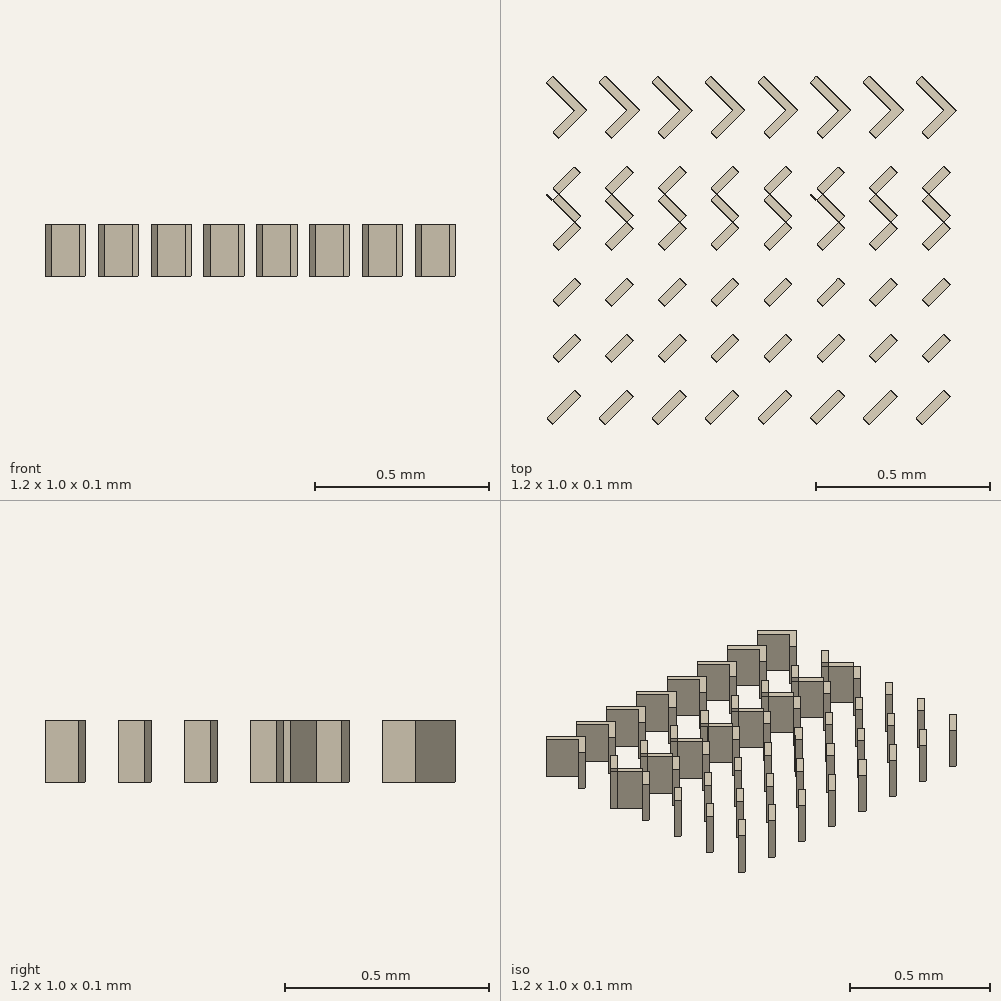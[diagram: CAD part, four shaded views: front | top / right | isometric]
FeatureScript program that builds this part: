
annotation { "Feature Type Name" : "Feature", "Feature Type Description" : "" }
export const myFeature = defineFeature(function(context is Context, id is Id, definition is map)
    precondition{}
    {
        {
            var Q0;
            Q0=qCreatedBy(makeId("Top.planeOp"),FACE);
            var sketch = newSketch(context, id + "F0", { "sketchPlane" : qUnion([Q0])});
            skLineSegment(sketch, "E0.bottom", {"start": v(-3.83, 2.01) * mm, "end": v(-3.93, 2.1) * mm});
            skLineSegment(sketch, "E0.top", {"start": v(-3.81, 2.03) * mm, "end": v(-3.91, 2.13) * mm});
            skLineSegment(sketch, "E0.left", {"start": v(-3.9, 1.93) * mm, "end": v(-3.9, 1.95) * mm});
            skLineSegment(sketch, "E0.right", {"start": v(-3.93, 2.1) * mm, "end": v(-3.91, 2.13) * mm});
            skPoint(sketch, "E0.middle", {"position": v(-3.95, 1.99) * mm});
            skLineSegment(sketch, "E1.bottom", {"start": v(-3.93, 1.95) * mm, "end": v(-3.83, 2.05) * mm});
            skLineSegment(sketch, "E1.top", {"start": v(-3.91, 1.93) * mm, "end": v(-3.81, 2.03) * mm});
            skLineSegment(sketch, "E1.left", {"start": v(-3.93, 1.95) * mm, "end": v(-3.91, 1.93) * mm});
            skLineSegment(sketch, "E1.right", {"start": v(-3.83, 2.05) * mm, "end": v(-3.81, 2.03) * mm});
            skPoint(sketch, "E1.middle", {"position": v(-3.87, 1.99) * mm});
            skLineSegment(sketch, "E2.bottom", {"start": v(-3.83, 1.85) * mm, "end": v(-3.93, 1.95) * mm});
            skLineSegment(sketch, "E2.top", {"start": v(-3.81, 1.87) * mm, "end": v(-3.91, 1.97) * mm});
            skLineSegment(sketch, "E2.left", {"start": v(-3.9, 1.77) * mm, "end": v(-3.9, 1.79) * mm});
            skLineSegment(sketch, "E2.right", {"start": v(-3.93, 1.95) * mm, "end": v(-3.91, 1.97) * mm});
            skPoint(sketch, "E2.middle", {"position": v(-3.95, 1.83) * mm});
            skLineSegment(sketch, "E3.bottom", {"start": v(-3.93, 1.79) * mm, "end": v(-3.83, 1.89) * mm});
            skLineSegment(sketch, "E3.top", {"start": v(-3.91, 1.77) * mm, "end": v(-3.81, 1.87) * mm});
            skLineSegment(sketch, "E3.left", {"start": v(-3.93, 1.79) * mm, "end": v(-3.91, 1.77) * mm});
            skLineSegment(sketch, "E3.right", {"start": v(-3.83, 1.89) * mm, "end": v(-3.81, 1.87) * mm});
            skPoint(sketch, "E3.middle", {"position": v(-3.87, 1.83) * mm});
            skLineSegment(sketch, "E4.bottom", {"start": v(-3.83, 1.69) * mm, "end": v(-3.93, 1.79) * mm});
            skLineSegment(sketch, "E4.top", {"start": v(-3.81, 1.7) * mm, "end": v(-3.9, 1.8) * mm});
            skLineSegment(sketch, "E4.left", {"start": v(-3.9, 1.6) * mm, "end": v(-3.9, 1.62) * mm});
            skLineSegment(sketch, "E4.right", {"start": v(-3.93, 1.79) * mm, "end": v(-3.9, 1.8) * mm});
            skPoint(sketch, "E4.middle", {"position": v(-3.95, 1.67) * mm});
            skLineSegment(sketch, "E5.bottom", {"start": v(-3.93, 1.63) * mm, "end": v(-3.83, 1.72) * mm});
            skLineSegment(sketch, "E5.top", {"start": v(-3.9, 1.6) * mm, "end": v(-3.81, 1.7) * mm});
            skLineSegment(sketch, "E5.left", {"start": v(-3.93, 1.63) * mm, "end": v(-3.9, 1.6) * mm});
            skLineSegment(sketch, "E5.right", {"start": v(-3.83, 1.72) * mm, "end": v(-3.81, 1.7) * mm});
            skPoint(sketch, "E5.middle", {"position": v(-3.87, 1.67) * mm});
            skLineSegment(sketch, "E6.bottom", {"start": v(-3.83, 1.53) * mm, "end": v(-3.93, 1.63) * mm});
            skLineSegment(sketch, "E6.top", {"start": v(-3.81, 1.54) * mm, "end": v(-3.9, 1.64) * mm});
            skLineSegment(sketch, "E6.left", {"start": v(-3.9, 1.45) * mm, "end": v(-3.9, 1.46) * mm});
            skLineSegment(sketch, "E6.right", {"start": v(-3.93, 1.63) * mm, "end": v(-3.9, 1.64) * mm});
            skPoint(sketch, "E6.middle", {"position": v(-3.95, 1.5) * mm});
            skLineSegment(sketch, "E7.bottom", {"start": v(-3.93, 1.46) * mm, "end": v(-3.83, 1.56) * mm});
            skLineSegment(sketch, "E7.top", {"start": v(-3.9, 1.45) * mm, "end": v(-3.81, 1.54) * mm});
            skLineSegment(sketch, "E7.left", {"start": v(-3.93, 1.46) * mm, "end": v(-3.9, 1.45) * mm});
            skLineSegment(sketch, "E7.right", {"start": v(-3.83, 1.56) * mm, "end": v(-3.81, 1.54) * mm});
            skPoint(sketch, "E7.middle", {"position": v(-3.87, 1.5) * mm});
            skLineSegment(sketch, "E8.bottom", {"start": v(-3.83, 1.36) * mm, "end": v(-3.93, 1.46) * mm});
            skLineSegment(sketch, "E8.top", {"start": v(-3.81, 1.38) * mm, "end": v(-3.9, 1.48) * mm});
            skLineSegment(sketch, "E8.left", {"start": v(-3.9, 1.28) * mm, "end": v(-3.9, 1.3) * mm});
            skLineSegment(sketch, "E8.right", {"start": v(-3.93, 1.46) * mm, "end": v(-3.9, 1.48) * mm});
            skPoint(sketch, "E8.middle", {"position": v(-3.95, 1.34) * mm});
            skLineSegment(sketch, "E9.bottom", {"start": v(-3.93, 1.3) * mm, "end": v(-3.83, 1.4) * mm});
            skLineSegment(sketch, "E9.top", {"start": v(-3.9, 1.28) * mm, "end": v(-3.81, 1.38) * mm});
            skLineSegment(sketch, "E9.left", {"start": v(-3.93, 1.3) * mm, "end": v(-3.9, 1.28) * mm});
            skLineSegment(sketch, "E9.right", {"start": v(-3.83, 1.4) * mm, "end": v(-3.81, 1.38) * mm});
            skPoint(sketch, "E9.middle", {"position": v(-3.87, 1.34) * mm});
            skLineSegment(sketch, "E10.bottom", {"start": v(-3.83, 1.2) * mm, "end": v(-3.93, 1.3) * mm});
            skLineSegment(sketch, "E10.top", {"start": v(-3.81, 1.22) * mm, "end": v(-3.9, 1.32) * mm});
            skLineSegment(sketch, "E10.left", {"start": v(-3.9, 1.12) * mm, "end": v(-3.9, 1.14) * mm});
            skLineSegment(sketch, "E10.right", {"start": v(-3.93, 1.3) * mm, "end": v(-3.9, 1.32) * mm});
            skPoint(sketch, "E10.middle", {"position": v(-3.95, 1.18) * mm});
            skLineSegment(sketch, "E11.bottom", {"start": v(-3.93, 1.14) * mm, "end": v(-3.83, 1.24) * mm});
            skLineSegment(sketch, "E11.top", {"start": v(-3.9, 1.12) * mm, "end": v(-3.81, 1.22) * mm});
            skLineSegment(sketch, "E11.left", {"start": v(-3.93, 1.14) * mm, "end": v(-3.9, 1.12) * mm});
            skLineSegment(sketch, "E11.right", {"start": v(-3.83, 1.24) * mm, "end": v(-3.81, 1.22) * mm});
            skPoint(sketch, "E11.middle", {"position": v(-3.87, 1.18) * mm});
            skLineSegment(sketch, "E12.0.1.0", {"start": v(-3.83, 3.56) * mm, "end": v(-3.93, 3.66) * mm});
            skLineSegment(sketch, "E12.0.1.1", {"start": v(-3.83, 3.24) * mm, "end": v(-3.93, 3.33) * mm});
            skPoint(sketch, "E12.0.1.2", {"position": v(-3.87, 4.02) * mm});
            skLineSegment(sketch, "E12.0.1.3", {"start": v(-3.81, 4.06) * mm, "end": v(-3.91, 4.16) * mm});
            skPoint(sketch, "E12.0.1.4", {"position": v(-3.95, 3.37) * mm});
            skLineSegment(sketch, "E12.0.1.5", {"start": v(-3.83, 4.04) * mm, "end": v(-3.93, 4.14) * mm});
            skPoint(sketch, "E12.0.1.6", {"position": v(-3.95, 3.54) * mm});
            skPoint(sketch, "E12.0.1.7", {"position": v(-3.95, 3.86) * mm});
            skPoint(sketch, "E12.0.1.8", {"position": v(-3.87, 3.37) * mm});
            skPoint(sketch, "E12.0.1.9", {"position": v(-3.87, 3.7) * mm});
            skLineSegment(sketch, "E12.0.1.10", {"start": v(-3.83, 3.4) * mm, "end": v(-3.93, 3.5) * mm});
            skPoint(sketch, "E12.0.1.11", {"position": v(-3.87, 3.54) * mm});
            skPoint(sketch, "E12.0.1.12", {"position": v(-3.87, 3.21) * mm});
            skLineSegment(sketch, "E12.0.1.13", {"start": v(-3.83, 3.72) * mm, "end": v(-3.93, 3.82) * mm});
            skPoint(sketch, "E12.0.1.14", {"position": v(-3.95, 4.02) * mm});
            skPoint(sketch, "E12.0.1.15", {"position": v(-3.95, 3.7) * mm});
            skLineSegment(sketch, "E12.0.1.16", {"start": v(-3.83, 3.88) * mm, "end": v(-3.93, 3.98) * mm});
            skPoint(sketch, "E12.0.1.17", {"position": v(-3.95, 3.21) * mm});
            skPoint(sketch, "E12.0.1.18", {"position": v(-3.87, 3.86) * mm});
            skLineSegment(sketch, "E12.0.1.19", {"start": v(-3.81, 3.41) * mm, "end": v(-3.9, 3.51) * mm});
            skLineSegment(sketch, "E12.0.1.20", {"start": v(-3.93, 3.98) * mm, "end": v(-3.83, 4.08) * mm});
            skLineSegment(sketch, "E12.0.1.21", {"start": v(-3.91, 3.8) * mm, "end": v(-3.81, 3.9) * mm});
            skLineSegment(sketch, "E12.0.1.22", {"start": v(-3.81, 3.58) * mm, "end": v(-3.9, 3.68) * mm});
            skLineSegment(sketch, "E12.0.1.23", {"start": v(-3.9, 3.32) * mm, "end": v(-3.81, 3.41) * mm});
            skLineSegment(sketch, "E12.0.1.24", {"start": v(-3.9, 3.64) * mm, "end": v(-3.81, 3.74) * mm});
            skLineSegment(sketch, "E12.0.1.25", {"start": v(-3.93, 3.5) * mm, "end": v(-3.83, 3.6) * mm});
            skLineSegment(sketch, "E12.0.1.26", {"start": v(-3.93, 3.17) * mm, "end": v(-3.83, 3.27) * mm});
            skLineSegment(sketch, "E12.0.1.27", {"start": v(-3.9, 3.48) * mm, "end": v(-3.81, 3.58) * mm});
            skLineSegment(sketch, "E12.0.1.28", {"start": v(-3.93, 3.33) * mm, "end": v(-3.83, 3.43) * mm});
            skLineSegment(sketch, "E12.0.1.29", {"start": v(-3.9, 3.15) * mm, "end": v(-3.81, 3.25) * mm});
            skLineSegment(sketch, "E12.0.1.30", {"start": v(-3.93, 3.66) * mm, "end": v(-3.83, 3.76) * mm});
            skLineSegment(sketch, "E12.0.1.31", {"start": v(-3.93, 3.82) * mm, "end": v(-3.83, 3.92) * mm});
            skLineSegment(sketch, "E12.0.1.32", {"start": v(-3.91, 3.96) * mm, "end": v(-3.81, 4.06) * mm});
            skLineSegment(sketch, "E12.0.1.33", {"start": v(-3.93, 4.14) * mm, "end": v(-3.91, 4.16) * mm});
            skLineSegment(sketch, "E12.0.1.34", {"start": v(-3.81, 3.74) * mm, "end": v(-3.9, 3.84) * mm});
            skLineSegment(sketch, "E12.0.1.35", {"start": v(-3.81, 3.25) * mm, "end": v(-3.9, 3.35) * mm});
            skLineSegment(sketch, "E12.0.1.36", {"start": v(-3.81, 3.9) * mm, "end": v(-3.91, 4) * mm});
            skLineSegment(sketch, "E12.0.1.37", {"start": v(-3.83, 3.92) * mm, "end": v(-3.81, 3.9) * mm});
            skLineSegment(sketch, "E12.0.1.38", {"start": v(-3.83, 3.6) * mm, "end": v(-3.81, 3.58) * mm});
            skLineSegment(sketch, "E12.0.1.39", {"start": v(-3.83, 3.27) * mm, "end": v(-3.81, 3.25) * mm});
            skLineSegment(sketch, "E12.0.1.40", {"start": v(-3.83, 3.76) * mm, "end": v(-3.81, 3.74) * mm});
            skLineSegment(sketch, "E12.0.1.41", {"start": v(-3.83, 3.43) * mm, "end": v(-3.81, 3.41) * mm});
            skLineSegment(sketch, "E12.0.1.42", {"start": v(-3.83, 4.08) * mm, "end": v(-3.81, 4.06) * mm});
            skLineSegment(sketch, "E12.0.1.43", {"start": v(-3.93, 3.82) * mm, "end": v(-3.9, 3.84) * mm});
            skLineSegment(sketch, "E12.0.1.44", {"start": v(-3.93, 3.82) * mm, "end": v(-3.91, 3.8) * mm});
            skLineSegment(sketch, "E12.0.1.45", {"start": v(-3.93, 3.17) * mm, "end": v(-3.9, 3.15) * mm});
            skLineSegment(sketch, "E12.0.1.46", {"start": v(-3.9, 3.8) * mm, "end": v(-3.9, 3.82) * mm});
            skLineSegment(sketch, "E12.0.1.47", {"start": v(-3.9, 3.15) * mm, "end": v(-3.9, 3.17) * mm});
            skLineSegment(sketch, "E12.0.1.48", {"start": v(-3.9, 3.96) * mm, "end": v(-3.9, 3.98) * mm});
            skLineSegment(sketch, "E12.0.1.49", {"start": v(-3.93, 3.33) * mm, "end": v(-3.9, 3.32) * mm});
            skLineSegment(sketch, "E12.0.1.50", {"start": v(-3.93, 3.66) * mm, "end": v(-3.9, 3.64) * mm});
            skLineSegment(sketch, "E12.0.1.51", {"start": v(-3.9, 3.64) * mm, "end": v(-3.9, 3.66) * mm});
            skLineSegment(sketch, "E12.0.1.52", {"start": v(-3.93, 3.5) * mm, "end": v(-3.9, 3.48) * mm});
            skLineSegment(sketch, "E12.0.1.53", {"start": v(-3.93, 3.66) * mm, "end": v(-3.9, 3.68) * mm});
            skLineSegment(sketch, "E12.0.1.54", {"start": v(-3.93, 3.33) * mm, "end": v(-3.9, 3.35) * mm});
            skLineSegment(sketch, "E12.0.1.55", {"start": v(-3.93, 3.98) * mm, "end": v(-3.91, 4) * mm});
            skLineSegment(sketch, "E12.0.1.56", {"start": v(-3.93, 3.98) * mm, "end": v(-3.91, 3.96) * mm});
            skLineSegment(sketch, "E12.0.1.57", {"start": v(-3.93, 3.5) * mm, "end": v(-3.9, 3.51) * mm});
            skLineSegment(sketch, "E12.0.1.58", {"start": v(-3.9, 3.48) * mm, "end": v(-3.9, 3.5) * mm});
            skLineSegment(sketch, "E12.0.1.59", {"start": v(-3.9, 3.32) * mm, "end": v(-3.9, 3.33) * mm});
            skLineSegment(sketch, "E12.1.0.0", {"start": v(-3.68, 1.53) * mm, "end": v(-3.78, 1.63) * mm});
            skLineSegment(sketch, "E12.1.0.1", {"start": v(-3.68, 1.2) * mm, "end": v(-3.78, 1.3) * mm});
            skPoint(sketch, "E12.1.0.2", {"position": v(-3.72, 1.99) * mm});
            skLineSegment(sketch, "E12.1.0.3", {"start": v(-3.66, 2.03) * mm, "end": v(-3.76, 2.13) * mm});
            skPoint(sketch, "E12.1.0.4", {"position": v(-3.8, 1.34) * mm});
            skLineSegment(sketch, "E12.1.0.5", {"start": v(-3.68, 2.01) * mm, "end": v(-3.78, 2.1) * mm});
            skPoint(sketch, "E12.1.0.6", {"position": v(-3.8, 1.5) * mm});
            skPoint(sketch, "E12.1.0.7", {"position": v(-3.8, 1.83) * mm});
            skPoint(sketch, "E12.1.0.8", {"position": v(-3.72, 1.34) * mm});
            skPoint(sketch, "E12.1.0.9", {"position": v(-3.72, 1.67) * mm});
            skLineSegment(sketch, "E12.1.0.10", {"start": v(-3.68, 1.36) * mm, "end": v(-3.78, 1.46) * mm});
            skPoint(sketch, "E12.1.0.11", {"position": v(-3.72, 1.5) * mm});
            skPoint(sketch, "E12.1.0.12", {"position": v(-3.72, 1.18) * mm});
            skLineSegment(sketch, "E12.1.0.13", {"start": v(-3.68, 1.69) * mm, "end": v(-3.78, 1.79) * mm});
            skPoint(sketch, "E12.1.0.14", {"position": v(-3.8, 1.99) * mm});
            skPoint(sketch, "E12.1.0.15", {"position": v(-3.8, 1.67) * mm});
            skLineSegment(sketch, "E12.1.0.16", {"start": v(-3.68, 1.85) * mm, "end": v(-3.78, 1.95) * mm});
            skPoint(sketch, "E12.1.0.17", {"position": v(-3.8, 1.18) * mm});
            skPoint(sketch, "E12.1.0.18", {"position": v(-3.72, 1.83) * mm});
            skLineSegment(sketch, "E12.1.0.19", {"start": v(-3.66, 1.38) * mm, "end": v(-3.76, 1.48) * mm});
            skLineSegment(sketch, "E12.1.0.20", {"start": v(-3.78, 1.95) * mm, "end": v(-3.68, 2.05) * mm});
            skLineSegment(sketch, "E12.1.0.21", {"start": v(-3.76, 1.77) * mm, "end": v(-3.66, 1.87) * mm});
            skLineSegment(sketch, "E12.1.0.22", {"start": v(-3.66, 1.54) * mm, "end": v(-3.76, 1.64) * mm});
            skLineSegment(sketch, "E12.1.0.23", {"start": v(-3.76, 1.28) * mm, "end": v(-3.66, 1.38) * mm});
            skLineSegment(sketch, "E12.1.0.24", {"start": v(-3.76, 1.6) * mm, "end": v(-3.66, 1.7) * mm});
            skLineSegment(sketch, "E12.1.0.25", {"start": v(-3.78, 1.46) * mm, "end": v(-3.68, 1.56) * mm});
            skLineSegment(sketch, "E12.1.0.26", {"start": v(-3.78, 1.14) * mm, "end": v(-3.68, 1.24) * mm});
            skLineSegment(sketch, "E12.1.0.27", {"start": v(-3.76, 1.45) * mm, "end": v(-3.66, 1.54) * mm});
            skLineSegment(sketch, "E12.1.0.28", {"start": v(-3.78, 1.3) * mm, "end": v(-3.68, 1.4) * mm});
            skLineSegment(sketch, "E12.1.0.29", {"start": v(-3.76, 1.12) * mm, "end": v(-3.66, 1.22) * mm});
            skLineSegment(sketch, "E12.1.0.30", {"start": v(-3.78, 1.63) * mm, "end": v(-3.68, 1.72) * mm});
            skLineSegment(sketch, "E12.1.0.31", {"start": v(-3.78, 1.79) * mm, "end": v(-3.68, 1.89) * mm});
            skLineSegment(sketch, "E12.1.0.32", {"start": v(-3.76, 1.93) * mm, "end": v(-3.66, 2.03) * mm});
            skLineSegment(sketch, "E12.1.0.33", {"start": v(-3.78, 2.1) * mm, "end": v(-3.76, 2.13) * mm});
            skLineSegment(sketch, "E12.1.0.34", {"start": v(-3.66, 1.7) * mm, "end": v(-3.76, 1.8) * mm});
            skLineSegment(sketch, "E12.1.0.35", {"start": v(-3.66, 1.22) * mm, "end": v(-3.76, 1.32) * mm});
            skLineSegment(sketch, "E12.1.0.36", {"start": v(-3.66, 1.87) * mm, "end": v(-3.76, 1.97) * mm});
            skLineSegment(sketch, "E12.1.0.37", {"start": v(-3.68, 1.89) * mm, "end": v(-3.66, 1.87) * mm});
            skLineSegment(sketch, "E12.1.0.38", {"start": v(-3.68, 1.56) * mm, "end": v(-3.66, 1.54) * mm});
            skLineSegment(sketch, "E12.1.0.39", {"start": v(-3.68, 1.24) * mm, "end": v(-3.66, 1.22) * mm});
            skLineSegment(sketch, "E12.1.0.40", {"start": v(-3.68, 1.72) * mm, "end": v(-3.66, 1.7) * mm});
            skLineSegment(sketch, "E12.1.0.41", {"start": v(-3.68, 1.4) * mm, "end": v(-3.66, 1.38) * mm});
            skLineSegment(sketch, "E12.1.0.42", {"start": v(-3.68, 2.05) * mm, "end": v(-3.66, 2.03) * mm});
            skLineSegment(sketch, "E12.1.0.43", {"start": v(-3.78, 1.79) * mm, "end": v(-3.76, 1.8) * mm});
            skLineSegment(sketch, "E12.1.0.44", {"start": v(-3.78, 1.79) * mm, "end": v(-3.76, 1.77) * mm});
            skLineSegment(sketch, "E12.1.0.45", {"start": v(-3.78, 1.14) * mm, "end": v(-3.76, 1.12) * mm});
            skLineSegment(sketch, "E12.1.0.46", {"start": v(-3.76, 1.77) * mm, "end": v(-3.74, 1.79) * mm});
            skLineSegment(sketch, "E12.1.0.47", {"start": v(-3.76, 1.12) * mm, "end": v(-3.74, 1.14) * mm});
            skLineSegment(sketch, "E12.1.0.48", {"start": v(-3.76, 1.93) * mm, "end": v(-3.74, 1.95) * mm});
            skLineSegment(sketch, "E12.1.0.49", {"start": v(-3.78, 1.3) * mm, "end": v(-3.76, 1.28) * mm});
            skLineSegment(sketch, "E12.1.0.50", {"start": v(-3.78, 1.63) * mm, "end": v(-3.76, 1.6) * mm});
            skLineSegment(sketch, "E12.1.0.51", {"start": v(-3.76, 1.6) * mm, "end": v(-3.74, 1.62) * mm});
            skLineSegment(sketch, "E12.1.0.52", {"start": v(-3.78, 1.46) * mm, "end": v(-3.76, 1.45) * mm});
            skLineSegment(sketch, "E12.1.0.53", {"start": v(-3.78, 1.63) * mm, "end": v(-3.76, 1.64) * mm});
            skLineSegment(sketch, "E12.1.0.54", {"start": v(-3.78, 1.3) * mm, "end": v(-3.76, 1.32) * mm});
            skLineSegment(sketch, "E12.1.0.55", {"start": v(-3.78, 1.95) * mm, "end": v(-3.76, 1.97) * mm});
            skLineSegment(sketch, "E12.1.0.56", {"start": v(-3.78, 1.95) * mm, "end": v(-3.76, 1.93) * mm});
            skLineSegment(sketch, "E12.1.0.57", {"start": v(-3.78, 1.46) * mm, "end": v(-3.76, 1.48) * mm});
            skLineSegment(sketch, "E12.1.0.58", {"start": v(-3.76, 1.45) * mm, "end": v(-3.74, 1.46) * mm});
            skLineSegment(sketch, "E12.1.0.59", {"start": v(-3.76, 1.28) * mm, "end": v(-3.74, 1.3) * mm});
            skLineSegment(sketch, "E12.1.1.0", {"start": v(-3.68, 3.56) * mm, "end": v(-3.78, 3.66) * mm});
            skLineSegment(sketch, "E12.1.1.1", {"start": v(-3.68, 3.24) * mm, "end": v(-3.78, 3.33) * mm});
            skPoint(sketch, "E12.1.1.2", {"position": v(-3.72, 4.02) * mm});
            skLineSegment(sketch, "E12.1.1.3", {"start": v(-3.66, 4.06) * mm, "end": v(-3.76, 4.16) * mm});
            skPoint(sketch, "E12.1.1.4", {"position": v(-3.8, 3.37) * mm});
            skLineSegment(sketch, "E12.1.1.5", {"start": v(-3.68, 4.04) * mm, "end": v(-3.78, 4.14) * mm});
            skPoint(sketch, "E12.1.1.6", {"position": v(-3.8, 3.54) * mm});
            skPoint(sketch, "E12.1.1.7", {"position": v(-3.8, 3.86) * mm});
            skPoint(sketch, "E12.1.1.8", {"position": v(-3.72, 3.37) * mm});
            skPoint(sketch, "E12.1.1.9", {"position": v(-3.72, 3.7) * mm});
            skLineSegment(sketch, "E12.1.1.10", {"start": v(-3.68, 3.4) * mm, "end": v(-3.78, 3.5) * mm});
            skPoint(sketch, "E12.1.1.11", {"position": v(-3.72, 3.54) * mm});
            skPoint(sketch, "E12.1.1.12", {"position": v(-3.72, 3.21) * mm});
            skLineSegment(sketch, "E12.1.1.13", {"start": v(-3.68, 3.72) * mm, "end": v(-3.78, 3.82) * mm});
            skPoint(sketch, "E12.1.1.14", {"position": v(-3.8, 4.02) * mm});
            skPoint(sketch, "E12.1.1.15", {"position": v(-3.8, 3.7) * mm});
            skLineSegment(sketch, "E12.1.1.16", {"start": v(-3.68, 3.88) * mm, "end": v(-3.78, 3.98) * mm});
            skPoint(sketch, "E12.1.1.17", {"position": v(-3.8, 3.21) * mm});
            skPoint(sketch, "E12.1.1.18", {"position": v(-3.72, 3.86) * mm});
            skLineSegment(sketch, "E12.1.1.19", {"start": v(-3.66, 3.41) * mm, "end": v(-3.76, 3.51) * mm});
            skLineSegment(sketch, "E12.1.1.20", {"start": v(-3.78, 3.98) * mm, "end": v(-3.68, 4.08) * mm});
            skLineSegment(sketch, "E12.1.1.21", {"start": v(-3.76, 3.8) * mm, "end": v(-3.66, 3.9) * mm});
            skLineSegment(sketch, "E12.1.1.22", {"start": v(-3.66, 3.58) * mm, "end": v(-3.76, 3.68) * mm});
            skLineSegment(sketch, "E12.1.1.23", {"start": v(-3.76, 3.32) * mm, "end": v(-3.66, 3.41) * mm});
            skLineSegment(sketch, "E12.1.1.24", {"start": v(-3.76, 3.64) * mm, "end": v(-3.66, 3.74) * mm});
            skLineSegment(sketch, "E12.1.1.25", {"start": v(-3.78, 3.5) * mm, "end": v(-3.68, 3.6) * mm});
            skLineSegment(sketch, "E12.1.1.26", {"start": v(-3.78, 3.17) * mm, "end": v(-3.68, 3.27) * mm});
            skLineSegment(sketch, "E12.1.1.27", {"start": v(-3.76, 3.48) * mm, "end": v(-3.66, 3.58) * mm});
            skLineSegment(sketch, "E12.1.1.28", {"start": v(-3.78, 3.33) * mm, "end": v(-3.68, 3.43) * mm});
            skLineSegment(sketch, "E12.1.1.29", {"start": v(-3.76, 3.15) * mm, "end": v(-3.66, 3.25) * mm});
            skLineSegment(sketch, "E12.1.1.30", {"start": v(-3.78, 3.66) * mm, "end": v(-3.68, 3.76) * mm});
            skLineSegment(sketch, "E12.1.1.31", {"start": v(-3.78, 3.82) * mm, "end": v(-3.68, 3.92) * mm});
            skLineSegment(sketch, "E12.1.1.32", {"start": v(-3.76, 3.96) * mm, "end": v(-3.66, 4.06) * mm});
            skLineSegment(sketch, "E12.1.1.33", {"start": v(-3.78, 4.14) * mm, "end": v(-3.76, 4.16) * mm});
            skLineSegment(sketch, "E12.1.1.34", {"start": v(-3.66, 3.74) * mm, "end": v(-3.76, 3.84) * mm});
            skLineSegment(sketch, "E12.1.1.35", {"start": v(-3.66, 3.25) * mm, "end": v(-3.76, 3.35) * mm});
            skLineSegment(sketch, "E12.1.1.36", {"start": v(-3.66, 3.9) * mm, "end": v(-3.76, 4) * mm});
            skLineSegment(sketch, "E12.1.1.37", {"start": v(-3.68, 3.92) * mm, "end": v(-3.66, 3.9) * mm});
            skLineSegment(sketch, "E12.1.1.38", {"start": v(-3.68, 3.6) * mm, "end": v(-3.66, 3.58) * mm});
            skLineSegment(sketch, "E12.1.1.39", {"start": v(-3.68, 3.27) * mm, "end": v(-3.66, 3.25) * mm});
            skLineSegment(sketch, "E12.1.1.40", {"start": v(-3.68, 3.76) * mm, "end": v(-3.66, 3.74) * mm});
            skLineSegment(sketch, "E12.1.1.41", {"start": v(-3.68, 3.43) * mm, "end": v(-3.66, 3.41) * mm});
            skLineSegment(sketch, "E12.1.1.42", {"start": v(-3.68, 4.08) * mm, "end": v(-3.66, 4.06) * mm});
            skLineSegment(sketch, "E12.1.1.43", {"start": v(-3.78, 3.82) * mm, "end": v(-3.76, 3.84) * mm});
            skLineSegment(sketch, "E12.1.1.44", {"start": v(-3.78, 3.82) * mm, "end": v(-3.76, 3.8) * mm});
            skLineSegment(sketch, "E12.1.1.45", {"start": v(-3.78, 3.17) * mm, "end": v(-3.76, 3.15) * mm});
            skLineSegment(sketch, "E12.1.1.46", {"start": v(-3.76, 3.8) * mm, "end": v(-3.74, 3.82) * mm});
            skLineSegment(sketch, "E12.1.1.47", {"start": v(-3.76, 3.15) * mm, "end": v(-3.74, 3.17) * mm});
            skLineSegment(sketch, "E12.1.1.48", {"start": v(-3.76, 3.96) * mm, "end": v(-3.74, 3.98) * mm});
            skLineSegment(sketch, "E12.1.1.49", {"start": v(-3.78, 3.33) * mm, "end": v(-3.76, 3.32) * mm});
            skLineSegment(sketch, "E12.1.1.50", {"start": v(-3.78, 3.66) * mm, "end": v(-3.76, 3.64) * mm});
            skLineSegment(sketch, "E12.1.1.51", {"start": v(-3.76, 3.64) * mm, "end": v(-3.74, 3.66) * mm});
            skLineSegment(sketch, "E12.1.1.52", {"start": v(-3.78, 3.5) * mm, "end": v(-3.76, 3.48) * mm});
            skLineSegment(sketch, "E12.1.1.53", {"start": v(-3.78, 3.66) * mm, "end": v(-3.76, 3.68) * mm});
            skLineSegment(sketch, "E12.1.1.54", {"start": v(-3.78, 3.33) * mm, "end": v(-3.76, 3.35) * mm});
            skLineSegment(sketch, "E12.1.1.55", {"start": v(-3.78, 3.98) * mm, "end": v(-3.76, 4) * mm});
            skLineSegment(sketch, "E12.1.1.56", {"start": v(-3.78, 3.98) * mm, "end": v(-3.76, 3.96) * mm});
            skLineSegment(sketch, "E12.1.1.57", {"start": v(-3.78, 3.5) * mm, "end": v(-3.76, 3.51) * mm});
            skLineSegment(sketch, "E12.1.1.58", {"start": v(-3.76, 3.48) * mm, "end": v(-3.74, 3.5) * mm});
            skLineSegment(sketch, "E12.1.1.59", {"start": v(-3.76, 3.32) * mm, "end": v(-3.74, 3.33) * mm});
            skLineSegment(sketch, "E12.2.0.0", {"start": v(-3.52, 1.53) * mm, "end": v(-3.62, 1.63) * mm});
            skLineSegment(sketch, "E12.2.0.1", {"start": v(-3.52, 1.2) * mm, "end": v(-3.62, 1.3) * mm});
            skPoint(sketch, "E12.2.0.2", {"position": v(-3.56, 1.99) * mm});
            skLineSegment(sketch, "E12.2.0.3", {"start": v(-3.5, 2.03) * mm, "end": v(-3.6, 2.13) * mm});
            skPoint(sketch, "E12.2.0.4", {"position": v(-3.65, 1.34) * mm});
            skLineSegment(sketch, "E12.2.0.5", {"start": v(-3.52, 2.01) * mm, "end": v(-3.62, 2.1) * mm});
            skPoint(sketch, "E12.2.0.6", {"position": v(-3.65, 1.5) * mm});
            skPoint(sketch, "E12.2.0.7", {"position": v(-3.65, 1.83) * mm});
            skPoint(sketch, "E12.2.0.8", {"position": v(-3.56, 1.34) * mm});
            skPoint(sketch, "E12.2.0.9", {"position": v(-3.56, 1.67) * mm});
            skLineSegment(sketch, "E12.2.0.10", {"start": v(-3.52, 1.36) * mm, "end": v(-3.62, 1.46) * mm});
            skPoint(sketch, "E12.2.0.11", {"position": v(-3.56, 1.5) * mm});
            skPoint(sketch, "E12.2.0.12", {"position": v(-3.56, 1.18) * mm});
            skLineSegment(sketch, "E12.2.0.13", {"start": v(-3.52, 1.69) * mm, "end": v(-3.62, 1.79) * mm});
            skPoint(sketch, "E12.2.0.14", {"position": v(-3.65, 1.99) * mm});
            skPoint(sketch, "E12.2.0.15", {"position": v(-3.65, 1.67) * mm});
            skLineSegment(sketch, "E12.2.0.16", {"start": v(-3.52, 1.85) * mm, "end": v(-3.62, 1.95) * mm});
            skPoint(sketch, "E12.2.0.17", {"position": v(-3.65, 1.18) * mm});
            skPoint(sketch, "E12.2.0.18", {"position": v(-3.56, 1.83) * mm});
            skLineSegment(sketch, "E12.2.0.19", {"start": v(-3.5, 1.38) * mm, "end": v(-3.6, 1.48) * mm});
            skLineSegment(sketch, "E12.2.0.20", {"start": v(-3.62, 1.95) * mm, "end": v(-3.52, 2.05) * mm});
            skLineSegment(sketch, "E12.2.0.21", {"start": v(-3.6, 1.77) * mm, "end": v(-3.5, 1.87) * mm});
            skLineSegment(sketch, "E12.2.0.22", {"start": v(-3.5, 1.54) * mm, "end": v(-3.6, 1.64) * mm});
            skLineSegment(sketch, "E12.2.0.23", {"start": v(-3.6, 1.28) * mm, "end": v(-3.5, 1.38) * mm});
            skLineSegment(sketch, "E12.2.0.24", {"start": v(-3.6, 1.6) * mm, "end": v(-3.5, 1.7) * mm});
            skLineSegment(sketch, "E12.2.0.25", {"start": v(-3.62, 1.46) * mm, "end": v(-3.52, 1.56) * mm});
            skLineSegment(sketch, "E12.2.0.26", {"start": v(-3.62, 1.14) * mm, "end": v(-3.52, 1.24) * mm});
            skLineSegment(sketch, "E12.2.0.27", {"start": v(-3.6, 1.45) * mm, "end": v(-3.5, 1.54) * mm});
            skLineSegment(sketch, "E12.2.0.28", {"start": v(-3.62, 1.3) * mm, "end": v(-3.52, 1.4) * mm});
            skLineSegment(sketch, "E12.2.0.29", {"start": v(-3.6, 1.12) * mm, "end": v(-3.5, 1.22) * mm});
            skLineSegment(sketch, "E12.2.0.30", {"start": v(-3.62, 1.63) * mm, "end": v(-3.52, 1.72) * mm});
            skLineSegment(sketch, "E12.2.0.31", {"start": v(-3.62, 1.79) * mm, "end": v(-3.52, 1.89) * mm});
            skLineSegment(sketch, "E12.2.0.32", {"start": v(-3.6, 1.93) * mm, "end": v(-3.5, 2.03) * mm});
            skLineSegment(sketch, "E12.2.0.33", {"start": v(-3.62, 2.1) * mm, "end": v(-3.6, 2.13) * mm});
            skLineSegment(sketch, "E12.2.0.34", {"start": v(-3.5, 1.7) * mm, "end": v(-3.6, 1.8) * mm});
            skLineSegment(sketch, "E12.2.0.35", {"start": v(-3.5, 1.22) * mm, "end": v(-3.6, 1.32) * mm});
            skLineSegment(sketch, "E12.2.0.36", {"start": v(-3.5, 1.87) * mm, "end": v(-3.6, 1.97) * mm});
            skLineSegment(sketch, "E12.2.0.37", {"start": v(-3.52, 1.89) * mm, "end": v(-3.5, 1.87) * mm});
            skLineSegment(sketch, "E12.2.0.38", {"start": v(-3.52, 1.56) * mm, "end": v(-3.5, 1.54) * mm});
            skLineSegment(sketch, "E12.2.0.39", {"start": v(-3.52, 1.24) * mm, "end": v(-3.5, 1.22) * mm});
            skLineSegment(sketch, "E12.2.0.40", {"start": v(-3.52, 1.72) * mm, "end": v(-3.5, 1.7) * mm});
            skLineSegment(sketch, "E12.2.0.41", {"start": v(-3.52, 1.4) * mm, "end": v(-3.5, 1.38) * mm});
            skLineSegment(sketch, "E12.2.0.42", {"start": v(-3.52, 2.05) * mm, "end": v(-3.5, 2.03) * mm});
            skLineSegment(sketch, "E12.2.0.43", {"start": v(-3.62, 1.79) * mm, "end": v(-3.6, 1.8) * mm});
            skLineSegment(sketch, "E12.2.0.44", {"start": v(-3.62, 1.79) * mm, "end": v(-3.6, 1.77) * mm});
            skLineSegment(sketch, "E12.2.0.45", {"start": v(-3.62, 1.14) * mm, "end": v(-3.6, 1.12) * mm});
            skLineSegment(sketch, "E12.2.0.46", {"start": v(-3.6, 1.77) * mm, "end": v(-3.59, 1.79) * mm});
            skLineSegment(sketch, "E12.2.0.47", {"start": v(-3.6, 1.12) * mm, "end": v(-3.59, 1.14) * mm});
            skLineSegment(sketch, "E12.2.0.48", {"start": v(-3.6, 1.93) * mm, "end": v(-3.59, 1.95) * mm});
            skLineSegment(sketch, "E12.2.0.49", {"start": v(-3.62, 1.3) * mm, "end": v(-3.6, 1.28) * mm});
            skLineSegment(sketch, "E12.2.0.50", {"start": v(-3.62, 1.63) * mm, "end": v(-3.6, 1.6) * mm});
            skLineSegment(sketch, "E12.2.0.51", {"start": v(-3.6, 1.6) * mm, "end": v(-3.59, 1.62) * mm});
            skLineSegment(sketch, "E12.2.0.52", {"start": v(-3.62, 1.46) * mm, "end": v(-3.6, 1.45) * mm});
            skLineSegment(sketch, "E12.2.0.53", {"start": v(-3.62, 1.63) * mm, "end": v(-3.6, 1.64) * mm});
            skLineSegment(sketch, "E12.2.0.54", {"start": v(-3.62, 1.3) * mm, "end": v(-3.6, 1.32) * mm});
            skLineSegment(sketch, "E12.2.0.55", {"start": v(-3.62, 1.95) * mm, "end": v(-3.6, 1.97) * mm});
            skLineSegment(sketch, "E12.2.0.56", {"start": v(-3.62, 1.95) * mm, "end": v(-3.6, 1.93) * mm});
            skLineSegment(sketch, "E12.2.0.57", {"start": v(-3.62, 1.46) * mm, "end": v(-3.6, 1.48) * mm});
            skLineSegment(sketch, "E12.2.0.58", {"start": v(-3.6, 1.45) * mm, "end": v(-3.59, 1.46) * mm});
            skLineSegment(sketch, "E12.2.0.59", {"start": v(-3.6, 1.28) * mm, "end": v(-3.59, 1.3) * mm});
            skLineSegment(sketch, "E12.2.1.0", {"start": v(-3.52, 3.56) * mm, "end": v(-3.62, 3.66) * mm});
            skLineSegment(sketch, "E12.2.1.1", {"start": v(-3.52, 3.24) * mm, "end": v(-3.62, 3.33) * mm});
            skPoint(sketch, "E12.2.1.2", {"position": v(-3.56, 4.02) * mm});
            skLineSegment(sketch, "E12.2.1.3", {"start": v(-3.5, 4.06) * mm, "end": v(-3.6, 4.16) * mm});
            skPoint(sketch, "E12.2.1.4", {"position": v(-3.65, 3.37) * mm});
            skLineSegment(sketch, "E12.2.1.5", {"start": v(-3.52, 4.04) * mm, "end": v(-3.62, 4.14) * mm});
            skPoint(sketch, "E12.2.1.6", {"position": v(-3.65, 3.54) * mm});
            skPoint(sketch, "E12.2.1.7", {"position": v(-3.65, 3.86) * mm});
            skPoint(sketch, "E12.2.1.8", {"position": v(-3.56, 3.37) * mm});
            skPoint(sketch, "E12.2.1.9", {"position": v(-3.56, 3.7) * mm});
            skLineSegment(sketch, "E12.2.1.10", {"start": v(-3.52, 3.4) * mm, "end": v(-3.62, 3.5) * mm});
            skPoint(sketch, "E12.2.1.11", {"position": v(-3.56, 3.54) * mm});
            skPoint(sketch, "E12.2.1.12", {"position": v(-3.56, 3.21) * mm});
            skLineSegment(sketch, "E12.2.1.13", {"start": v(-3.52, 3.72) * mm, "end": v(-3.62, 3.82) * mm});
            skPoint(sketch, "E12.2.1.14", {"position": v(-3.65, 4.02) * mm});
            skPoint(sketch, "E12.2.1.15", {"position": v(-3.65, 3.7) * mm});
            skLineSegment(sketch, "E12.2.1.16", {"start": v(-3.52, 3.88) * mm, "end": v(-3.62, 3.98) * mm});
            skPoint(sketch, "E12.2.1.17", {"position": v(-3.65, 3.21) * mm});
            skPoint(sketch, "E12.2.1.18", {"position": v(-3.56, 3.86) * mm});
            skLineSegment(sketch, "E12.2.1.19", {"start": v(-3.5, 3.41) * mm, "end": v(-3.6, 3.51) * mm});
            skLineSegment(sketch, "E12.2.1.20", {"start": v(-3.62, 3.98) * mm, "end": v(-3.52, 4.08) * mm});
            skLineSegment(sketch, "E12.2.1.21", {"start": v(-3.6, 3.8) * mm, "end": v(-3.5, 3.9) * mm});
            skLineSegment(sketch, "E12.2.1.22", {"start": v(-3.5, 3.58) * mm, "end": v(-3.6, 3.68) * mm});
            skLineSegment(sketch, "E12.2.1.23", {"start": v(-3.6, 3.32) * mm, "end": v(-3.5, 3.41) * mm});
            skLineSegment(sketch, "E12.2.1.24", {"start": v(-3.6, 3.64) * mm, "end": v(-3.5, 3.74) * mm});
            skLineSegment(sketch, "E12.2.1.25", {"start": v(-3.62, 3.5) * mm, "end": v(-3.52, 3.6) * mm});
            skLineSegment(sketch, "E12.2.1.26", {"start": v(-3.62, 3.17) * mm, "end": v(-3.52, 3.27) * mm});
            skLineSegment(sketch, "E12.2.1.27", {"start": v(-3.6, 3.48) * mm, "end": v(-3.5, 3.58) * mm});
            skLineSegment(sketch, "E12.2.1.28", {"start": v(-3.62, 3.33) * mm, "end": v(-3.52, 3.43) * mm});
            skLineSegment(sketch, "E12.2.1.29", {"start": v(-3.6, 3.15) * mm, "end": v(-3.5, 3.25) * mm});
            skLineSegment(sketch, "E12.2.1.30", {"start": v(-3.62, 3.66) * mm, "end": v(-3.52, 3.76) * mm});
            skLineSegment(sketch, "E12.2.1.31", {"start": v(-3.62, 3.82) * mm, "end": v(-3.52, 3.92) * mm});
            skLineSegment(sketch, "E12.2.1.32", {"start": v(-3.6, 3.96) * mm, "end": v(-3.5, 4.06) * mm});
            skLineSegment(sketch, "E12.2.1.33", {"start": v(-3.62, 4.14) * mm, "end": v(-3.6, 4.16) * mm});
            skLineSegment(sketch, "E12.2.1.34", {"start": v(-3.5, 3.74) * mm, "end": v(-3.6, 3.84) * mm});
            skLineSegment(sketch, "E12.2.1.35", {"start": v(-3.5, 3.25) * mm, "end": v(-3.6, 3.35) * mm});
            skLineSegment(sketch, "E12.2.1.36", {"start": v(-3.5, 3.9) * mm, "end": v(-3.6, 4) * mm});
            skLineSegment(sketch, "E12.2.1.37", {"start": v(-3.52, 3.92) * mm, "end": v(-3.5, 3.9) * mm});
            skLineSegment(sketch, "E12.2.1.38", {"start": v(-3.52, 3.6) * mm, "end": v(-3.5, 3.58) * mm});
            skLineSegment(sketch, "E12.2.1.39", {"start": v(-3.52, 3.27) * mm, "end": v(-3.5, 3.25) * mm});
            skLineSegment(sketch, "E12.2.1.40", {"start": v(-3.52, 3.76) * mm, "end": v(-3.5, 3.74) * mm});
            skLineSegment(sketch, "E12.2.1.41", {"start": v(-3.52, 3.43) * mm, "end": v(-3.5, 3.41) * mm});
            skLineSegment(sketch, "E12.2.1.42", {"start": v(-3.52, 4.08) * mm, "end": v(-3.5, 4.06) * mm});
            skLineSegment(sketch, "E12.2.1.43", {"start": v(-3.62, 3.82) * mm, "end": v(-3.6, 3.84) * mm});
            skLineSegment(sketch, "E12.2.1.44", {"start": v(-3.62, 3.82) * mm, "end": v(-3.6, 3.8) * mm});
            skLineSegment(sketch, "E12.2.1.45", {"start": v(-3.62, 3.17) * mm, "end": v(-3.6, 3.15) * mm});
            skLineSegment(sketch, "E12.2.1.46", {"start": v(-3.6, 3.8) * mm, "end": v(-3.59, 3.82) * mm});
            skLineSegment(sketch, "E12.2.1.47", {"start": v(-3.6, 3.15) * mm, "end": v(-3.59, 3.17) * mm});
            skLineSegment(sketch, "E12.2.1.48", {"start": v(-3.6, 3.96) * mm, "end": v(-3.59, 3.98) * mm});
            skLineSegment(sketch, "E12.2.1.49", {"start": v(-3.62, 3.33) * mm, "end": v(-3.6, 3.32) * mm});
            skLineSegment(sketch, "E12.2.1.50", {"start": v(-3.62, 3.66) * mm, "end": v(-3.6, 3.64) * mm});
            skLineSegment(sketch, "E12.2.1.51", {"start": v(-3.6, 3.64) * mm, "end": v(-3.59, 3.66) * mm});
            skLineSegment(sketch, "E12.2.1.52", {"start": v(-3.62, 3.5) * mm, "end": v(-3.6, 3.48) * mm});
            skLineSegment(sketch, "E12.2.1.53", {"start": v(-3.62, 3.66) * mm, "end": v(-3.6, 3.68) * mm});
            skLineSegment(sketch, "E12.2.1.54", {"start": v(-3.62, 3.33) * mm, "end": v(-3.6, 3.35) * mm});
            skLineSegment(sketch, "E12.2.1.55", {"start": v(-3.62, 3.98) * mm, "end": v(-3.6, 4) * mm});
            skLineSegment(sketch, "E12.2.1.56", {"start": v(-3.62, 3.98) * mm, "end": v(-3.6, 3.96) * mm});
            skLineSegment(sketch, "E12.2.1.57", {"start": v(-3.62, 3.5) * mm, "end": v(-3.6, 3.51) * mm});
            skLineSegment(sketch, "E12.2.1.58", {"start": v(-3.6, 3.48) * mm, "end": v(-3.59, 3.5) * mm});
            skLineSegment(sketch, "E12.2.1.59", {"start": v(-3.6, 3.32) * mm, "end": v(-3.59, 3.33) * mm});
            skLineSegment(sketch, "E12.3.0.0", {"start": v(-3.37, 1.53) * mm, "end": v(-3.47, 1.63) * mm});
            skLineSegment(sketch, "E12.3.0.1", {"start": v(-3.37, 1.2) * mm, "end": v(-3.47, 1.3) * mm});
            skPoint(sketch, "E12.3.0.2", {"position": v(-3.41, 1.99) * mm});
            skLineSegment(sketch, "E12.3.0.3", {"start": v(-3.35, 2.03) * mm, "end": v(-3.45, 2.13) * mm});
            skPoint(sketch, "E12.3.0.4", {"position": v(-3.5, 1.34) * mm});
            skLineSegment(sketch, "E12.3.0.5", {"start": v(-3.37, 2.01) * mm, "end": v(-3.47, 2.1) * mm});
            skPoint(sketch, "E12.3.0.6", {"position": v(-3.5, 1.5) * mm});
            skPoint(sketch, "E12.3.0.7", {"position": v(-3.5, 1.83) * mm});
            skPoint(sketch, "E12.3.0.8", {"position": v(-3.41, 1.34) * mm});
            skPoint(sketch, "E12.3.0.9", {"position": v(-3.41, 1.67) * mm});
            skLineSegment(sketch, "E12.3.0.10", {"start": v(-3.37, 1.36) * mm, "end": v(-3.47, 1.46) * mm});
            skPoint(sketch, "E12.3.0.11", {"position": v(-3.41, 1.5) * mm});
            skPoint(sketch, "E12.3.0.12", {"position": v(-3.41, 1.18) * mm});
            skLineSegment(sketch, "E12.3.0.13", {"start": v(-3.37, 1.69) * mm, "end": v(-3.47, 1.79) * mm});
            skPoint(sketch, "E12.3.0.14", {"position": v(-3.5, 1.99) * mm});
            skPoint(sketch, "E12.3.0.15", {"position": v(-3.5, 1.67) * mm});
            skLineSegment(sketch, "E12.3.0.16", {"start": v(-3.37, 1.85) * mm, "end": v(-3.47, 1.95) * mm});
            skPoint(sketch, "E12.3.0.17", {"position": v(-3.5, 1.18) * mm});
            skPoint(sketch, "E12.3.0.18", {"position": v(-3.41, 1.83) * mm});
            skLineSegment(sketch, "E12.3.0.19", {"start": v(-3.35, 1.38) * mm, "end": v(-3.45, 1.48) * mm});
            skLineSegment(sketch, "E12.3.0.20", {"start": v(-3.47, 1.95) * mm, "end": v(-3.37, 2.05) * mm});
            skLineSegment(sketch, "E12.3.0.21", {"start": v(-3.45, 1.77) * mm, "end": v(-3.35, 1.87) * mm});
            skLineSegment(sketch, "E12.3.0.22", {"start": v(-3.35, 1.54) * mm, "end": v(-3.45, 1.64) * mm});
            skLineSegment(sketch, "E12.3.0.23", {"start": v(-3.45, 1.28) * mm, "end": v(-3.35, 1.38) * mm});
            skLineSegment(sketch, "E12.3.0.24", {"start": v(-3.45, 1.6) * mm, "end": v(-3.35, 1.7) * mm});
            skLineSegment(sketch, "E12.3.0.25", {"start": v(-3.47, 1.46) * mm, "end": v(-3.37, 1.56) * mm});
            skLineSegment(sketch, "E12.3.0.26", {"start": v(-3.47, 1.14) * mm, "end": v(-3.37, 1.24) * mm});
            skLineSegment(sketch, "E12.3.0.27", {"start": v(-3.45, 1.45) * mm, "end": v(-3.35, 1.54) * mm});
            skLineSegment(sketch, "E12.3.0.28", {"start": v(-3.47, 1.3) * mm, "end": v(-3.37, 1.4) * mm});
            skLineSegment(sketch, "E12.3.0.29", {"start": v(-3.45, 1.12) * mm, "end": v(-3.35, 1.22) * mm});
            skLineSegment(sketch, "E12.3.0.30", {"start": v(-3.47, 1.63) * mm, "end": v(-3.37, 1.72) * mm});
            skLineSegment(sketch, "E12.3.0.31", {"start": v(-3.47, 1.79) * mm, "end": v(-3.37, 1.89) * mm});
            skLineSegment(sketch, "E12.3.0.32", {"start": v(-3.45, 1.93) * mm, "end": v(-3.35, 2.03) * mm});
            skLineSegment(sketch, "E12.3.0.33", {"start": v(-3.47, 2.1) * mm, "end": v(-3.45, 2.13) * mm});
            skLineSegment(sketch, "E12.3.0.34", {"start": v(-3.35, 1.7) * mm, "end": v(-3.45, 1.8) * mm});
            skLineSegment(sketch, "E12.3.0.35", {"start": v(-3.35, 1.22) * mm, "end": v(-3.45, 1.32) * mm});
            skLineSegment(sketch, "E12.3.0.36", {"start": v(-3.35, 1.87) * mm, "end": v(-3.45, 1.97) * mm});
            skLineSegment(sketch, "E12.3.0.37", {"start": v(-3.37, 1.89) * mm, "end": v(-3.35, 1.87) * mm});
            skLineSegment(sketch, "E12.3.0.38", {"start": v(-3.37, 1.56) * mm, "end": v(-3.35, 1.54) * mm});
            skLineSegment(sketch, "E12.3.0.39", {"start": v(-3.37, 1.24) * mm, "end": v(-3.35, 1.22) * mm});
            skLineSegment(sketch, "E12.3.0.40", {"start": v(-3.37, 1.72) * mm, "end": v(-3.35, 1.7) * mm});
            skLineSegment(sketch, "E12.3.0.41", {"start": v(-3.37, 1.4) * mm, "end": v(-3.35, 1.38) * mm});
            skLineSegment(sketch, "E12.3.0.42", {"start": v(-3.37, 2.05) * mm, "end": v(-3.35, 2.03) * mm});
            skLineSegment(sketch, "E12.3.0.43", {"start": v(-3.47, 1.79) * mm, "end": v(-3.45, 1.8) * mm});
            skLineSegment(sketch, "E12.3.0.44", {"start": v(-3.47, 1.79) * mm, "end": v(-3.45, 1.77) * mm});
            skLineSegment(sketch, "E12.3.0.45", {"start": v(-3.47, 1.14) * mm, "end": v(-3.45, 1.12) * mm});
            skLineSegment(sketch, "E12.3.0.46", {"start": v(-3.45, 1.77) * mm, "end": v(-3.43, 1.79) * mm});
            skLineSegment(sketch, "E12.3.0.47", {"start": v(-3.45, 1.12) * mm, "end": v(-3.43, 1.14) * mm});
            skLineSegment(sketch, "E12.3.0.48", {"start": v(-3.45, 1.93) * mm, "end": v(-3.43, 1.95) * mm});
            skLineSegment(sketch, "E12.3.0.49", {"start": v(-3.47, 1.3) * mm, "end": v(-3.45, 1.28) * mm});
            skLineSegment(sketch, "E12.3.0.50", {"start": v(-3.47, 1.63) * mm, "end": v(-3.45, 1.6) * mm});
            skLineSegment(sketch, "E12.3.0.51", {"start": v(-3.45, 1.6) * mm, "end": v(-3.43, 1.62) * mm});
            skLineSegment(sketch, "E12.3.0.52", {"start": v(-3.47, 1.46) * mm, "end": v(-3.45, 1.45) * mm});
            skLineSegment(sketch, "E12.3.0.53", {"start": v(-3.47, 1.63) * mm, "end": v(-3.45, 1.64) * mm});
            skLineSegment(sketch, "E12.3.0.54", {"start": v(-3.47, 1.3) * mm, "end": v(-3.45, 1.32) * mm});
            skLineSegment(sketch, "E12.3.0.55", {"start": v(-3.47, 1.95) * mm, "end": v(-3.45, 1.97) * mm});
            skLineSegment(sketch, "E12.3.0.56", {"start": v(-3.47, 1.95) * mm, "end": v(-3.45, 1.93) * mm});
            skLineSegment(sketch, "E12.3.0.57", {"start": v(-3.47, 1.46) * mm, "end": v(-3.45, 1.48) * mm});
            skLineSegment(sketch, "E12.3.0.58", {"start": v(-3.45, 1.45) * mm, "end": v(-3.43, 1.46) * mm});
            skLineSegment(sketch, "E12.3.0.59", {"start": v(-3.45, 1.28) * mm, "end": v(-3.43, 1.3) * mm});
            skLineSegment(sketch, "E12.3.1.0", {"start": v(-3.37, 3.56) * mm, "end": v(-3.47, 3.66) * mm});
            skLineSegment(sketch, "E12.3.1.1", {"start": v(-3.37, 3.24) * mm, "end": v(-3.47, 3.33) * mm});
            skPoint(sketch, "E12.3.1.2", {"position": v(-3.41, 4.02) * mm});
            skLineSegment(sketch, "E12.3.1.3", {"start": v(-3.35, 4.06) * mm, "end": v(-3.45, 4.16) * mm});
            skPoint(sketch, "E12.3.1.4", {"position": v(-3.5, 3.37) * mm});
            skLineSegment(sketch, "E12.3.1.5", {"start": v(-3.37, 4.04) * mm, "end": v(-3.47, 4.14) * mm});
            skPoint(sketch, "E12.3.1.6", {"position": v(-3.5, 3.54) * mm});
            skPoint(sketch, "E12.3.1.7", {"position": v(-3.5, 3.86) * mm});
            skPoint(sketch, "E12.3.1.8", {"position": v(-3.41, 3.37) * mm});
            skPoint(sketch, "E12.3.1.9", {"position": v(-3.41, 3.7) * mm});
            skLineSegment(sketch, "E12.3.1.10", {"start": v(-3.37, 3.4) * mm, "end": v(-3.47, 3.5) * mm});
            skPoint(sketch, "E12.3.1.11", {"position": v(-3.41, 3.54) * mm});
            skPoint(sketch, "E12.3.1.12", {"position": v(-3.41, 3.21) * mm});
            skLineSegment(sketch, "E12.3.1.13", {"start": v(-3.37, 3.72) * mm, "end": v(-3.47, 3.82) * mm});
            skPoint(sketch, "E12.3.1.14", {"position": v(-3.5, 4.02) * mm});
            skPoint(sketch, "E12.3.1.15", {"position": v(-3.5, 3.7) * mm});
            skLineSegment(sketch, "E12.3.1.16", {"start": v(-3.37, 3.88) * mm, "end": v(-3.47, 3.98) * mm});
            skPoint(sketch, "E12.3.1.17", {"position": v(-3.5, 3.21) * mm});
            skPoint(sketch, "E12.3.1.18", {"position": v(-3.41, 3.86) * mm});
            skLineSegment(sketch, "E12.3.1.19", {"start": v(-3.35, 3.41) * mm, "end": v(-3.45, 3.51) * mm});
            skLineSegment(sketch, "E12.3.1.20", {"start": v(-3.47, 3.98) * mm, "end": v(-3.37, 4.08) * mm});
            skLineSegment(sketch, "E12.3.1.21", {"start": v(-3.45, 3.8) * mm, "end": v(-3.35, 3.9) * mm});
            skLineSegment(sketch, "E12.3.1.22", {"start": v(-3.35, 3.58) * mm, "end": v(-3.45, 3.68) * mm});
            skLineSegment(sketch, "E12.3.1.23", {"start": v(-3.45, 3.32) * mm, "end": v(-3.35, 3.41) * mm});
            skLineSegment(sketch, "E12.3.1.24", {"start": v(-3.45, 3.64) * mm, "end": v(-3.35, 3.74) * mm});
            skLineSegment(sketch, "E12.3.1.25", {"start": v(-3.47, 3.5) * mm, "end": v(-3.37, 3.6) * mm});
            skLineSegment(sketch, "E12.3.1.26", {"start": v(-3.47, 3.17) * mm, "end": v(-3.37, 3.27) * mm});
            skLineSegment(sketch, "E12.3.1.27", {"start": v(-3.45, 3.48) * mm, "end": v(-3.35, 3.58) * mm});
            skLineSegment(sketch, "E12.3.1.28", {"start": v(-3.47, 3.33) * mm, "end": v(-3.37, 3.43) * mm});
            skLineSegment(sketch, "E12.3.1.29", {"start": v(-3.45, 3.15) * mm, "end": v(-3.35, 3.25) * mm});
            skLineSegment(sketch, "E12.3.1.30", {"start": v(-3.47, 3.66) * mm, "end": v(-3.37, 3.76) * mm});
            skLineSegment(sketch, "E12.3.1.31", {"start": v(-3.47, 3.82) * mm, "end": v(-3.37, 3.92) * mm});
            skLineSegment(sketch, "E12.3.1.32", {"start": v(-3.45, 3.96) * mm, "end": v(-3.35, 4.06) * mm});
            skLineSegment(sketch, "E12.3.1.33", {"start": v(-3.47, 4.14) * mm, "end": v(-3.45, 4.16) * mm});
            skLineSegment(sketch, "E12.3.1.34", {"start": v(-3.35, 3.74) * mm, "end": v(-3.45, 3.84) * mm});
            skLineSegment(sketch, "E12.3.1.35", {"start": v(-3.35, 3.25) * mm, "end": v(-3.45, 3.35) * mm});
            skLineSegment(sketch, "E12.3.1.36", {"start": v(-3.35, 3.9) * mm, "end": v(-3.45, 4) * mm});
            skLineSegment(sketch, "E12.3.1.37", {"start": v(-3.37, 3.92) * mm, "end": v(-3.35, 3.9) * mm});
            skLineSegment(sketch, "E12.3.1.38", {"start": v(-3.37, 3.6) * mm, "end": v(-3.35, 3.58) * mm});
            skLineSegment(sketch, "E12.3.1.39", {"start": v(-3.37, 3.27) * mm, "end": v(-3.35, 3.25) * mm});
            skLineSegment(sketch, "E12.3.1.40", {"start": v(-3.37, 3.76) * mm, "end": v(-3.35, 3.74) * mm});
            skLineSegment(sketch, "E12.3.1.41", {"start": v(-3.37, 3.43) * mm, "end": v(-3.35, 3.41) * mm});
            skLineSegment(sketch, "E12.3.1.42", {"start": v(-3.37, 4.08) * mm, "end": v(-3.35, 4.06) * mm});
            skLineSegment(sketch, "E12.3.1.43", {"start": v(-3.47, 3.82) * mm, "end": v(-3.45, 3.84) * mm});
            skLineSegment(sketch, "E12.3.1.44", {"start": v(-3.47, 3.82) * mm, "end": v(-3.45, 3.8) * mm});
            skLineSegment(sketch, "E12.3.1.45", {"start": v(-3.47, 3.17) * mm, "end": v(-3.45, 3.15) * mm});
            skLineSegment(sketch, "E12.3.1.46", {"start": v(-3.45, 3.8) * mm, "end": v(-3.43, 3.82) * mm});
            skLineSegment(sketch, "E12.3.1.47", {"start": v(-3.45, 3.15) * mm, "end": v(-3.43, 3.17) * mm});
            skLineSegment(sketch, "E12.3.1.48", {"start": v(-3.45, 3.96) * mm, "end": v(-3.43, 3.98) * mm});
            skLineSegment(sketch, "E12.3.1.49", {"start": v(-3.47, 3.33) * mm, "end": v(-3.45, 3.32) * mm});
            skLineSegment(sketch, "E12.3.1.50", {"start": v(-3.47, 3.66) * mm, "end": v(-3.45, 3.64) * mm});
            skLineSegment(sketch, "E12.3.1.51", {"start": v(-3.45, 3.64) * mm, "end": v(-3.43, 3.66) * mm});
            skLineSegment(sketch, "E12.3.1.52", {"start": v(-3.47, 3.5) * mm, "end": v(-3.45, 3.48) * mm});
            skLineSegment(sketch, "E12.3.1.53", {"start": v(-3.47, 3.66) * mm, "end": v(-3.45, 3.68) * mm});
            skLineSegment(sketch, "E12.3.1.54", {"start": v(-3.47, 3.33) * mm, "end": v(-3.45, 3.35) * mm});
            skLineSegment(sketch, "E12.3.1.55", {"start": v(-3.47, 3.98) * mm, "end": v(-3.45, 4) * mm});
            skLineSegment(sketch, "E12.3.1.56", {"start": v(-3.47, 3.98) * mm, "end": v(-3.45, 3.96) * mm});
            skLineSegment(sketch, "E12.3.1.57", {"start": v(-3.47, 3.5) * mm, "end": v(-3.45, 3.51) * mm});
            skLineSegment(sketch, "E12.3.1.58", {"start": v(-3.45, 3.48) * mm, "end": v(-3.43, 3.5) * mm});
            skLineSegment(sketch, "E12.3.1.59", {"start": v(-3.45, 3.32) * mm, "end": v(-3.43, 3.33) * mm});
            skLineSegment(sketch, "E12.4.0.0", {"start": v(-3.22, 1.53) * mm, "end": v(-3.32, 1.63) * mm});
            skLineSegment(sketch, "E12.4.0.1", {"start": v(-3.22, 1.2) * mm, "end": v(-3.32, 1.3) * mm});
            skPoint(sketch, "E12.4.0.2", {"position": v(-3.26, 1.99) * mm});
            skLineSegment(sketch, "E12.4.0.3", {"start": v(-3.2, 2.03) * mm, "end": v(-3.3, 2.13) * mm});
            skPoint(sketch, "E12.4.0.4", {"position": v(-3.34, 1.34) * mm});
            skLineSegment(sketch, "E12.4.0.5", {"start": v(-3.22, 2.01) * mm, "end": v(-3.32, 2.1) * mm});
            skPoint(sketch, "E12.4.0.6", {"position": v(-3.34, 1.5) * mm});
            skPoint(sketch, "E12.4.0.7", {"position": v(-3.34, 1.83) * mm});
            skPoint(sketch, "E12.4.0.8", {"position": v(-3.26, 1.34) * mm});
            skPoint(sketch, "E12.4.0.9", {"position": v(-3.26, 1.67) * mm});
            skLineSegment(sketch, "E12.4.0.10", {"start": v(-3.22, 1.36) * mm, "end": v(-3.32, 1.46) * mm});
            skPoint(sketch, "E12.4.0.11", {"position": v(-3.26, 1.5) * mm});
            skPoint(sketch, "E12.4.0.12", {"position": v(-3.26, 1.18) * mm});
            skLineSegment(sketch, "E12.4.0.13", {"start": v(-3.22, 1.69) * mm, "end": v(-3.32, 1.79) * mm});
            skPoint(sketch, "E12.4.0.14", {"position": v(-3.34, 1.99) * mm});
            skPoint(sketch, "E12.4.0.15", {"position": v(-3.34, 1.67) * mm});
            skLineSegment(sketch, "E12.4.0.16", {"start": v(-3.22, 1.85) * mm, "end": v(-3.32, 1.95) * mm});
            skPoint(sketch, "E12.4.0.17", {"position": v(-3.34, 1.18) * mm});
            skPoint(sketch, "E12.4.0.18", {"position": v(-3.26, 1.83) * mm});
            skLineSegment(sketch, "E12.4.0.19", {"start": v(-3.2, 1.38) * mm, "end": v(-3.3, 1.48) * mm});
            skLineSegment(sketch, "E12.4.0.20", {"start": v(-3.32, 1.95) * mm, "end": v(-3.22, 2.05) * mm});
            skLineSegment(sketch, "E12.4.0.21", {"start": v(-3.3, 1.77) * mm, "end": v(-3.2, 1.87) * mm});
            skLineSegment(sketch, "E12.4.0.22", {"start": v(-3.2, 1.54) * mm, "end": v(-3.3, 1.64) * mm});
            skLineSegment(sketch, "E12.4.0.23", {"start": v(-3.3, 1.28) * mm, "end": v(-3.2, 1.38) * mm});
            skLineSegment(sketch, "E12.4.0.24", {"start": v(-3.3, 1.6) * mm, "end": v(-3.2, 1.7) * mm});
            skLineSegment(sketch, "E12.4.0.25", {"start": v(-3.32, 1.46) * mm, "end": v(-3.22, 1.56) * mm});
            skLineSegment(sketch, "E12.4.0.26", {"start": v(-3.32, 1.14) * mm, "end": v(-3.22, 1.24) * mm});
            skLineSegment(sketch, "E12.4.0.27", {"start": v(-3.3, 1.45) * mm, "end": v(-3.2, 1.54) * mm});
            skLineSegment(sketch, "E12.4.0.28", {"start": v(-3.32, 1.3) * mm, "end": v(-3.22, 1.4) * mm});
            skLineSegment(sketch, "E12.4.0.29", {"start": v(-3.3, 1.12) * mm, "end": v(-3.2, 1.22) * mm});
            skLineSegment(sketch, "E12.4.0.30", {"start": v(-3.32, 1.63) * mm, "end": v(-3.22, 1.72) * mm});
            skLineSegment(sketch, "E12.4.0.31", {"start": v(-3.32, 1.79) * mm, "end": v(-3.22, 1.89) * mm});
            skLineSegment(sketch, "E12.4.0.32", {"start": v(-3.3, 1.93) * mm, "end": v(-3.2, 2.03) * mm});
            skLineSegment(sketch, "E12.4.0.33", {"start": v(-3.32, 2.1) * mm, "end": v(-3.3, 2.13) * mm});
            skLineSegment(sketch, "E12.4.0.34", {"start": v(-3.2, 1.7) * mm, "end": v(-3.3, 1.8) * mm});
            skLineSegment(sketch, "E12.4.0.35", {"start": v(-3.2, 1.22) * mm, "end": v(-3.3, 1.32) * mm});
            skLineSegment(sketch, "E12.4.0.36", {"start": v(-3.2, 1.87) * mm, "end": v(-3.3, 1.97) * mm});
            skLineSegment(sketch, "E12.4.0.37", {"start": v(-3.22, 1.89) * mm, "end": v(-3.2, 1.87) * mm});
            skLineSegment(sketch, "E12.4.0.38", {"start": v(-3.22, 1.56) * mm, "end": v(-3.2, 1.54) * mm});
            skLineSegment(sketch, "E12.4.0.39", {"start": v(-3.22, 1.24) * mm, "end": v(-3.2, 1.22) * mm});
            skLineSegment(sketch, "E12.4.0.40", {"start": v(-3.22, 1.72) * mm, "end": v(-3.2, 1.7) * mm});
            skLineSegment(sketch, "E12.4.0.41", {"start": v(-3.22, 1.4) * mm, "end": v(-3.2, 1.38) * mm});
            skLineSegment(sketch, "E12.4.0.42", {"start": v(-3.22, 2.05) * mm, "end": v(-3.2, 2.03) * mm});
            skLineSegment(sketch, "E12.4.0.43", {"start": v(-3.32, 1.79) * mm, "end": v(-3.3, 1.8) * mm});
            skLineSegment(sketch, "E12.4.0.44", {"start": v(-3.32, 1.79) * mm, "end": v(-3.3, 1.77) * mm});
            skLineSegment(sketch, "E12.4.0.45", {"start": v(-3.32, 1.14) * mm, "end": v(-3.3, 1.12) * mm});
            skLineSegment(sketch, "E12.4.0.46", {"start": v(-3.3, 1.77) * mm, "end": v(-3.28, 1.79) * mm});
            skLineSegment(sketch, "E12.4.0.47", {"start": v(-3.3, 1.12) * mm, "end": v(-3.28, 1.14) * mm});
            skLineSegment(sketch, "E12.4.0.48", {"start": v(-3.3, 1.93) * mm, "end": v(-3.28, 1.95) * mm});
            skLineSegment(sketch, "E12.4.0.49", {"start": v(-3.32, 1.3) * mm, "end": v(-3.3, 1.28) * mm});
            skLineSegment(sketch, "E12.4.0.50", {"start": v(-3.32, 1.63) * mm, "end": v(-3.3, 1.6) * mm});
            skLineSegment(sketch, "E12.4.0.51", {"start": v(-3.3, 1.6) * mm, "end": v(-3.28, 1.62) * mm});
            skLineSegment(sketch, "E12.4.0.52", {"start": v(-3.32, 1.46) * mm, "end": v(-3.3, 1.45) * mm});
            skLineSegment(sketch, "E12.4.0.53", {"start": v(-3.32, 1.63) * mm, "end": v(-3.3, 1.64) * mm});
            skLineSegment(sketch, "E12.4.0.54", {"start": v(-3.32, 1.3) * mm, "end": v(-3.3, 1.32) * mm});
            skLineSegment(sketch, "E12.4.0.55", {"start": v(-3.32, 1.95) * mm, "end": v(-3.3, 1.97) * mm});
            skLineSegment(sketch, "E12.4.0.56", {"start": v(-3.32, 1.95) * mm, "end": v(-3.3, 1.93) * mm});
            skLineSegment(sketch, "E12.4.0.57", {"start": v(-3.32, 1.46) * mm, "end": v(-3.3, 1.48) * mm});
            skLineSegment(sketch, "E12.4.0.58", {"start": v(-3.3, 1.45) * mm, "end": v(-3.28, 1.46) * mm});
            skLineSegment(sketch, "E12.4.0.59", {"start": v(-3.3, 1.28) * mm, "end": v(-3.28, 1.3) * mm});
            skLineSegment(sketch, "E12.4.1.0", {"start": v(-3.22, 3.56) * mm, "end": v(-3.32, 3.66) * mm});
            skLineSegment(sketch, "E12.4.1.1", {"start": v(-3.22, 3.24) * mm, "end": v(-3.32, 3.33) * mm});
            skPoint(sketch, "E12.4.1.2", {"position": v(-3.26, 4.02) * mm});
            skLineSegment(sketch, "E12.4.1.3", {"start": v(-3.2, 4.06) * mm, "end": v(-3.3, 4.16) * mm});
            skPoint(sketch, "E12.4.1.4", {"position": v(-3.34, 3.37) * mm});
            skLineSegment(sketch, "E12.4.1.5", {"start": v(-3.22, 4.04) * mm, "end": v(-3.32, 4.14) * mm});
            skPoint(sketch, "E12.4.1.6", {"position": v(-3.34, 3.54) * mm});
            skPoint(sketch, "E12.4.1.7", {"position": v(-3.34, 3.86) * mm});
            skPoint(sketch, "E12.4.1.8", {"position": v(-3.26, 3.37) * mm});
            skPoint(sketch, "E12.4.1.9", {"position": v(-3.26, 3.7) * mm});
            skLineSegment(sketch, "E12.4.1.10", {"start": v(-3.22, 3.4) * mm, "end": v(-3.32, 3.5) * mm});
            skPoint(sketch, "E12.4.1.11", {"position": v(-3.26, 3.54) * mm});
            skPoint(sketch, "E12.4.1.12", {"position": v(-3.26, 3.21) * mm});
            skLineSegment(sketch, "E12.4.1.13", {"start": v(-3.22, 3.72) * mm, "end": v(-3.32, 3.82) * mm});
            skPoint(sketch, "E12.4.1.14", {"position": v(-3.34, 4.02) * mm});
            skPoint(sketch, "E12.4.1.15", {"position": v(-3.34, 3.7) * mm});
            skLineSegment(sketch, "E12.4.1.16", {"start": v(-3.22, 3.88) * mm, "end": v(-3.32, 3.98) * mm});
            skPoint(sketch, "E12.4.1.17", {"position": v(-3.34, 3.21) * mm});
            skPoint(sketch, "E12.4.1.18", {"position": v(-3.26, 3.86) * mm});
            skLineSegment(sketch, "E12.4.1.19", {"start": v(-3.2, 3.41) * mm, "end": v(-3.3, 3.51) * mm});
            skLineSegment(sketch, "E12.4.1.20", {"start": v(-3.32, 3.98) * mm, "end": v(-3.22, 4.08) * mm});
            skLineSegment(sketch, "E12.4.1.21", {"start": v(-3.3, 3.8) * mm, "end": v(-3.2, 3.9) * mm});
            skLineSegment(sketch, "E12.4.1.22", {"start": v(-3.2, 3.58) * mm, "end": v(-3.3, 3.68) * mm});
            skLineSegment(sketch, "E12.4.1.23", {"start": v(-3.3, 3.32) * mm, "end": v(-3.2, 3.41) * mm});
            skLineSegment(sketch, "E12.4.1.24", {"start": v(-3.3, 3.64) * mm, "end": v(-3.2, 3.74) * mm});
            skLineSegment(sketch, "E12.4.1.25", {"start": v(-3.32, 3.5) * mm, "end": v(-3.22, 3.6) * mm});
            skLineSegment(sketch, "E12.4.1.26", {"start": v(-3.32, 3.17) * mm, "end": v(-3.22, 3.27) * mm});
            skLineSegment(sketch, "E12.4.1.27", {"start": v(-3.3, 3.48) * mm, "end": v(-3.2, 3.58) * mm});
            skLineSegment(sketch, "E12.4.1.28", {"start": v(-3.32, 3.33) * mm, "end": v(-3.22, 3.43) * mm});
            skLineSegment(sketch, "E12.4.1.29", {"start": v(-3.3, 3.15) * mm, "end": v(-3.2, 3.25) * mm});
            skLineSegment(sketch, "E12.4.1.30", {"start": v(-3.32, 3.66) * mm, "end": v(-3.22, 3.76) * mm});
            skLineSegment(sketch, "E12.4.1.31", {"start": v(-3.32, 3.82) * mm, "end": v(-3.22, 3.92) * mm});
            skLineSegment(sketch, "E12.4.1.32", {"start": v(-3.3, 3.96) * mm, "end": v(-3.2, 4.06) * mm});
            skLineSegment(sketch, "E12.4.1.33", {"start": v(-3.32, 4.14) * mm, "end": v(-3.3, 4.16) * mm});
            skLineSegment(sketch, "E12.4.1.34", {"start": v(-3.2, 3.74) * mm, "end": v(-3.3, 3.84) * mm});
            skLineSegment(sketch, "E12.4.1.35", {"start": v(-3.2, 3.25) * mm, "end": v(-3.3, 3.35) * mm});
            skLineSegment(sketch, "E12.4.1.36", {"start": v(-3.2, 3.9) * mm, "end": v(-3.3, 4) * mm});
            skLineSegment(sketch, "E12.4.1.37", {"start": v(-3.22, 3.92) * mm, "end": v(-3.2, 3.9) * mm});
            skLineSegment(sketch, "E12.4.1.38", {"start": v(-3.22, 3.6) * mm, "end": v(-3.2, 3.58) * mm});
            skLineSegment(sketch, "E12.4.1.39", {"start": v(-3.22, 3.27) * mm, "end": v(-3.2, 3.25) * mm});
            skLineSegment(sketch, "E12.4.1.40", {"start": v(-3.22, 3.76) * mm, "end": v(-3.2, 3.74) * mm});
            skLineSegment(sketch, "E12.4.1.41", {"start": v(-3.22, 3.43) * mm, "end": v(-3.2, 3.41) * mm});
            skLineSegment(sketch, "E12.4.1.42", {"start": v(-3.22, 4.08) * mm, "end": v(-3.2, 4.06) * mm});
            skLineSegment(sketch, "E12.4.1.43", {"start": v(-3.32, 3.82) * mm, "end": v(-3.3, 3.84) * mm});
            skLineSegment(sketch, "E12.4.1.44", {"start": v(-3.32, 3.82) * mm, "end": v(-3.3, 3.8) * mm});
            skLineSegment(sketch, "E12.4.1.45", {"start": v(-3.32, 3.17) * mm, "end": v(-3.3, 3.15) * mm});
            skLineSegment(sketch, "E12.4.1.46", {"start": v(-3.3, 3.8) * mm, "end": v(-3.28, 3.82) * mm});
            skLineSegment(sketch, "E12.4.1.47", {"start": v(-3.3, 3.15) * mm, "end": v(-3.28, 3.17) * mm});
            skLineSegment(sketch, "E12.4.1.48", {"start": v(-3.3, 3.96) * mm, "end": v(-3.28, 3.98) * mm});
            skLineSegment(sketch, "E12.4.1.49", {"start": v(-3.32, 3.33) * mm, "end": v(-3.3, 3.32) * mm});
            skLineSegment(sketch, "E12.4.1.50", {"start": v(-3.32, 3.66) * mm, "end": v(-3.3, 3.64) * mm});
            skLineSegment(sketch, "E12.4.1.51", {"start": v(-3.3, 3.64) * mm, "end": v(-3.28, 3.66) * mm});
            skLineSegment(sketch, "E12.4.1.52", {"start": v(-3.32, 3.5) * mm, "end": v(-3.3, 3.48) * mm});
            skLineSegment(sketch, "E12.4.1.53", {"start": v(-3.32, 3.66) * mm, "end": v(-3.3, 3.68) * mm});
            skLineSegment(sketch, "E12.4.1.54", {"start": v(-3.32, 3.33) * mm, "end": v(-3.3, 3.35) * mm});
            skLineSegment(sketch, "E12.4.1.55", {"start": v(-3.32, 3.98) * mm, "end": v(-3.3, 4) * mm});
            skLineSegment(sketch, "E12.4.1.56", {"start": v(-3.32, 3.98) * mm, "end": v(-3.3, 3.96) * mm});
            skLineSegment(sketch, "E12.4.1.57", {"start": v(-3.32, 3.5) * mm, "end": v(-3.3, 3.51) * mm});
            skLineSegment(sketch, "E12.4.1.58", {"start": v(-3.3, 3.48) * mm, "end": v(-3.28, 3.5) * mm});
            skLineSegment(sketch, "E12.4.1.59", {"start": v(-3.3, 3.32) * mm, "end": v(-3.28, 3.33) * mm});
            skLineSegment(sketch, "E12.5.0.0", {"start": v(-3.07, 1.53) * mm, "end": v(-3.17, 1.63) * mm});
            skLineSegment(sketch, "E12.5.0.1", {"start": v(-3.07, 1.2) * mm, "end": v(-3.17, 1.3) * mm});
            skPoint(sketch, "E12.5.0.2", {"position": v(-3.1, 1.99) * mm});
            skLineSegment(sketch, "E12.5.0.3", {"start": v(-3.05, 2.03) * mm, "end": v(-3.15, 2.13) * mm});
            skPoint(sketch, "E12.5.0.4", {"position": v(-3.19, 1.34) * mm});
            skLineSegment(sketch, "E12.5.0.5", {"start": v(-3.07, 2.01) * mm, "end": v(-3.17, 2.1) * mm});
            skPoint(sketch, "E12.5.0.6", {"position": v(-3.19, 1.5) * mm});
            skPoint(sketch, "E12.5.0.7", {"position": v(-3.19, 1.83) * mm});
            skPoint(sketch, "E12.5.0.8", {"position": v(-3.1, 1.34) * mm});
            skPoint(sketch, "E12.5.0.9", {"position": v(-3.1, 1.67) * mm});
            skLineSegment(sketch, "E12.5.0.10", {"start": v(-3.07, 1.36) * mm, "end": v(-3.17, 1.46) * mm});
            skPoint(sketch, "E12.5.0.11", {"position": v(-3.1, 1.5) * mm});
            skPoint(sketch, "E12.5.0.12", {"position": v(-3.1, 1.18) * mm});
            skLineSegment(sketch, "E12.5.0.13", {"start": v(-3.07, 1.69) * mm, "end": v(-3.17, 1.79) * mm});
            skPoint(sketch, "E12.5.0.14", {"position": v(-3.19, 1.99) * mm});
            skPoint(sketch, "E12.5.0.15", {"position": v(-3.19, 1.67) * mm});
            skLineSegment(sketch, "E12.5.0.16", {"start": v(-3.07, 1.85) * mm, "end": v(-3.17, 1.95) * mm});
            skPoint(sketch, "E12.5.0.17", {"position": v(-3.19, 1.18) * mm});
            skPoint(sketch, "E12.5.0.18", {"position": v(-3.1, 1.83) * mm});
            skLineSegment(sketch, "E12.5.0.19", {"start": v(-3.05, 1.38) * mm, "end": v(-3.15, 1.48) * mm});
            skLineSegment(sketch, "E12.5.0.20", {"start": v(-3.17, 1.95) * mm, "end": v(-3.07, 2.05) * mm});
            skLineSegment(sketch, "E12.5.0.21", {"start": v(-3.15, 1.77) * mm, "end": v(-3.05, 1.87) * mm});
            skLineSegment(sketch, "E12.5.0.22", {"start": v(-3.05, 1.54) * mm, "end": v(-3.15, 1.64) * mm});
            skLineSegment(sketch, "E12.5.0.23", {"start": v(-3.15, 1.28) * mm, "end": v(-3.05, 1.38) * mm});
            skLineSegment(sketch, "E12.5.0.24", {"start": v(-3.15, 1.6) * mm, "end": v(-3.05, 1.7) * mm});
            skLineSegment(sketch, "E12.5.0.25", {"start": v(-3.17, 1.46) * mm, "end": v(-3.07, 1.56) * mm});
            skLineSegment(sketch, "E12.5.0.26", {"start": v(-3.17, 1.14) * mm, "end": v(-3.07, 1.24) * mm});
            skLineSegment(sketch, "E12.5.0.27", {"start": v(-3.15, 1.45) * mm, "end": v(-3.05, 1.54) * mm});
            skLineSegment(sketch, "E12.5.0.28", {"start": v(-3.17, 1.3) * mm, "end": v(-3.07, 1.4) * mm});
            skLineSegment(sketch, "E12.5.0.29", {"start": v(-3.15, 1.12) * mm, "end": v(-3.05, 1.22) * mm});
            skLineSegment(sketch, "E12.5.0.30", {"start": v(-3.17, 1.63) * mm, "end": v(-3.07, 1.72) * mm});
            skLineSegment(sketch, "E12.5.0.31", {"start": v(-3.17, 1.79) * mm, "end": v(-3.07, 1.89) * mm});
            skLineSegment(sketch, "E12.5.0.32", {"start": v(-3.15, 1.93) * mm, "end": v(-3.05, 2.03) * mm});
            skLineSegment(sketch, "E12.5.0.33", {"start": v(-3.17, 2.1) * mm, "end": v(-3.15, 2.13) * mm});
            skLineSegment(sketch, "E12.5.0.34", {"start": v(-3.05, 1.7) * mm, "end": v(-3.15, 1.8) * mm});
            skLineSegment(sketch, "E12.5.0.35", {"start": v(-3.05, 1.22) * mm, "end": v(-3.15, 1.32) * mm});
            skLineSegment(sketch, "E12.5.0.36", {"start": v(-3.05, 1.87) * mm, "end": v(-3.15, 1.97) * mm});
            skLineSegment(sketch, "E12.5.0.37", {"start": v(-3.07, 1.89) * mm, "end": v(-3.05, 1.87) * mm});
            skLineSegment(sketch, "E12.5.0.38", {"start": v(-3.07, 1.56) * mm, "end": v(-3.05, 1.54) * mm});
            skLineSegment(sketch, "E12.5.0.39", {"start": v(-3.07, 1.24) * mm, "end": v(-3.05, 1.22) * mm});
            skLineSegment(sketch, "E12.5.0.40", {"start": v(-3.07, 1.72) * mm, "end": v(-3.05, 1.7) * mm});
            skLineSegment(sketch, "E12.5.0.41", {"start": v(-3.07, 1.4) * mm, "end": v(-3.05, 1.38) * mm});
            skLineSegment(sketch, "E12.5.0.42", {"start": v(-3.07, 2.05) * mm, "end": v(-3.05, 2.03) * mm});
            skLineSegment(sketch, "E12.5.0.43", {"start": v(-3.17, 1.79) * mm, "end": v(-3.15, 1.8) * mm});
            skLineSegment(sketch, "E12.5.0.44", {"start": v(-3.17, 1.79) * mm, "end": v(-3.15, 1.77) * mm});
            skLineSegment(sketch, "E12.5.0.45", {"start": v(-3.17, 1.14) * mm, "end": v(-3.15, 1.12) * mm});
            skLineSegment(sketch, "E12.5.0.46", {"start": v(-3.15, 1.77) * mm, "end": v(-3.13, 1.79) * mm});
            skLineSegment(sketch, "E12.5.0.47", {"start": v(-3.15, 1.12) * mm, "end": v(-3.13, 1.14) * mm});
            skLineSegment(sketch, "E12.5.0.48", {"start": v(-3.15, 1.93) * mm, "end": v(-3.13, 1.95) * mm});
            skLineSegment(sketch, "E12.5.0.49", {"start": v(-3.17, 1.3) * mm, "end": v(-3.15, 1.28) * mm});
            skLineSegment(sketch, "E12.5.0.50", {"start": v(-3.17, 1.63) * mm, "end": v(-3.15, 1.6) * mm});
            skLineSegment(sketch, "E12.5.0.51", {"start": v(-3.15, 1.6) * mm, "end": v(-3.13, 1.62) * mm});
            skLineSegment(sketch, "E12.5.0.52", {"start": v(-3.17, 1.46) * mm, "end": v(-3.15, 1.45) * mm});
            skLineSegment(sketch, "E12.5.0.53", {"start": v(-3.17, 1.63) * mm, "end": v(-3.15, 1.64) * mm});
            skLineSegment(sketch, "E12.5.0.54", {"start": v(-3.17, 1.3) * mm, "end": v(-3.15, 1.32) * mm});
            skLineSegment(sketch, "E12.5.0.55", {"start": v(-3.17, 1.95) * mm, "end": v(-3.15, 1.97) * mm});
            skLineSegment(sketch, "E12.5.0.56", {"start": v(-3.17, 1.95) * mm, "end": v(-3.15, 1.93) * mm});
            skLineSegment(sketch, "E12.5.0.57", {"start": v(-3.17, 1.46) * mm, "end": v(-3.15, 1.48) * mm});
            skLineSegment(sketch, "E12.5.0.58", {"start": v(-3.15, 1.45) * mm, "end": v(-3.13, 1.46) * mm});
            skLineSegment(sketch, "E12.5.0.59", {"start": v(-3.15, 1.28) * mm, "end": v(-3.13, 1.3) * mm});
            skLineSegment(sketch, "E12.5.1.0", {"start": v(-3.07, 3.56) * mm, "end": v(-3.17, 3.66) * mm});
            skLineSegment(sketch, "E12.5.1.1", {"start": v(-3.07, 3.24) * mm, "end": v(-3.17, 3.33) * mm});
            skPoint(sketch, "E12.5.1.2", {"position": v(-3.1, 4.02) * mm});
            skLineSegment(sketch, "E12.5.1.3", {"start": v(-3.05, 4.06) * mm, "end": v(-3.15, 4.16) * mm});
            skPoint(sketch, "E12.5.1.4", {"position": v(-3.19, 3.37) * mm});
            skLineSegment(sketch, "E12.5.1.5", {"start": v(-3.07, 4.04) * mm, "end": v(-3.17, 4.14) * mm});
            skPoint(sketch, "E12.5.1.6", {"position": v(-3.19, 3.54) * mm});
            skPoint(sketch, "E12.5.1.7", {"position": v(-3.19, 3.86) * mm});
            skPoint(sketch, "E12.5.1.8", {"position": v(-3.1, 3.37) * mm});
            skPoint(sketch, "E12.5.1.9", {"position": v(-3.1, 3.7) * mm});
            skLineSegment(sketch, "E12.5.1.10", {"start": v(-3.07, 3.4) * mm, "end": v(-3.17, 3.5) * mm});
            skPoint(sketch, "E12.5.1.11", {"position": v(-3.1, 3.54) * mm});
            skPoint(sketch, "E12.5.1.12", {"position": v(-3.1, 3.21) * mm});
            skLineSegment(sketch, "E12.5.1.13", {"start": v(-3.07, 3.72) * mm, "end": v(-3.17, 3.82) * mm});
            skPoint(sketch, "E12.5.1.14", {"position": v(-3.19, 4.02) * mm});
            skPoint(sketch, "E12.5.1.15", {"position": v(-3.19, 3.7) * mm});
            skLineSegment(sketch, "E12.5.1.16", {"start": v(-3.07, 3.88) * mm, "end": v(-3.17, 3.98) * mm});
            skPoint(sketch, "E12.5.1.17", {"position": v(-3.19, 3.21) * mm});
            skPoint(sketch, "E12.5.1.18", {"position": v(-3.1, 3.86) * mm});
            skLineSegment(sketch, "E12.5.1.19", {"start": v(-3.05, 3.41) * mm, "end": v(-3.15, 3.51) * mm});
            skLineSegment(sketch, "E12.5.1.20", {"start": v(-3.17, 3.98) * mm, "end": v(-3.07, 4.08) * mm});
            skLineSegment(sketch, "E12.5.1.21", {"start": v(-3.15, 3.8) * mm, "end": v(-3.05, 3.9) * mm});
            skLineSegment(sketch, "E12.5.1.22", {"start": v(-3.05, 3.58) * mm, "end": v(-3.15, 3.68) * mm});
            skLineSegment(sketch, "E12.5.1.23", {"start": v(-3.15, 3.32) * mm, "end": v(-3.05, 3.41) * mm});
            skLineSegment(sketch, "E12.5.1.24", {"start": v(-3.15, 3.64) * mm, "end": v(-3.05, 3.74) * mm});
            skLineSegment(sketch, "E12.5.1.25", {"start": v(-3.17, 3.5) * mm, "end": v(-3.07, 3.6) * mm});
            skLineSegment(sketch, "E12.5.1.26", {"start": v(-3.17, 3.17) * mm, "end": v(-3.07, 3.27) * mm});
            skLineSegment(sketch, "E12.5.1.27", {"start": v(-3.15, 3.48) * mm, "end": v(-3.05, 3.58) * mm});
            skLineSegment(sketch, "E12.5.1.28", {"start": v(-3.17, 3.33) * mm, "end": v(-3.07, 3.43) * mm});
            skLineSegment(sketch, "E12.5.1.29", {"start": v(-3.15, 3.15) * mm, "end": v(-3.05, 3.25) * mm});
            skLineSegment(sketch, "E12.5.1.30", {"start": v(-3.17, 3.66) * mm, "end": v(-3.07, 3.76) * mm});
            skLineSegment(sketch, "E12.5.1.31", {"start": v(-3.17, 3.82) * mm, "end": v(-3.07, 3.92) * mm});
            skLineSegment(sketch, "E12.5.1.32", {"start": v(-3.15, 3.96) * mm, "end": v(-3.05, 4.06) * mm});
            skLineSegment(sketch, "E12.5.1.33", {"start": v(-3.17, 4.14) * mm, "end": v(-3.15, 4.16) * mm});
            skLineSegment(sketch, "E12.5.1.34", {"start": v(-3.05, 3.74) * mm, "end": v(-3.15, 3.84) * mm});
            skLineSegment(sketch, "E12.5.1.35", {"start": v(-3.05, 3.25) * mm, "end": v(-3.15, 3.35) * mm});
            skLineSegment(sketch, "E12.5.1.36", {"start": v(-3.05, 3.9) * mm, "end": v(-3.15, 4) * mm});
            skLineSegment(sketch, "E12.5.1.37", {"start": v(-3.07, 3.92) * mm, "end": v(-3.05, 3.9) * mm});
            skLineSegment(sketch, "E12.5.1.38", {"start": v(-3.07, 3.6) * mm, "end": v(-3.05, 3.58) * mm});
            skLineSegment(sketch, "E12.5.1.39", {"start": v(-3.07, 3.27) * mm, "end": v(-3.05, 3.25) * mm});
            skLineSegment(sketch, "E12.5.1.40", {"start": v(-3.07, 3.76) * mm, "end": v(-3.05, 3.74) * mm});
            skLineSegment(sketch, "E12.5.1.41", {"start": v(-3.07, 3.43) * mm, "end": v(-3.05, 3.41) * mm});
            skLineSegment(sketch, "E12.5.1.42", {"start": v(-3.07, 4.08) * mm, "end": v(-3.05, 4.06) * mm});
            skLineSegment(sketch, "E12.5.1.43", {"start": v(-3.17, 3.82) * mm, "end": v(-3.15, 3.84) * mm});
            skLineSegment(sketch, "E12.5.1.44", {"start": v(-3.17, 3.82) * mm, "end": v(-3.15, 3.8) * mm});
            skLineSegment(sketch, "E12.5.1.45", {"start": v(-3.17, 3.17) * mm, "end": v(-3.15, 3.15) * mm});
            skLineSegment(sketch, "E12.5.1.46", {"start": v(-3.15, 3.8) * mm, "end": v(-3.13, 3.82) * mm});
            skLineSegment(sketch, "E12.5.1.47", {"start": v(-3.15, 3.15) * mm, "end": v(-3.13, 3.17) * mm});
            skLineSegment(sketch, "E12.5.1.48", {"start": v(-3.15, 3.96) * mm, "end": v(-3.13, 3.98) * mm});
            skLineSegment(sketch, "E12.5.1.49", {"start": v(-3.17, 3.33) * mm, "end": v(-3.15, 3.32) * mm});
            skLineSegment(sketch, "E12.5.1.50", {"start": v(-3.17, 3.66) * mm, "end": v(-3.15, 3.64) * mm});
            skLineSegment(sketch, "E12.5.1.51", {"start": v(-3.15, 3.64) * mm, "end": v(-3.13, 3.66) * mm});
            skLineSegment(sketch, "E12.5.1.52", {"start": v(-3.17, 3.5) * mm, "end": v(-3.15, 3.48) * mm});
            skLineSegment(sketch, "E12.5.1.53", {"start": v(-3.17, 3.66) * mm, "end": v(-3.15, 3.68) * mm});
            skLineSegment(sketch, "E12.5.1.54", {"start": v(-3.17, 3.33) * mm, "end": v(-3.15, 3.35) * mm});
            skLineSegment(sketch, "E12.5.1.55", {"start": v(-3.17, 3.98) * mm, "end": v(-3.15, 4) * mm});
            skLineSegment(sketch, "E12.5.1.56", {"start": v(-3.17, 3.98) * mm, "end": v(-3.15, 3.96) * mm});
            skLineSegment(sketch, "E12.5.1.57", {"start": v(-3.17, 3.5) * mm, "end": v(-3.15, 3.51) * mm});
            skLineSegment(sketch, "E12.5.1.58", {"start": v(-3.15, 3.48) * mm, "end": v(-3.13, 3.5) * mm});
            skLineSegment(sketch, "E12.5.1.59", {"start": v(-3.15, 3.32) * mm, "end": v(-3.13, 3.33) * mm});
            skLineSegment(sketch, "E12.6.0.0", {"start": v(-2.91, 1.53) * mm, "end": v(-3.01, 1.63) * mm});
            skLineSegment(sketch, "E12.6.0.1", {"start": v(-2.91, 1.2) * mm, "end": v(-3.01, 1.3) * mm});
            skPoint(sketch, "E12.6.0.2", {"position": v(-2.96, 1.99) * mm});
            skLineSegment(sketch, "E12.6.0.3", {"start": v(-2.9, 2.03) * mm, "end": v(-3, 2.13) * mm});
            skPoint(sketch, "E12.6.0.4", {"position": v(-3.04, 1.34) * mm});
            skLineSegment(sketch, "E12.6.0.5", {"start": v(-2.91, 2.01) * mm, "end": v(-3.01, 2.1) * mm});
            skPoint(sketch, "E12.6.0.6", {"position": v(-3.04, 1.5) * mm});
            skPoint(sketch, "E12.6.0.7", {"position": v(-3.04, 1.83) * mm});
            skPoint(sketch, "E12.6.0.8", {"position": v(-2.96, 1.34) * mm});
            skPoint(sketch, "E12.6.0.9", {"position": v(-2.96, 1.67) * mm});
            skLineSegment(sketch, "E12.6.0.10", {"start": v(-2.91, 1.36) * mm, "end": v(-3.01, 1.46) * mm});
            skPoint(sketch, "E12.6.0.11", {"position": v(-2.96, 1.5) * mm});
            skPoint(sketch, "E12.6.0.12", {"position": v(-2.96, 1.18) * mm});
            skLineSegment(sketch, "E12.6.0.13", {"start": v(-2.91, 1.69) * mm, "end": v(-3.01, 1.79) * mm});
            skPoint(sketch, "E12.6.0.14", {"position": v(-3.04, 1.99) * mm});
            skPoint(sketch, "E12.6.0.15", {"position": v(-3.04, 1.67) * mm});
            skLineSegment(sketch, "E12.6.0.16", {"start": v(-2.91, 1.85) * mm, "end": v(-3.01, 1.95) * mm});
            skPoint(sketch, "E12.6.0.17", {"position": v(-3.04, 1.18) * mm});
            skPoint(sketch, "E12.6.0.18", {"position": v(-2.96, 1.83) * mm});
            skLineSegment(sketch, "E12.6.0.19", {"start": v(-2.9, 1.38) * mm, "end": v(-3, 1.48) * mm});
            skLineSegment(sketch, "E12.6.0.20", {"start": v(-3.01, 1.95) * mm, "end": v(-2.91, 2.05) * mm});
            skLineSegment(sketch, "E12.6.0.21", {"start": v(-3, 1.77) * mm, "end": v(-2.9, 1.87) * mm});
            skLineSegment(sketch, "E12.6.0.22", {"start": v(-2.9, 1.54) * mm, "end": v(-3, 1.64) * mm});
            skLineSegment(sketch, "E12.6.0.23", {"start": v(-3, 1.28) * mm, "end": v(-2.9, 1.38) * mm});
            skLineSegment(sketch, "E12.6.0.24", {"start": v(-3, 1.6) * mm, "end": v(-2.9, 1.7) * mm});
            skLineSegment(sketch, "E12.6.0.25", {"start": v(-3.01, 1.46) * mm, "end": v(-2.91, 1.56) * mm});
            skLineSegment(sketch, "E12.6.0.26", {"start": v(-3.01, 1.14) * mm, "end": v(-2.91, 1.24) * mm});
            skLineSegment(sketch, "E12.6.0.27", {"start": v(-3, 1.45) * mm, "end": v(-2.9, 1.54) * mm});
            skLineSegment(sketch, "E12.6.0.28", {"start": v(-3.01, 1.3) * mm, "end": v(-2.91, 1.4) * mm});
            skLineSegment(sketch, "E12.6.0.29", {"start": v(-3, 1.12) * mm, "end": v(-2.9, 1.22) * mm});
            skLineSegment(sketch, "E12.6.0.30", {"start": v(-3.01, 1.63) * mm, "end": v(-2.91, 1.72) * mm});
            skLineSegment(sketch, "E12.6.0.31", {"start": v(-3.01, 1.79) * mm, "end": v(-2.91, 1.89) * mm});
            skLineSegment(sketch, "E12.6.0.32", {"start": v(-3, 1.93) * mm, "end": v(-2.9, 2.03) * mm});
            skLineSegment(sketch, "E12.6.0.33", {"start": v(-3.01, 2.1) * mm, "end": v(-3, 2.13) * mm});
            skLineSegment(sketch, "E12.6.0.34", {"start": v(-2.9, 1.7) * mm, "end": v(-3, 1.8) * mm});
            skLineSegment(sketch, "E12.6.0.35", {"start": v(-2.9, 1.22) * mm, "end": v(-3, 1.32) * mm});
            skLineSegment(sketch, "E12.6.0.36", {"start": v(-2.9, 1.87) * mm, "end": v(-3, 1.97) * mm});
            skLineSegment(sketch, "E12.6.0.37", {"start": v(-2.91, 1.89) * mm, "end": v(-2.9, 1.87) * mm});
            skLineSegment(sketch, "E12.6.0.38", {"start": v(-2.91, 1.56) * mm, "end": v(-2.9, 1.54) * mm});
            skLineSegment(sketch, "E12.6.0.39", {"start": v(-2.91, 1.24) * mm, "end": v(-2.9, 1.22) * mm});
            skLineSegment(sketch, "E12.6.0.40", {"start": v(-2.91, 1.72) * mm, "end": v(-2.9, 1.7) * mm});
            skLineSegment(sketch, "E12.6.0.41", {"start": v(-2.91, 1.4) * mm, "end": v(-2.9, 1.38) * mm});
            skLineSegment(sketch, "E12.6.0.42", {"start": v(-2.91, 2.05) * mm, "end": v(-2.9, 2.03) * mm});
            skLineSegment(sketch, "E12.6.0.43", {"start": v(-3.01, 1.79) * mm, "end": v(-3, 1.8) * mm});
            skLineSegment(sketch, "E12.6.0.44", {"start": v(-3.01, 1.79) * mm, "end": v(-3, 1.77) * mm});
            skLineSegment(sketch, "E12.6.0.45", {"start": v(-3.01, 1.14) * mm, "end": v(-3, 1.12) * mm});
            skLineSegment(sketch, "E12.6.0.46", {"start": v(-3, 1.77) * mm, "end": v(-2.98, 1.79) * mm});
            skLineSegment(sketch, "E12.6.0.47", {"start": v(-3, 1.12) * mm, "end": v(-2.98, 1.14) * mm});
            skLineSegment(sketch, "E12.6.0.48", {"start": v(-3, 1.93) * mm, "end": v(-2.98, 1.95) * mm});
            skLineSegment(sketch, "E12.6.0.49", {"start": v(-3.01, 1.3) * mm, "end": v(-3, 1.28) * mm});
            skLineSegment(sketch, "E12.6.0.50", {"start": v(-3.01, 1.63) * mm, "end": v(-3, 1.6) * mm});
            skLineSegment(sketch, "E12.6.0.51", {"start": v(-3, 1.6) * mm, "end": v(-2.98, 1.62) * mm});
            skLineSegment(sketch, "E12.6.0.52", {"start": v(-3.01, 1.46) * mm, "end": v(-3, 1.45) * mm});
            skLineSegment(sketch, "E12.6.0.53", {"start": v(-3.01, 1.63) * mm, "end": v(-3, 1.64) * mm});
            skLineSegment(sketch, "E12.6.0.54", {"start": v(-3.01, 1.3) * mm, "end": v(-3, 1.32) * mm});
            skLineSegment(sketch, "E12.6.0.55", {"start": v(-3.01, 1.95) * mm, "end": v(-3, 1.97) * mm});
            skLineSegment(sketch, "E12.6.0.56", {"start": v(-3.01, 1.95) * mm, "end": v(-3, 1.93) * mm});
            skLineSegment(sketch, "E12.6.0.57", {"start": v(-3.01, 1.46) * mm, "end": v(-3, 1.48) * mm});
            skLineSegment(sketch, "E12.6.0.58", {"start": v(-3, 1.45) * mm, "end": v(-2.98, 1.46) * mm});
            skLineSegment(sketch, "E12.6.0.59", {"start": v(-3, 1.28) * mm, "end": v(-2.98, 1.3) * mm});
            skLineSegment(sketch, "E12.6.1.0", {"start": v(-2.91, 3.56) * mm, "end": v(-3.01, 3.66) * mm});
            skLineSegment(sketch, "E12.6.1.1", {"start": v(-2.91, 3.24) * mm, "end": v(-3.01, 3.33) * mm});
            skPoint(sketch, "E12.6.1.2", {"position": v(-2.96, 4.02) * mm});
            skLineSegment(sketch, "E12.6.1.3", {"start": v(-2.9, 4.06) * mm, "end": v(-3, 4.16) * mm});
            skPoint(sketch, "E12.6.1.4", {"position": v(-3.04, 3.37) * mm});
            skLineSegment(sketch, "E12.6.1.5", {"start": v(-2.91, 4.04) * mm, "end": v(-3.01, 4.14) * mm});
            skPoint(sketch, "E12.6.1.6", {"position": v(-3.04, 3.54) * mm});
            skPoint(sketch, "E12.6.1.7", {"position": v(-3.04, 3.86) * mm});
            skPoint(sketch, "E12.6.1.8", {"position": v(-2.96, 3.37) * mm});
            skPoint(sketch, "E12.6.1.9", {"position": v(-2.96, 3.7) * mm});
            skLineSegment(sketch, "E12.6.1.10", {"start": v(-2.91, 3.4) * mm, "end": v(-3.01, 3.5) * mm});
            skPoint(sketch, "E12.6.1.11", {"position": v(-2.96, 3.54) * mm});
            skPoint(sketch, "E12.6.1.12", {"position": v(-2.96, 3.21) * mm});
            skLineSegment(sketch, "E12.6.1.13", {"start": v(-2.91, 3.72) * mm, "end": v(-3.01, 3.82) * mm});
            skPoint(sketch, "E12.6.1.14", {"position": v(-3.04, 4.02) * mm});
            skPoint(sketch, "E12.6.1.15", {"position": v(-3.04, 3.7) * mm});
            skLineSegment(sketch, "E12.6.1.16", {"start": v(-2.91, 3.88) * mm, "end": v(-3.01, 3.98) * mm});
            skPoint(sketch, "E12.6.1.17", {"position": v(-3.04, 3.21) * mm});
            skPoint(sketch, "E12.6.1.18", {"position": v(-2.96, 3.86) * mm});
            skLineSegment(sketch, "E12.6.1.19", {"start": v(-2.9, 3.41) * mm, "end": v(-3, 3.51) * mm});
            skLineSegment(sketch, "E12.6.1.20", {"start": v(-3.01, 3.98) * mm, "end": v(-2.91, 4.08) * mm});
            skLineSegment(sketch, "E12.6.1.21", {"start": v(-3, 3.8) * mm, "end": v(-2.9, 3.9) * mm});
            skLineSegment(sketch, "E12.6.1.22", {"start": v(-2.9, 3.58) * mm, "end": v(-3, 3.68) * mm});
            skLineSegment(sketch, "E12.6.1.23", {"start": v(-3, 3.32) * mm, "end": v(-2.9, 3.41) * mm});
            skLineSegment(sketch, "E12.6.1.24", {"start": v(-3, 3.64) * mm, "end": v(-2.9, 3.74) * mm});
            skLineSegment(sketch, "E12.6.1.25", {"start": v(-3.01, 3.5) * mm, "end": v(-2.91, 3.6) * mm});
            skLineSegment(sketch, "E12.6.1.26", {"start": v(-3.01, 3.17) * mm, "end": v(-2.91, 3.27) * mm});
            skLineSegment(sketch, "E12.6.1.27", {"start": v(-3, 3.48) * mm, "end": v(-2.9, 3.58) * mm});
            skLineSegment(sketch, "E12.6.1.28", {"start": v(-3.01, 3.33) * mm, "end": v(-2.91, 3.43) * mm});
            skLineSegment(sketch, "E12.6.1.29", {"start": v(-3, 3.15) * mm, "end": v(-2.9, 3.25) * mm});
            skLineSegment(sketch, "E12.6.1.30", {"start": v(-3.01, 3.66) * mm, "end": v(-2.91, 3.76) * mm});
            skLineSegment(sketch, "E12.6.1.31", {"start": v(-3.01, 3.82) * mm, "end": v(-2.91, 3.92) * mm});
            skLineSegment(sketch, "E12.6.1.32", {"start": v(-3, 3.96) * mm, "end": v(-2.9, 4.06) * mm});
            skLineSegment(sketch, "E12.6.1.33", {"start": v(-3.01, 4.14) * mm, "end": v(-3, 4.16) * mm});
            skLineSegment(sketch, "E12.6.1.34", {"start": v(-2.9, 3.74) * mm, "end": v(-3, 3.84) * mm});
            skLineSegment(sketch, "E12.6.1.35", {"start": v(-2.9, 3.25) * mm, "end": v(-3, 3.35) * mm});
            skLineSegment(sketch, "E12.6.1.36", {"start": v(-2.9, 3.9) * mm, "end": v(-3, 4) * mm});
            skLineSegment(sketch, "E12.6.1.37", {"start": v(-2.91, 3.92) * mm, "end": v(-2.9, 3.9) * mm});
            skLineSegment(sketch, "E12.6.1.38", {"start": v(-2.91, 3.6) * mm, "end": v(-2.9, 3.58) * mm});
            skLineSegment(sketch, "E12.6.1.39", {"start": v(-2.91, 3.27) * mm, "end": v(-2.9, 3.25) * mm});
            skLineSegment(sketch, "E12.6.1.40", {"start": v(-2.91, 3.76) * mm, "end": v(-2.9, 3.74) * mm});
            skLineSegment(sketch, "E12.6.1.41", {"start": v(-2.91, 3.43) * mm, "end": v(-2.9, 3.41) * mm});
            skLineSegment(sketch, "E12.6.1.42", {"start": v(-2.91, 4.08) * mm, "end": v(-2.9, 4.06) * mm});
            skLineSegment(sketch, "E12.6.1.43", {"start": v(-3.01, 3.82) * mm, "end": v(-3, 3.84) * mm});
            skLineSegment(sketch, "E12.6.1.44", {"start": v(-3.01, 3.82) * mm, "end": v(-3, 3.8) * mm});
            skLineSegment(sketch, "E12.6.1.45", {"start": v(-3.01, 3.17) * mm, "end": v(-3, 3.15) * mm});
            skLineSegment(sketch, "E12.6.1.46", {"start": v(-3, 3.8) * mm, "end": v(-2.98, 3.82) * mm});
            skLineSegment(sketch, "E12.6.1.47", {"start": v(-3, 3.15) * mm, "end": v(-2.98, 3.17) * mm});
            skLineSegment(sketch, "E12.6.1.48", {"start": v(-3, 3.96) * mm, "end": v(-2.98, 3.98) * mm});
            skLineSegment(sketch, "E12.6.1.49", {"start": v(-3.01, 3.33) * mm, "end": v(-3, 3.32) * mm});
            skLineSegment(sketch, "E12.6.1.50", {"start": v(-3.01, 3.66) * mm, "end": v(-3, 3.64) * mm});
            skLineSegment(sketch, "E12.6.1.51", {"start": v(-3, 3.64) * mm, "end": v(-2.98, 3.66) * mm});
            skLineSegment(sketch, "E12.6.1.52", {"start": v(-3.01, 3.5) * mm, "end": v(-3, 3.48) * mm});
            skLineSegment(sketch, "E12.6.1.53", {"start": v(-3.01, 3.66) * mm, "end": v(-3, 3.68) * mm});
            skLineSegment(sketch, "E12.6.1.54", {"start": v(-3.01, 3.33) * mm, "end": v(-3, 3.35) * mm});
            skLineSegment(sketch, "E12.6.1.55", {"start": v(-3.01, 3.98) * mm, "end": v(-3, 4) * mm});
            skLineSegment(sketch, "E12.6.1.56", {"start": v(-3.01, 3.98) * mm, "end": v(-3, 3.96) * mm});
            skLineSegment(sketch, "E12.6.1.57", {"start": v(-3.01, 3.5) * mm, "end": v(-3, 3.51) * mm});
            skLineSegment(sketch, "E12.6.1.58", {"start": v(-3, 3.48) * mm, "end": v(-2.98, 3.5) * mm});
            skLineSegment(sketch, "E12.6.1.59", {"start": v(-3, 3.32) * mm, "end": v(-2.98, 3.33) * mm});
            skLineSegment(sketch, "E12.7.0.0", {"start": v(-2.76, 1.53) * mm, "end": v(-2.86, 1.63) * mm});
            skLineSegment(sketch, "E12.7.0.1", {"start": v(-2.76, 1.2) * mm, "end": v(-2.86, 1.3) * mm});
            skPoint(sketch, "E12.7.0.2", {"position": v(-2.8, 1.99) * mm});
            skLineSegment(sketch, "E12.7.0.3", {"start": v(-2.74, 2.03) * mm, "end": v(-2.84, 2.13) * mm});
            skPoint(sketch, "E12.7.0.4", {"position": v(-2.88, 1.34) * mm});
            skLineSegment(sketch, "E12.7.0.5", {"start": v(-2.76, 2.01) * mm, "end": v(-2.86, 2.1) * mm});
            skPoint(sketch, "E12.7.0.6", {"position": v(-2.88, 1.5) * mm});
            skPoint(sketch, "E12.7.0.7", {"position": v(-2.88, 1.83) * mm});
            skPoint(sketch, "E12.7.0.8", {"position": v(-2.8, 1.34) * mm});
            skPoint(sketch, "E12.7.0.9", {"position": v(-2.8, 1.67) * mm});
            skLineSegment(sketch, "E12.7.0.10", {"start": v(-2.76, 1.36) * mm, "end": v(-2.86, 1.46) * mm});
            skPoint(sketch, "E12.7.0.11", {"position": v(-2.8, 1.5) * mm});
            skPoint(sketch, "E12.7.0.12", {"position": v(-2.8, 1.18) * mm});
            skLineSegment(sketch, "E12.7.0.13", {"start": v(-2.76, 1.69) * mm, "end": v(-2.86, 1.79) * mm});
            skPoint(sketch, "E12.7.0.14", {"position": v(-2.88, 1.99) * mm});
            skPoint(sketch, "E12.7.0.15", {"position": v(-2.88, 1.67) * mm});
            skLineSegment(sketch, "E12.7.0.16", {"start": v(-2.76, 1.85) * mm, "end": v(-2.86, 1.95) * mm});
            skPoint(sketch, "E12.7.0.17", {"position": v(-2.88, 1.18) * mm});
            skPoint(sketch, "E12.7.0.18", {"position": v(-2.8, 1.83) * mm});
            skLineSegment(sketch, "E12.7.0.19", {"start": v(-2.74, 1.38) * mm, "end": v(-2.84, 1.48) * mm});
            skLineSegment(sketch, "E12.7.0.20", {"start": v(-2.86, 1.95) * mm, "end": v(-2.76, 2.05) * mm});
            skLineSegment(sketch, "E12.7.0.21", {"start": v(-2.84, 1.77) * mm, "end": v(-2.74, 1.87) * mm});
            skLineSegment(sketch, "E12.7.0.22", {"start": v(-2.74, 1.54) * mm, "end": v(-2.84, 1.64) * mm});
            skLineSegment(sketch, "E12.7.0.23", {"start": v(-2.84, 1.28) * mm, "end": v(-2.74, 1.38) * mm});
            skLineSegment(sketch, "E12.7.0.24", {"start": v(-2.84, 1.6) * mm, "end": v(-2.74, 1.7) * mm});
            skLineSegment(sketch, "E12.7.0.25", {"start": v(-2.86, 1.46) * mm, "end": v(-2.76, 1.56) * mm});
            skLineSegment(sketch, "E12.7.0.26", {"start": v(-2.86, 1.14) * mm, "end": v(-2.76, 1.24) * mm});
            skLineSegment(sketch, "E12.7.0.27", {"start": v(-2.84, 1.45) * mm, "end": v(-2.74, 1.54) * mm});
            skLineSegment(sketch, "E12.7.0.28", {"start": v(-2.86, 1.3) * mm, "end": v(-2.76, 1.4) * mm});
            skLineSegment(sketch, "E12.7.0.29", {"start": v(-2.84, 1.12) * mm, "end": v(-2.74, 1.22) * mm});
            skLineSegment(sketch, "E12.7.0.30", {"start": v(-2.86, 1.63) * mm, "end": v(-2.76, 1.72) * mm});
            skLineSegment(sketch, "E12.7.0.31", {"start": v(-2.86, 1.79) * mm, "end": v(-2.76, 1.89) * mm});
            skLineSegment(sketch, "E12.7.0.32", {"start": v(-2.84, 1.93) * mm, "end": v(-2.74, 2.03) * mm});
            skLineSegment(sketch, "E12.7.0.33", {"start": v(-2.86, 2.1) * mm, "end": v(-2.84, 2.13) * mm});
            skLineSegment(sketch, "E12.7.0.34", {"start": v(-2.74, 1.7) * mm, "end": v(-2.84, 1.8) * mm});
            skLineSegment(sketch, "E12.7.0.35", {"start": v(-2.74, 1.22) * mm, "end": v(-2.84, 1.32) * mm});
            skLineSegment(sketch, "E12.7.0.36", {"start": v(-2.74, 1.87) * mm, "end": v(-2.84, 1.97) * mm});
            skLineSegment(sketch, "E12.7.0.37", {"start": v(-2.76, 1.89) * mm, "end": v(-2.74, 1.87) * mm});
            skLineSegment(sketch, "E12.7.0.38", {"start": v(-2.76, 1.56) * mm, "end": v(-2.74, 1.54) * mm});
            skLineSegment(sketch, "E12.7.0.39", {"start": v(-2.76, 1.24) * mm, "end": v(-2.74, 1.22) * mm});
            skLineSegment(sketch, "E12.7.0.40", {"start": v(-2.76, 1.72) * mm, "end": v(-2.74, 1.7) * mm});
            skLineSegment(sketch, "E12.7.0.41", {"start": v(-2.76, 1.4) * mm, "end": v(-2.74, 1.38) * mm});
            skLineSegment(sketch, "E12.7.0.42", {"start": v(-2.76, 2.05) * mm, "end": v(-2.74, 2.03) * mm});
            skLineSegment(sketch, "E12.7.0.43", {"start": v(-2.86, 1.79) * mm, "end": v(-2.84, 1.8) * mm});
            skLineSegment(sketch, "E12.7.0.44", {"start": v(-2.86, 1.79) * mm, "end": v(-2.84, 1.77) * mm});
            skLineSegment(sketch, "E12.7.0.45", {"start": v(-2.86, 1.14) * mm, "end": v(-2.84, 1.12) * mm});
            skLineSegment(sketch, "E12.7.0.46", {"start": v(-2.84, 1.77) * mm, "end": v(-2.83, 1.79) * mm});
            skLineSegment(sketch, "E12.7.0.47", {"start": v(-2.84, 1.12) * mm, "end": v(-2.82, 1.14) * mm});
            skLineSegment(sketch, "E12.7.0.48", {"start": v(-2.84, 1.93) * mm, "end": v(-2.83, 1.95) * mm});
            skLineSegment(sketch, "E12.7.0.49", {"start": v(-2.86, 1.3) * mm, "end": v(-2.84, 1.28) * mm});
            skLineSegment(sketch, "E12.7.0.50", {"start": v(-2.86, 1.63) * mm, "end": v(-2.84, 1.6) * mm});
            skLineSegment(sketch, "E12.7.0.51", {"start": v(-2.84, 1.6) * mm, "end": v(-2.82, 1.62) * mm});
            skLineSegment(sketch, "E12.7.0.52", {"start": v(-2.86, 1.46) * mm, "end": v(-2.84, 1.45) * mm});
            skLineSegment(sketch, "E12.7.0.53", {"start": v(-2.86, 1.63) * mm, "end": v(-2.84, 1.64) * mm});
            skLineSegment(sketch, "E12.7.0.54", {"start": v(-2.86, 1.3) * mm, "end": v(-2.84, 1.32) * mm});
            skLineSegment(sketch, "E12.7.0.55", {"start": v(-2.86, 1.95) * mm, "end": v(-2.84, 1.97) * mm});
            skLineSegment(sketch, "E12.7.0.56", {"start": v(-2.86, 1.95) * mm, "end": v(-2.84, 1.93) * mm});
            skLineSegment(sketch, "E12.7.0.57", {"start": v(-2.86, 1.46) * mm, "end": v(-2.84, 1.48) * mm});
            skLineSegment(sketch, "E12.7.0.58", {"start": v(-2.84, 1.45) * mm, "end": v(-2.82, 1.46) * mm});
            skLineSegment(sketch, "E12.7.0.59", {"start": v(-2.84, 1.28) * mm, "end": v(-2.82, 1.3) * mm});
            skLineSegment(sketch, "E12.7.1.0", {"start": v(-2.76, 3.56) * mm, "end": v(-2.86, 3.66) * mm});
            skLineSegment(sketch, "E12.7.1.1", {"start": v(-2.76, 3.24) * mm, "end": v(-2.86, 3.33) * mm});
            skPoint(sketch, "E12.7.1.2", {"position": v(-2.8, 4.02) * mm});
            skLineSegment(sketch, "E12.7.1.3", {"start": v(-2.74, 4.06) * mm, "end": v(-2.84, 4.16) * mm});
            skPoint(sketch, "E12.7.1.4", {"position": v(-2.88, 3.37) * mm});
            skLineSegment(sketch, "E12.7.1.5", {"start": v(-2.76, 4.04) * mm, "end": v(-2.86, 4.14) * mm});
            skPoint(sketch, "E12.7.1.6", {"position": v(-2.88, 3.54) * mm});
            skPoint(sketch, "E12.7.1.7", {"position": v(-2.88, 3.86) * mm});
            skPoint(sketch, "E12.7.1.8", {"position": v(-2.8, 3.37) * mm});
            skPoint(sketch, "E12.7.1.9", {"position": v(-2.8, 3.7) * mm});
            skLineSegment(sketch, "E12.7.1.10", {"start": v(-2.76, 3.4) * mm, "end": v(-2.86, 3.5) * mm});
            skPoint(sketch, "E12.7.1.11", {"position": v(-2.8, 3.54) * mm});
            skPoint(sketch, "E12.7.1.12", {"position": v(-2.8, 3.21) * mm});
            skLineSegment(sketch, "E12.7.1.13", {"start": v(-2.76, 3.72) * mm, "end": v(-2.86, 3.82) * mm});
            skPoint(sketch, "E12.7.1.14", {"position": v(-2.88, 4.02) * mm});
            skPoint(sketch, "E12.7.1.15", {"position": v(-2.88, 3.7) * mm});
            skLineSegment(sketch, "E12.7.1.16", {"start": v(-2.76, 3.88) * mm, "end": v(-2.86, 3.98) * mm});
            skPoint(sketch, "E12.7.1.17", {"position": v(-2.88, 3.21) * mm});
            skPoint(sketch, "E12.7.1.18", {"position": v(-2.8, 3.86) * mm});
            skLineSegment(sketch, "E12.7.1.19", {"start": v(-2.74, 3.41) * mm, "end": v(-2.84, 3.51) * mm});
            skLineSegment(sketch, "E12.7.1.20", {"start": v(-2.86, 3.98) * mm, "end": v(-2.76, 4.08) * mm});
            skLineSegment(sketch, "E12.7.1.21", {"start": v(-2.84, 3.8) * mm, "end": v(-2.74, 3.9) * mm});
            skLineSegment(sketch, "E12.7.1.22", {"start": v(-2.74, 3.58) * mm, "end": v(-2.84, 3.68) * mm});
            skLineSegment(sketch, "E12.7.1.23", {"start": v(-2.84, 3.32) * mm, "end": v(-2.74, 3.41) * mm});
            skLineSegment(sketch, "E12.7.1.24", {"start": v(-2.84, 3.64) * mm, "end": v(-2.74, 3.74) * mm});
            skLineSegment(sketch, "E12.7.1.25", {"start": v(-2.86, 3.5) * mm, "end": v(-2.76, 3.6) * mm});
            skLineSegment(sketch, "E12.7.1.26", {"start": v(-2.86, 3.17) * mm, "end": v(-2.76, 3.27) * mm});
            skLineSegment(sketch, "E12.7.1.27", {"start": v(-2.84, 3.48) * mm, "end": v(-2.74, 3.58) * mm});
            skLineSegment(sketch, "E12.7.1.28", {"start": v(-2.86, 3.33) * mm, "end": v(-2.76, 3.43) * mm});
            skLineSegment(sketch, "E12.7.1.29", {"start": v(-2.84, 3.15) * mm, "end": v(-2.74, 3.25) * mm});
            skLineSegment(sketch, "E12.7.1.30", {"start": v(-2.86, 3.66) * mm, "end": v(-2.76, 3.76) * mm});
            skLineSegment(sketch, "E12.7.1.31", {"start": v(-2.86, 3.82) * mm, "end": v(-2.76, 3.92) * mm});
            skLineSegment(sketch, "E12.7.1.32", {"start": v(-2.84, 3.96) * mm, "end": v(-2.74, 4.06) * mm});
            skLineSegment(sketch, "E12.7.1.33", {"start": v(-2.86, 4.14) * mm, "end": v(-2.84, 4.16) * mm});
            skLineSegment(sketch, "E12.7.1.34", {"start": v(-2.74, 3.74) * mm, "end": v(-2.84, 3.84) * mm});
            skLineSegment(sketch, "E12.7.1.35", {"start": v(-2.74, 3.25) * mm, "end": v(-2.84, 3.35) * mm});
            skLineSegment(sketch, "E12.7.1.36", {"start": v(-2.74, 3.9) * mm, "end": v(-2.84, 4) * mm});
            skLineSegment(sketch, "E12.7.1.37", {"start": v(-2.76, 3.92) * mm, "end": v(-2.74, 3.9) * mm});
            skLineSegment(sketch, "E12.7.1.38", {"start": v(-2.76, 3.6) * mm, "end": v(-2.74, 3.58) * mm});
            skLineSegment(sketch, "E12.7.1.39", {"start": v(-2.76, 3.27) * mm, "end": v(-2.74, 3.25) * mm});
            skLineSegment(sketch, "E12.7.1.40", {"start": v(-2.76, 3.76) * mm, "end": v(-2.74, 3.74) * mm});
            skLineSegment(sketch, "E12.7.1.41", {"start": v(-2.76, 3.43) * mm, "end": v(-2.74, 3.41) * mm});
            skLineSegment(sketch, "E12.7.1.42", {"start": v(-2.76, 4.08) * mm, "end": v(-2.74, 4.06) * mm});
            skLineSegment(sketch, "E12.7.1.43", {"start": v(-2.86, 3.82) * mm, "end": v(-2.84, 3.84) * mm});
            skLineSegment(sketch, "E12.7.1.44", {"start": v(-2.86, 3.82) * mm, "end": v(-2.84, 3.8) * mm});
            skLineSegment(sketch, "E12.7.1.45", {"start": v(-2.86, 3.17) * mm, "end": v(-2.84, 3.15) * mm});
            skLineSegment(sketch, "E12.7.1.46", {"start": v(-2.84, 3.8) * mm, "end": v(-2.83, 3.82) * mm});
            skLineSegment(sketch, "E12.7.1.47", {"start": v(-2.84, 3.15) * mm, "end": v(-2.82, 3.17) * mm});
            skLineSegment(sketch, "E12.7.1.48", {"start": v(-2.84, 3.96) * mm, "end": v(-2.83, 3.98) * mm});
            skLineSegment(sketch, "E12.7.1.49", {"start": v(-2.86, 3.33) * mm, "end": v(-2.84, 3.32) * mm});
            skLineSegment(sketch, "E12.7.1.50", {"start": v(-2.86, 3.66) * mm, "end": v(-2.84, 3.64) * mm});
            skLineSegment(sketch, "E12.7.1.51", {"start": v(-2.84, 3.64) * mm, "end": v(-2.82, 3.66) * mm});
            skLineSegment(sketch, "E12.7.1.52", {"start": v(-2.86, 3.5) * mm, "end": v(-2.84, 3.48) * mm});
            skLineSegment(sketch, "E12.7.1.53", {"start": v(-2.86, 3.66) * mm, "end": v(-2.84, 3.68) * mm});
            skLineSegment(sketch, "E12.7.1.54", {"start": v(-2.86, 3.33) * mm, "end": v(-2.84, 3.35) * mm});
            skLineSegment(sketch, "E12.7.1.55", {"start": v(-2.86, 3.98) * mm, "end": v(-2.84, 4) * mm});
            skLineSegment(sketch, "E12.7.1.56", {"start": v(-2.86, 3.98) * mm, "end": v(-2.84, 3.96) * mm});
            skLineSegment(sketch, "E12.7.1.57", {"start": v(-2.86, 3.5) * mm, "end": v(-2.84, 3.51) * mm});
            skLineSegment(sketch, "E12.7.1.58", {"start": v(-2.84, 3.48) * mm, "end": v(-2.82, 3.5) * mm});
            skLineSegment(sketch, "E12.7.1.59", {"start": v(-2.84, 3.32) * mm, "end": v(-2.82, 3.33) * mm});
            skLineSegment(sketch, "E12.direction1", {"start": v(-3.9, 1.12) * mm, "end": v(-3.76, 1.12) * mm, "construction": true});
            skLineSegment(sketch, "E12.direction2", {"start": v(-3.9, 1.12) * mm, "end": v(-3.9, 3.15) * mm, "construction": true});
            skSolve(sketch);
        }
        {
            var Q0;
            {var subQ0=sQuery(id+"F0.wireOp",EDGE,"E12.2.0.3");Q0=makeQuery(id+"F0.imprint","IMPRINT",FACE,{"disambiguationData":[TD([[makeQuery(id+"F0.imprint","IMPRINT",EDGE,{"derivedFrom":subQ0}),1.0]])]});}
            var Q1;
            {var subQ4=sQuery(id+"F0.wireOp",EDGE,"E0.top");Q1=makeQuery(id+"F0.imprint","IMPRINT",FACE,{"disambiguationData":[TD([[makeQuery(id+"F0.imprint","IMPRINT",EDGE,{"derivedFrom":subQ4}),1.0]])]});}
            var Q2;
            {var subQ0=sQuery(id+"F0.wireOp",EDGE,"E12.1.0.3");Q2=makeQuery(id+"F0.imprint","IMPRINT",FACE,{"disambiguationData":[TD([[makeQuery(id+"F0.imprint","IMPRINT",EDGE,{"derivedFrom":subQ0}),1.0]])]});}
            var Q3;
            {var subQ1=sQuery(id+"F0.wireOp",EDGE,"E12.4.0.13");var subQ5=makeQuery(id+"F0.imprint","IMPRINT",VERTEX,{"derivedFrom":subQ1});Q3=makeQuery(id+"F0.imprint","IMPRINT",FACE,{"disambiguationData":[TD([[makeQuery(id+"F0.imprint","IMPRINT",EDGE,{"disambiguationData":[TD([[subQ5,1.0]])],"derivedFrom":subQ1}),-1.0]])]});}
            var Q4;
            {var subQ1=sQuery(id+"F0.wireOp",EDGE,"E12.6.0.13");var subQ5=makeQuery(id+"F0.imprint","IMPRINT",VERTEX,{"derivedFrom":subQ1});Q4=makeQuery(id+"F0.imprint","IMPRINT",FACE,{"disambiguationData":[TD([[makeQuery(id+"F0.imprint","IMPRINT",EDGE,{"disambiguationData":[TD([[subQ5,1.0]])],"derivedFrom":subQ1}),-1.0]])]});}
            var Q5;
            {var subQ1=sQuery(id+"F0.wireOp",EDGE,"E12.5.0.13");var subQ5=makeQuery(id+"F0.imprint","IMPRINT",VERTEX,{"derivedFrom":subQ1});Q5=makeQuery(id+"F0.imprint","IMPRINT",FACE,{"disambiguationData":[TD([[makeQuery(id+"F0.imprint","IMPRINT",EDGE,{"disambiguationData":[TD([[subQ5,1.0]])],"derivedFrom":subQ1}),-1.0]])]});}
            var Q6;
            {var subQ1=sQuery(id+"F0.wireOp",EDGE,"E12.7.0.13");var subQ5=makeQuery(id+"F0.imprint","IMPRINT",VERTEX,{"derivedFrom":subQ1});Q6=makeQuery(id+"F0.imprint","IMPRINT",FACE,{"disambiguationData":[TD([[makeQuery(id+"F0.imprint","IMPRINT",EDGE,{"disambiguationData":[TD([[subQ5,1.0]])],"derivedFrom":subQ1}),-1.0]])]});}
            var Q7;
            {var subQ0=sQuery(id+"F0.wireOp",EDGE,"E12.5.0.3");Q7=makeQuery(id+"F0.imprint","IMPRINT",FACE,{"disambiguationData":[TD([[makeQuery(id+"F0.imprint","IMPRINT",EDGE,{"derivedFrom":subQ0}),1.0]])]});}
            var Q8;
            {var subQ1=sQuery(id+"F0.wireOp",EDGE,"E12.2.0.13");var subQ5=makeQuery(id+"F0.imprint","IMPRINT",VERTEX,{"derivedFrom":subQ1});Q8=makeQuery(id+"F0.imprint","IMPRINT",FACE,{"disambiguationData":[TD([[makeQuery(id+"F0.imprint","IMPRINT",EDGE,{"disambiguationData":[TD([[subQ5,1.0]])],"derivedFrom":subQ1}),-1.0]])]});}
            var Q9;
            {var subQ1=sQuery(id+"F0.wireOp",EDGE,"E12.1.0.13");var subQ5=makeQuery(id+"F0.imprint","IMPRINT",VERTEX,{"derivedFrom":subQ1});Q9=makeQuery(id+"F0.imprint","IMPRINT",FACE,{"disambiguationData":[TD([[makeQuery(id+"F0.imprint","IMPRINT",EDGE,{"disambiguationData":[TD([[subQ5,1.0]])],"derivedFrom":subQ1}),-1.0]])]});}
            var Q10;
            {var subQ1=sQuery(id+"F0.wireOp",EDGE,"E12.3.0.13");var subQ5=makeQuery(id+"F0.imprint","IMPRINT",VERTEX,{"derivedFrom":subQ1});Q10=makeQuery(id+"F0.imprint","IMPRINT",FACE,{"disambiguationData":[TD([[makeQuery(id+"F0.imprint","IMPRINT",EDGE,{"disambiguationData":[TD([[subQ5,1.0]])],"derivedFrom":subQ1}),-1.0]])]});}
            var Q11;
            {var subQ0=sQuery(id+"F0.wireOp",EDGE,"E6.left");Q11=makeQuery(id+"F0.imprint","IMPRINT",FACE,{"disambiguationData":[TD([[makeQuery(id+"F0.imprint","IMPRINT",EDGE,{"derivedFrom":subQ0}),-1.0]])]});}
            var Q12;
            {var subQ0=sQuery(id+"F0.wireOp",EDGE,"E12.2.0.51");Q12=makeQuery(id+"F0.imprint","IMPRINT",FACE,{"disambiguationData":[TD([[makeQuery(id+"F0.imprint","IMPRINT",EDGE,{"derivedFrom":subQ0}),-1.0]])]});}
            var Q13;
            {var subQ0=sQuery(id+"F0.wireOp",EDGE,"E12.1.0.48");Q13=makeQuery(id+"F0.imprint","IMPRINT",FACE,{"disambiguationData":[TD([[makeQuery(id+"F0.imprint","IMPRINT",EDGE,{"derivedFrom":subQ0}),-1.0]])]});}
            var Q14;
            {var subQ0=sQuery(id+"F0.wireOp",EDGE,"E12.1.0.51");Q14=makeQuery(id+"F0.imprint","IMPRINT",FACE,{"disambiguationData":[TD([[makeQuery(id+"F0.imprint","IMPRINT",EDGE,{"derivedFrom":subQ0}),-1.0]])]});}
            var Q15;
            {var subQ0=sQuery(id+"F0.wireOp",EDGE,"E12.3.0.48");Q15=makeQuery(id+"F0.imprint","IMPRINT",FACE,{"disambiguationData":[TD([[makeQuery(id+"F0.imprint","IMPRINT",EDGE,{"derivedFrom":subQ0}),-1.0]])]});}
            var Q16;
            {var subQ0=sQuery(id+"F0.wireOp",EDGE,"E12.3.0.51");Q16=makeQuery(id+"F0.imprint","IMPRINT",FACE,{"disambiguationData":[TD([[makeQuery(id+"F0.imprint","IMPRINT",EDGE,{"derivedFrom":subQ0}),-1.0]])]});}
            var Q17;
            {var subQ0=sQuery(id+"F0.wireOp",EDGE,"E12.2.0.48");Q17=makeQuery(id+"F0.imprint","IMPRINT",FACE,{"disambiguationData":[TD([[makeQuery(id+"F0.imprint","IMPRINT",EDGE,{"derivedFrom":subQ0}),-1.0]])]});}
            var Q18;
            {var subQ0=sQuery(id+"F0.wireOp",EDGE,"E12.4.0.48");Q18=makeQuery(id+"F0.imprint","IMPRINT",FACE,{"disambiguationData":[TD([[makeQuery(id+"F0.imprint","IMPRINT",EDGE,{"derivedFrom":subQ0}),-1.0]])]});}
            var Q19;
            {var subQ0=sQuery(id+"F0.wireOp",EDGE,"E12.4.0.51");Q19=makeQuery(id+"F0.imprint","IMPRINT",FACE,{"disambiguationData":[TD([[makeQuery(id+"F0.imprint","IMPRINT",EDGE,{"derivedFrom":subQ0}),-1.0]])]});}
            var Q20;
            {var subQ0=sQuery(id+"F0.wireOp",EDGE,"E12.6.0.51");Q20=makeQuery(id+"F0.imprint","IMPRINT",FACE,{"disambiguationData":[TD([[makeQuery(id+"F0.imprint","IMPRINT",EDGE,{"derivedFrom":subQ0}),-1.0]])]});}
            var Q21;
            {var subQ0=sQuery(id+"F0.wireOp",EDGE,"E12.5.0.48");Q21=makeQuery(id+"F0.imprint","IMPRINT",FACE,{"disambiguationData":[TD([[makeQuery(id+"F0.imprint","IMPRINT",EDGE,{"derivedFrom":subQ0}),-1.0]])]});}
            var Q22;
            {var subQ0=sQuery(id+"F0.wireOp",EDGE,"E12.5.0.51");Q22=makeQuery(id+"F0.imprint","IMPRINT",FACE,{"disambiguationData":[TD([[makeQuery(id+"F0.imprint","IMPRINT",EDGE,{"derivedFrom":subQ0}),-1.0]])]});}
            var Q23;
            {var subQ0=sQuery(id+"F0.wireOp",EDGE,"E12.7.0.48");Q23=makeQuery(id+"F0.imprint","IMPRINT",FACE,{"disambiguationData":[TD([[makeQuery(id+"F0.imprint","IMPRINT",EDGE,{"derivedFrom":subQ0}),-1.0]])]});}
            var Q24;
            {var subQ0=sQuery(id+"F0.wireOp",EDGE,"E12.7.0.51");Q24=makeQuery(id+"F0.imprint","IMPRINT",FACE,{"disambiguationData":[TD([[makeQuery(id+"F0.imprint","IMPRINT",EDGE,{"derivedFrom":subQ0}),-1.0]])]});}
            var Q25;
            {var subQ0=sQuery(id+"F0.wireOp",EDGE,"E12.6.0.48");Q25=makeQuery(id+"F0.imprint","IMPRINT",FACE,{"disambiguationData":[TD([[makeQuery(id+"F0.imprint","IMPRINT",EDGE,{"derivedFrom":subQ0}),-1.0]])]});}
            var Q26;
            {var subQ0=sQuery(id+"F0.wireOp",EDGE,"E12.3.0.3");Q26=makeQuery(id+"F0.imprint","IMPRINT",FACE,{"disambiguationData":[TD([[makeQuery(id+"F0.imprint","IMPRINT",EDGE,{"derivedFrom":subQ0}),1.0]])]});}
            var Q27;
            {var subQ0=sQuery(id+"F0.wireOp",EDGE,"E0.left");Q27=makeQuery(id+"F0.imprint","IMPRINT",FACE,{"disambiguationData":[TD([[makeQuery(id+"F0.imprint","IMPRINT",EDGE,{"derivedFrom":subQ0}),-1.0]])]});}
            var Q28;
            {var subQ0=sQuery(id+"F0.wireOp",EDGE,"E8.left");Q28=makeQuery(id+"F0.imprint","IMPRINT",FACE,{"disambiguationData":[TD([[makeQuery(id+"F0.imprint","IMPRINT",EDGE,{"derivedFrom":subQ0}),-1.0]])]});}
            var Q29;
            {var subQ0=sQuery(id+"F0.wireOp",EDGE,"E12.6.0.3");Q29=makeQuery(id+"F0.imprint","IMPRINT",FACE,{"disambiguationData":[TD([[makeQuery(id+"F0.imprint","IMPRINT",EDGE,{"derivedFrom":subQ0}),1.0]])]});}
            var Q30;
            {var subQ0=sQuery(id+"F0.wireOp",EDGE,"E12.2.0.59");Q30=makeQuery(id+"F0.imprint","IMPRINT",FACE,{"disambiguationData":[TD([[makeQuery(id+"F0.imprint","IMPRINT",EDGE,{"derivedFrom":subQ0}),-1.0]])]});}
            var Q31;
            {var subQ0=sQuery(id+"F0.wireOp",EDGE,"E12.1.0.59");Q31=makeQuery(id+"F0.imprint","IMPRINT",FACE,{"disambiguationData":[TD([[makeQuery(id+"F0.imprint","IMPRINT",EDGE,{"derivedFrom":subQ0}),-1.0]])]});}
            var Q32;
            {var subQ0=sQuery(id+"F0.wireOp",EDGE,"E12.3.0.59");Q32=makeQuery(id+"F0.imprint","IMPRINT",FACE,{"disambiguationData":[TD([[makeQuery(id+"F0.imprint","IMPRINT",EDGE,{"derivedFrom":subQ0}),-1.0]])]});}
            var Q33;
            {var subQ0=sQuery(id+"F0.wireOp",EDGE,"E12.4.0.59");Q33=makeQuery(id+"F0.imprint","IMPRINT",FACE,{"disambiguationData":[TD([[makeQuery(id+"F0.imprint","IMPRINT",EDGE,{"derivedFrom":subQ0}),-1.0]])]});}
            var Q34;
            {var subQ0=sQuery(id+"F0.wireOp",EDGE,"E12.6.0.59");Q34=makeQuery(id+"F0.imprint","IMPRINT",FACE,{"disambiguationData":[TD([[makeQuery(id+"F0.imprint","IMPRINT",EDGE,{"derivedFrom":subQ0}),-1.0]])]});}
            var Q35;
            {var subQ0=sQuery(id+"F0.wireOp",EDGE,"E12.5.0.59");Q35=makeQuery(id+"F0.imprint","IMPRINT",FACE,{"disambiguationData":[TD([[makeQuery(id+"F0.imprint","IMPRINT",EDGE,{"derivedFrom":subQ0}),-1.0]])]});}
            var Q36;
            {var subQ0=sQuery(id+"F0.wireOp",EDGE,"E12.7.0.59");Q36=makeQuery(id+"F0.imprint","IMPRINT",FACE,{"disambiguationData":[TD([[makeQuery(id+"F0.imprint","IMPRINT",EDGE,{"derivedFrom":subQ0}),-1.0]])]});}
            var Q37;
            {var subQ5=sQuery(id+"F0.wireOp",EDGE,"E4.bottom");var subQ6=makeQuery(id+"F0.imprint","IMPRINT",VERTEX,{"derivedFrom":subQ5});Q37=makeQuery(id+"F0.imprint","IMPRINT",FACE,{"disambiguationData":[TD([[makeQuery(id+"F0.imprint","IMPRINT",EDGE,{"disambiguationData":[TD([[subQ6,1.0]])],"derivedFrom":subQ5}),-1.0]])]});}
            var Q38;
            {var subQ0=sQuery(id+"F0.wireOp",EDGE,"E12.4.0.3");Q38=makeQuery(id+"F0.imprint","IMPRINT",FACE,{"disambiguationData":[TD([[makeQuery(id+"F0.imprint","IMPRINT",EDGE,{"derivedFrom":subQ0}),1.0]])]});}
            var Q39;
            {var subQ0=sQuery(id+"F0.wireOp",EDGE,"E12.7.0.58");Q39=makeQuery(id+"F0.imprint","IMPRINT",FACE,{"disambiguationData":[TD([[makeQuery(id+"F0.imprint","IMPRINT",EDGE,{"derivedFrom":subQ0}),-1.0]])]});}
            var Q40;
            {var subQ0=sQuery(id+"F0.wireOp",EDGE,"E4.left");Q40=makeQuery(id+"F0.imprint","IMPRINT",FACE,{"disambiguationData":[TD([[makeQuery(id+"F0.imprint","IMPRINT",EDGE,{"derivedFrom":subQ0}),-1.0]])]});}
            var Q41;
            {var subQ0=sQuery(id+"F0.wireOp",EDGE,"E12.7.0.3");Q41=makeQuery(id+"F0.imprint","IMPRINT",FACE,{"disambiguationData":[TD([[makeQuery(id+"F0.imprint","IMPRINT",EDGE,{"derivedFrom":subQ0}),1.0]])]});}
            var Q42;
            {var subQ0=sQuery(id+"F0.wireOp",EDGE,"E12.1.0.58");Q42=makeQuery(id+"F0.imprint","IMPRINT",FACE,{"disambiguationData":[TD([[makeQuery(id+"F0.imprint","IMPRINT",EDGE,{"derivedFrom":subQ0}),-1.0]])]});}
            var Q43;
            {var subQ0=sQuery(id+"F0.wireOp",EDGE,"E12.2.0.58");Q43=makeQuery(id+"F0.imprint","IMPRINT",FACE,{"disambiguationData":[TD([[makeQuery(id+"F0.imprint","IMPRINT",EDGE,{"derivedFrom":subQ0}),-1.0]])]});}
            var Q44;
            {var subQ0=sQuery(id+"F0.wireOp",EDGE,"E12.4.0.58");Q44=makeQuery(id+"F0.imprint","IMPRINT",FACE,{"disambiguationData":[TD([[makeQuery(id+"F0.imprint","IMPRINT",EDGE,{"derivedFrom":subQ0}),-1.0]])]});}
            var Q45;
            {var subQ0=sQuery(id+"F0.wireOp",EDGE,"E12.3.0.58");Q45=makeQuery(id+"F0.imprint","IMPRINT",FACE,{"disambiguationData":[TD([[makeQuery(id+"F0.imprint","IMPRINT",EDGE,{"derivedFrom":subQ0}),-1.0]])]});}
            var Q46;
            {var subQ0=sQuery(id+"F0.wireOp",EDGE,"E12.5.0.58");Q46=makeQuery(id+"F0.imprint","IMPRINT",FACE,{"disambiguationData":[TD([[makeQuery(id+"F0.imprint","IMPRINT",EDGE,{"derivedFrom":subQ0}),-1.0]])]});}
            var Q47;
            {var subQ0=sQuery(id+"F0.wireOp",EDGE,"E12.6.0.58");Q47=makeQuery(id+"F0.imprint","IMPRINT",FACE,{"disambiguationData":[TD([[makeQuery(id+"F0.imprint","IMPRINT",EDGE,{"derivedFrom":subQ0}),-1.0]])]});}
            var Q48;
            {var subQ5=sQuery(id+"F0.wireOp",EDGE,"E11.left");Q48=makeQuery(id+"F0.imprint","IMPRINT",FACE,{"disambiguationData":[TD([[makeQuery(id+"F0.imprint","IMPRINT",EDGE,{"derivedFrom":subQ5}),1.0]])]});}
            var Q49;
            {var subQ5=sQuery(id+"F0.wireOp",EDGE,"E12.1.0.45");Q49=makeQuery(id+"F0.imprint","IMPRINT",FACE,{"disambiguationData":[TD([[makeQuery(id+"F0.imprint","IMPRINT",EDGE,{"derivedFrom":subQ5}),1.0]])]});}
            var Q50;
            {var subQ5=sQuery(id+"F0.wireOp",EDGE,"E12.2.0.45");Q50=makeQuery(id+"F0.imprint","IMPRINT",FACE,{"disambiguationData":[TD([[makeQuery(id+"F0.imprint","IMPRINT",EDGE,{"derivedFrom":subQ5}),1.0]])]});}
            var Q51;
            {var subQ0=sQuery(id+"F0.wireOp",EDGE,"E7.top");var subQ1=sQuery(id+"F0.wireOp",EDGE,"E6.bottom");var subQ2=makeQuery(id+"F0.imprint","INTERSECT",VERTEX,{"derivedFrom":[subQ1,subQ0]});Q51=makeQuery(id+"F0.imprint","IMPRINT",FACE,{"disambiguationData":[TD([[makeQuery(id+"F0.imprint","IMPRINT",EDGE,{"disambiguationData":[TD([[subQ2,-1.0]])],"derivedFrom":subQ1}),1.0]])]});}
            var Q52;
            {var subQ0=sQuery(id+"F0.wireOp",EDGE,"E12.1.0.24");var subQ1=sQuery(id+"F0.wireOp",EDGE,"E12.1.0.13");var subQ2=makeQuery(id+"F0.imprint","INTERSECT",VERTEX,{"derivedFrom":[subQ1,subQ0]});Q52=makeQuery(id+"F0.imprint","IMPRINT",FACE,{"disambiguationData":[TD([[makeQuery(id+"F0.imprint","IMPRINT",EDGE,{"disambiguationData":[TD([[subQ2,-1.0]])],"derivedFrom":subQ1}),1.0]])]});}
            var Q53;
            {var subQ0=sQuery(id+"F0.wireOp",EDGE,"E12.3.0.24");var subQ1=sQuery(id+"F0.wireOp",EDGE,"E12.3.0.13");var subQ2=makeQuery(id+"F0.imprint","INTERSECT",VERTEX,{"derivedFrom":[subQ1,subQ0]});Q53=makeQuery(id+"F0.imprint","IMPRINT",FACE,{"disambiguationData":[TD([[makeQuery(id+"F0.imprint","IMPRINT",EDGE,{"disambiguationData":[TD([[subQ2,-1.0]])],"derivedFrom":subQ1}),1.0]])]});}
            var Q54;
            {var subQ0=sQuery(id+"F0.wireOp",EDGE,"E12.2.0.24");var subQ1=sQuery(id+"F0.wireOp",EDGE,"E12.2.0.13");var subQ2=makeQuery(id+"F0.imprint","INTERSECT",VERTEX,{"derivedFrom":[subQ1,subQ0]});Q54=makeQuery(id+"F0.imprint","IMPRINT",FACE,{"disambiguationData":[TD([[makeQuery(id+"F0.imprint","IMPRINT",EDGE,{"disambiguationData":[TD([[subQ2,-1.0]])],"derivedFrom":subQ1}),1.0]])]});}
            var Q55;
            {var subQ0=sQuery(id+"F0.wireOp",EDGE,"E12.4.0.24");var subQ1=sQuery(id+"F0.wireOp",EDGE,"E12.4.0.13");var subQ2=makeQuery(id+"F0.imprint","INTERSECT",VERTEX,{"derivedFrom":[subQ1,subQ0]});Q55=makeQuery(id+"F0.imprint","IMPRINT",FACE,{"disambiguationData":[TD([[makeQuery(id+"F0.imprint","IMPRINT",EDGE,{"disambiguationData":[TD([[subQ2,-1.0]])],"derivedFrom":subQ1}),1.0]])]});}
            var Q56;
            {var subQ0=sQuery(id+"F0.wireOp",EDGE,"E12.5.0.24");var subQ1=sQuery(id+"F0.wireOp",EDGE,"E12.5.0.13");var subQ2=makeQuery(id+"F0.imprint","INTERSECT",VERTEX,{"derivedFrom":[subQ1,subQ0]});Q56=makeQuery(id+"F0.imprint","IMPRINT",FACE,{"disambiguationData":[TD([[makeQuery(id+"F0.imprint","IMPRINT",EDGE,{"disambiguationData":[TD([[subQ2,-1.0]])],"derivedFrom":subQ1}),1.0]])]});}
            var Q57;
            {var subQ0=sQuery(id+"F0.wireOp",EDGE,"E12.7.0.24");var subQ1=sQuery(id+"F0.wireOp",EDGE,"E12.7.0.13");var subQ2=makeQuery(id+"F0.imprint","INTERSECT",VERTEX,{"derivedFrom":[subQ1,subQ0]});Q57=makeQuery(id+"F0.imprint","IMPRINT",FACE,{"disambiguationData":[TD([[makeQuery(id+"F0.imprint","IMPRINT",EDGE,{"disambiguationData":[TD([[subQ2,-1.0]])],"derivedFrom":subQ1}),1.0]])]});}
            var Q58;
            {var subQ0=sQuery(id+"F0.wireOp",EDGE,"E12.6.0.24");var subQ1=sQuery(id+"F0.wireOp",EDGE,"E12.6.0.13");var subQ2=makeQuery(id+"F0.imprint","INTERSECT",VERTEX,{"derivedFrom":[subQ1,subQ0]});Q58=makeQuery(id+"F0.imprint","IMPRINT",FACE,{"disambiguationData":[TD([[makeQuery(id+"F0.imprint","IMPRINT",EDGE,{"disambiguationData":[TD([[subQ2,-1.0]])],"derivedFrom":subQ1}),1.0]])]});}
            var Q59;
            {var subQ5=sQuery(id+"F0.wireOp",EDGE,"E12.5.0.45");Q59=makeQuery(id+"F0.imprint","IMPRINT",FACE,{"disambiguationData":[TD([[makeQuery(id+"F0.imprint","IMPRINT",EDGE,{"derivedFrom":subQ5}),1.0]])]});}
            var Q60;
            {var subQ0=sQuery(id+"F0.wireOp",EDGE,"E1.top");var subQ1=sQuery(id+"F0.wireOp",EDGE,"E0.bottom");var subQ2=makeQuery(id+"F0.imprint","INTERSECT",VERTEX,{"derivedFrom":[subQ1,subQ0]});Q60=makeQuery(id+"F0.imprint","IMPRINT",FACE,{"disambiguationData":[TD([[makeQuery(id+"F0.imprint","IMPRINT",EDGE,{"disambiguationData":[TD([[subQ2,-1.0]])],"derivedFrom":subQ1}),1.0]])]});}
            var Q61;
            {var subQ0=sQuery(id+"F0.wireOp",EDGE,"E12.2.0.27");var subQ1=sQuery(id+"F0.wireOp",EDGE,"E12.2.0.0");var subQ2=makeQuery(id+"F0.imprint","INTERSECT",VERTEX,{"derivedFrom":[subQ1,subQ0]});Q61=makeQuery(id+"F0.imprint","IMPRINT",FACE,{"disambiguationData":[TD([[makeQuery(id+"F0.imprint","IMPRINT",EDGE,{"disambiguationData":[TD([[subQ2,-1.0]])],"derivedFrom":subQ1}),1.0]])]});}
            var Q62;
            {var subQ0=sQuery(id+"F0.wireOp",EDGE,"E12.1.0.21");var subQ1=sQuery(id+"F0.wireOp",EDGE,"E12.1.0.16");var subQ2=makeQuery(id+"F0.imprint","INTERSECT",VERTEX,{"derivedFrom":[subQ1,subQ0]});Q62=makeQuery(id+"F0.imprint","IMPRINT",FACE,{"disambiguationData":[TD([[makeQuery(id+"F0.imprint","IMPRINT",EDGE,{"disambiguationData":[TD([[subQ2,-1.0]])],"derivedFrom":subQ1}),1.0]])]});}
            var Q63;
            {var subQ0=sQuery(id+"F0.wireOp",EDGE,"E12.1.0.27");var subQ1=sQuery(id+"F0.wireOp",EDGE,"E12.1.0.0");var subQ2=makeQuery(id+"F0.imprint","INTERSECT",VERTEX,{"derivedFrom":[subQ1,subQ0]});Q63=makeQuery(id+"F0.imprint","IMPRINT",FACE,{"disambiguationData":[TD([[makeQuery(id+"F0.imprint","IMPRINT",EDGE,{"disambiguationData":[TD([[subQ2,-1.0]])],"derivedFrom":subQ1}),1.0]])]});}
            var Q64;
            {var subQ0=sQuery(id+"F0.wireOp",EDGE,"E12.3.0.21");var subQ1=sQuery(id+"F0.wireOp",EDGE,"E12.3.0.16");var subQ2=makeQuery(id+"F0.imprint","INTERSECT",VERTEX,{"derivedFrom":[subQ1,subQ0]});Q64=makeQuery(id+"F0.imprint","IMPRINT",FACE,{"disambiguationData":[TD([[makeQuery(id+"F0.imprint","IMPRINT",EDGE,{"disambiguationData":[TD([[subQ2,-1.0]])],"derivedFrom":subQ1}),1.0]])]});}
            var Q65;
            {var subQ0=sQuery(id+"F0.wireOp",EDGE,"E12.3.0.27");var subQ1=sQuery(id+"F0.wireOp",EDGE,"E12.3.0.0");var subQ2=makeQuery(id+"F0.imprint","INTERSECT",VERTEX,{"derivedFrom":[subQ1,subQ0]});Q65=makeQuery(id+"F0.imprint","IMPRINT",FACE,{"disambiguationData":[TD([[makeQuery(id+"F0.imprint","IMPRINT",EDGE,{"disambiguationData":[TD([[subQ2,-1.0]])],"derivedFrom":subQ1}),1.0]])]});}
            var Q66;
            {var subQ0=sQuery(id+"F0.wireOp",EDGE,"E12.2.0.21");var subQ1=sQuery(id+"F0.wireOp",EDGE,"E12.2.0.16");var subQ2=makeQuery(id+"F0.imprint","INTERSECT",VERTEX,{"derivedFrom":[subQ1,subQ0]});Q66=makeQuery(id+"F0.imprint","IMPRINT",FACE,{"disambiguationData":[TD([[makeQuery(id+"F0.imprint","IMPRINT",EDGE,{"disambiguationData":[TD([[subQ2,-1.0]])],"derivedFrom":subQ1}),1.0]])]});}
            var Q67;
            {var subQ0=sQuery(id+"F0.wireOp",EDGE,"E12.4.0.21");var subQ1=sQuery(id+"F0.wireOp",EDGE,"E12.4.0.16");var subQ2=makeQuery(id+"F0.imprint","INTERSECT",VERTEX,{"derivedFrom":[subQ1,subQ0]});Q67=makeQuery(id+"F0.imprint","IMPRINT",FACE,{"disambiguationData":[TD([[makeQuery(id+"F0.imprint","IMPRINT",EDGE,{"disambiguationData":[TD([[subQ2,-1.0]])],"derivedFrom":subQ1}),1.0]])]});}
            var Q68;
            {var subQ0=sQuery(id+"F0.wireOp",EDGE,"E12.4.0.27");var subQ1=sQuery(id+"F0.wireOp",EDGE,"E12.4.0.0");var subQ2=makeQuery(id+"F0.imprint","INTERSECT",VERTEX,{"derivedFrom":[subQ1,subQ0]});Q68=makeQuery(id+"F0.imprint","IMPRINT",FACE,{"disambiguationData":[TD([[makeQuery(id+"F0.imprint","IMPRINT",EDGE,{"disambiguationData":[TD([[subQ2,-1.0]])],"derivedFrom":subQ1}),1.0]])]});}
            var Q69;
            {var subQ0=sQuery(id+"F0.wireOp",EDGE,"E12.6.0.27");var subQ1=sQuery(id+"F0.wireOp",EDGE,"E12.6.0.0");var subQ2=makeQuery(id+"F0.imprint","INTERSECT",VERTEX,{"derivedFrom":[subQ1,subQ0]});Q69=makeQuery(id+"F0.imprint","IMPRINT",FACE,{"disambiguationData":[TD([[makeQuery(id+"F0.imprint","IMPRINT",EDGE,{"disambiguationData":[TD([[subQ2,-1.0]])],"derivedFrom":subQ1}),1.0]])]});}
            var Q70;
            {var subQ0=sQuery(id+"F0.wireOp",EDGE,"E12.5.0.21");var subQ1=sQuery(id+"F0.wireOp",EDGE,"E12.5.0.16");var subQ2=makeQuery(id+"F0.imprint","INTERSECT",VERTEX,{"derivedFrom":[subQ1,subQ0]});Q70=makeQuery(id+"F0.imprint","IMPRINT",FACE,{"disambiguationData":[TD([[makeQuery(id+"F0.imprint","IMPRINT",EDGE,{"disambiguationData":[TD([[subQ2,-1.0]])],"derivedFrom":subQ1}),1.0]])]});}
            var Q71;
            {var subQ0=sQuery(id+"F0.wireOp",EDGE,"E12.5.0.27");var subQ1=sQuery(id+"F0.wireOp",EDGE,"E12.5.0.0");var subQ2=makeQuery(id+"F0.imprint","INTERSECT",VERTEX,{"derivedFrom":[subQ1,subQ0]});Q71=makeQuery(id+"F0.imprint","IMPRINT",FACE,{"disambiguationData":[TD([[makeQuery(id+"F0.imprint","IMPRINT",EDGE,{"disambiguationData":[TD([[subQ2,-1.0]])],"derivedFrom":subQ1}),1.0]])]});}
            var Q72;
            {var subQ0=sQuery(id+"F0.wireOp",EDGE,"E12.7.0.21");var subQ1=sQuery(id+"F0.wireOp",EDGE,"E12.7.0.16");var subQ2=makeQuery(id+"F0.imprint","INTERSECT",VERTEX,{"derivedFrom":[subQ1,subQ0]});Q72=makeQuery(id+"F0.imprint","IMPRINT",FACE,{"disambiguationData":[TD([[makeQuery(id+"F0.imprint","IMPRINT",EDGE,{"disambiguationData":[TD([[subQ2,-1.0]])],"derivedFrom":subQ1}),1.0]])]});}
            var Q73;
            {var subQ0=sQuery(id+"F0.wireOp",EDGE,"E12.7.0.27");var subQ1=sQuery(id+"F0.wireOp",EDGE,"E12.7.0.0");var subQ2=makeQuery(id+"F0.imprint","INTERSECT",VERTEX,{"derivedFrom":[subQ1,subQ0]});Q73=makeQuery(id+"F0.imprint","IMPRINT",FACE,{"disambiguationData":[TD([[makeQuery(id+"F0.imprint","IMPRINT",EDGE,{"disambiguationData":[TD([[subQ2,-1.0]])],"derivedFrom":subQ1}),1.0]])]});}
            var Q74;
            {var subQ0=sQuery(id+"F0.wireOp",EDGE,"E12.6.0.21");var subQ1=sQuery(id+"F0.wireOp",EDGE,"E12.6.0.16");var subQ2=makeQuery(id+"F0.imprint","INTERSECT",VERTEX,{"derivedFrom":[subQ1,subQ0]});Q74=makeQuery(id+"F0.imprint","IMPRINT",FACE,{"disambiguationData":[TD([[makeQuery(id+"F0.imprint","IMPRINT",EDGE,{"disambiguationData":[TD([[subQ2,-1.0]])],"derivedFrom":subQ1}),1.0]])]});}
            var Q75;
            {var subQ5=sQuery(id+"F0.wireOp",EDGE,"E12.1.0.37");Q75=makeQuery(id+"F0.imprint","IMPRINT",FACE,{"disambiguationData":[TD([[makeQuery(id+"F0.imprint","IMPRINT",EDGE,{"derivedFrom":subQ5}),-1.0]])]});}
            var Q76;
            {var subQ5=sQuery(id+"F0.wireOp",EDGE,"E12.3.0.37");Q76=makeQuery(id+"F0.imprint","IMPRINT",FACE,{"disambiguationData":[TD([[makeQuery(id+"F0.imprint","IMPRINT",EDGE,{"derivedFrom":subQ5}),-1.0]])]});}
            var Q77;
            {var subQ5=sQuery(id+"F0.wireOp",EDGE,"E12.2.0.37");Q77=makeQuery(id+"F0.imprint","IMPRINT",FACE,{"disambiguationData":[TD([[makeQuery(id+"F0.imprint","IMPRINT",EDGE,{"derivedFrom":subQ5}),-1.0]])]});}
            var Q78;
            {var subQ5=sQuery(id+"F0.wireOp",EDGE,"E12.4.0.37");Q78=makeQuery(id+"F0.imprint","IMPRINT",FACE,{"disambiguationData":[TD([[makeQuery(id+"F0.imprint","IMPRINT",EDGE,{"derivedFrom":subQ5}),-1.0]])]});}
            var Q79;
            {var subQ5=sQuery(id+"F0.wireOp",EDGE,"E12.5.0.37");Q79=makeQuery(id+"F0.imprint","IMPRINT",FACE,{"disambiguationData":[TD([[makeQuery(id+"F0.imprint","IMPRINT",EDGE,{"derivedFrom":subQ5}),-1.0]])]});}
            var Q80;
            {var subQ5=sQuery(id+"F0.wireOp",EDGE,"E12.7.0.37");Q80=makeQuery(id+"F0.imprint","IMPRINT",FACE,{"disambiguationData":[TD([[makeQuery(id+"F0.imprint","IMPRINT",EDGE,{"derivedFrom":subQ5}),-1.0]])]});}
            var Q81;
            {var subQ5=sQuery(id+"F0.wireOp",EDGE,"E12.6.0.37");Q81=makeQuery(id+"F0.imprint","IMPRINT",FACE,{"disambiguationData":[TD([[makeQuery(id+"F0.imprint","IMPRINT",EDGE,{"derivedFrom":subQ5}),-1.0]])]});}
            var Q82;
            {var subQ5=sQuery(id+"F0.wireOp",EDGE,"E12.3.0.45");Q82=makeQuery(id+"F0.imprint","IMPRINT",FACE,{"disambiguationData":[TD([[makeQuery(id+"F0.imprint","IMPRINT",EDGE,{"derivedFrom":subQ5}),1.0]])]});}
            var Q83;
            {var subQ0=sQuery(id+"F0.wireOp",EDGE,"E9.top");var subQ1=sQuery(id+"F0.wireOp",EDGE,"E8.bottom");var subQ2=makeQuery(id+"F0.imprint","INTERSECT",VERTEX,{"derivedFrom":[subQ1,subQ0]});Q83=makeQuery(id+"F0.imprint","IMPRINT",FACE,{"disambiguationData":[TD([[makeQuery(id+"F0.imprint","IMPRINT",EDGE,{"disambiguationData":[TD([[subQ2,-1.0]])],"derivedFrom":subQ1}),1.0]])]});}
            var Q84;
            {var subQ5=sQuery(id+"F0.wireOp",EDGE,"E12.6.0.45");Q84=makeQuery(id+"F0.imprint","IMPRINT",FACE,{"disambiguationData":[TD([[makeQuery(id+"F0.imprint","IMPRINT",EDGE,{"derivedFrom":subQ5}),1.0]])]});}
            var Q85;
            {var subQ0=sQuery(id+"F0.wireOp",EDGE,"E3.top");var subQ1=sQuery(id+"F0.wireOp",EDGE,"E2.bottom");var subQ2=makeQuery(id+"F0.imprint","INTERSECT",VERTEX,{"derivedFrom":[subQ1,subQ0]});Q85=makeQuery(id+"F0.imprint","IMPRINT",FACE,{"disambiguationData":[TD([[makeQuery(id+"F0.imprint","IMPRINT",EDGE,{"disambiguationData":[TD([[subQ2,-1.0]])],"derivedFrom":subQ1}),1.0]])]});}
            var Q86;
            {var subQ0=sQuery(id+"F0.wireOp",EDGE,"E12.2.0.32");var subQ1=sQuery(id+"F0.wireOp",EDGE,"E12.2.0.5");var subQ2=makeQuery(id+"F0.imprint","INTERSECT",VERTEX,{"derivedFrom":[subQ1,subQ0]});Q86=makeQuery(id+"F0.imprint","IMPRINT",FACE,{"disambiguationData":[TD([[makeQuery(id+"F0.imprint","IMPRINT",EDGE,{"disambiguationData":[TD([[subQ2,-1.0]])],"derivedFrom":subQ1}),1.0]])]});}
            var Q87;
            {var subQ0=sQuery(id+"F0.wireOp",EDGE,"E12.4.0.32");var subQ1=sQuery(id+"F0.wireOp",EDGE,"E12.4.0.5");var subQ2=makeQuery(id+"F0.imprint","INTERSECT",VERTEX,{"derivedFrom":[subQ1,subQ0]});Q87=makeQuery(id+"F0.imprint","IMPRINT",FACE,{"disambiguationData":[TD([[makeQuery(id+"F0.imprint","IMPRINT",EDGE,{"disambiguationData":[TD([[subQ2,-1.0]])],"derivedFrom":subQ1}),1.0]])]});}
            var Q88;
            {var subQ0=sQuery(id+"F0.wireOp",EDGE,"E12.3.0.32");var subQ1=sQuery(id+"F0.wireOp",EDGE,"E12.3.0.5");var subQ2=makeQuery(id+"F0.imprint","INTERSECT",VERTEX,{"derivedFrom":[subQ1,subQ0]});Q88=makeQuery(id+"F0.imprint","IMPRINT",FACE,{"disambiguationData":[TD([[makeQuery(id+"F0.imprint","IMPRINT",EDGE,{"disambiguationData":[TD([[subQ2,-1.0]])],"derivedFrom":subQ1}),1.0]])]});}
            var Q89;
            {var subQ0=sQuery(id+"F0.wireOp",EDGE,"E12.5.0.32");var subQ1=sQuery(id+"F0.wireOp",EDGE,"E12.5.0.5");var subQ2=makeQuery(id+"F0.imprint","INTERSECT",VERTEX,{"derivedFrom":[subQ1,subQ0]});Q89=makeQuery(id+"F0.imprint","IMPRINT",FACE,{"disambiguationData":[TD([[makeQuery(id+"F0.imprint","IMPRINT",EDGE,{"disambiguationData":[TD([[subQ2,-1.0]])],"derivedFrom":subQ1}),1.0]])]});}
            var Q90;
            {var subQ0=sQuery(id+"F0.wireOp",EDGE,"E12.6.0.32");var subQ1=sQuery(id+"F0.wireOp",EDGE,"E12.6.0.5");var subQ2=makeQuery(id+"F0.imprint","INTERSECT",VERTEX,{"derivedFrom":[subQ1,subQ0]});Q90=makeQuery(id+"F0.imprint","IMPRINT",FACE,{"disambiguationData":[TD([[makeQuery(id+"F0.imprint","IMPRINT",EDGE,{"disambiguationData":[TD([[subQ2,-1.0]])],"derivedFrom":subQ1}),1.0]])]});}
            var Q91;
            {var subQ0=sQuery(id+"F0.wireOp",EDGE,"E12.7.0.32");var subQ1=sQuery(id+"F0.wireOp",EDGE,"E12.7.0.5");var subQ2=makeQuery(id+"F0.imprint","INTERSECT",VERTEX,{"derivedFrom":[subQ1,subQ0]});Q91=makeQuery(id+"F0.imprint","IMPRINT",FACE,{"disambiguationData":[TD([[makeQuery(id+"F0.imprint","IMPRINT",EDGE,{"disambiguationData":[TD([[subQ2,-1.0]])],"derivedFrom":subQ1}),1.0]])]});}
            var Q92;
            {var subQ0=sQuery(id+"F0.wireOp",EDGE,"E12.1.0.32");var subQ1=sQuery(id+"F0.wireOp",EDGE,"E12.1.0.5");var subQ2=makeQuery(id+"F0.imprint","INTERSECT",VERTEX,{"derivedFrom":[subQ1,subQ0]});Q92=makeQuery(id+"F0.imprint","IMPRINT",FACE,{"disambiguationData":[TD([[makeQuery(id+"F0.imprint","IMPRINT",EDGE,{"disambiguationData":[TD([[subQ2,-1.0]])],"derivedFrom":subQ1}),1.0]])]});}
            var Q93;
            {var subQ0=sQuery(id+"F0.wireOp",EDGE,"E5.top");var subQ1=sQuery(id+"F0.wireOp",EDGE,"E4.bottom");var subQ2=makeQuery(id+"F0.imprint","INTERSECT",VERTEX,{"derivedFrom":[subQ1,subQ0]});Q93=makeQuery(id+"F0.imprint","IMPRINT",FACE,{"disambiguationData":[TD([[makeQuery(id+"F0.imprint","IMPRINT",EDGE,{"disambiguationData":[TD([[subQ2,-1.0]])],"derivedFrom":subQ1}),1.0]])]});}
            var Q94;
            {var subQ5=sQuery(id+"F0.wireOp",EDGE,"E12.4.0.45");Q94=makeQuery(id+"F0.imprint","IMPRINT",FACE,{"disambiguationData":[TD([[makeQuery(id+"F0.imprint","IMPRINT",EDGE,{"derivedFrom":subQ5}),1.0]])]});}
            var Q95;
            {var subQ0=sQuery(id+"F0.wireOp",EDGE,"E12.5.0.23");var subQ1=sQuery(id+"F0.wireOp",EDGE,"E12.5.0.10");var subQ2=makeQuery(id+"F0.imprint","INTERSECT",VERTEX,{"derivedFrom":[subQ1,subQ0]});Q95=makeQuery(id+"F0.imprint","IMPRINT",FACE,{"disambiguationData":[TD([[makeQuery(id+"F0.imprint","IMPRINT",EDGE,{"disambiguationData":[TD([[subQ2,-1.0]])],"derivedFrom":subQ1}),1.0]])]});}
            var Q96;
            {var subQ0=sQuery(id+"F0.wireOp",EDGE,"E12.6.0.23");var subQ1=sQuery(id+"F0.wireOp",EDGE,"E12.6.0.10");var subQ2=makeQuery(id+"F0.imprint","INTERSECT",VERTEX,{"derivedFrom":[subQ1,subQ0]});Q96=makeQuery(id+"F0.imprint","IMPRINT",FACE,{"disambiguationData":[TD([[makeQuery(id+"F0.imprint","IMPRINT",EDGE,{"disambiguationData":[TD([[subQ2,-1.0]])],"derivedFrom":subQ1}),1.0]])]});}
            var Q97;
            {var subQ0=sQuery(id+"F0.wireOp",EDGE,"E12.7.0.23");var subQ1=sQuery(id+"F0.wireOp",EDGE,"E12.7.0.10");var subQ2=makeQuery(id+"F0.imprint","INTERSECT",VERTEX,{"derivedFrom":[subQ1,subQ0]});Q97=makeQuery(id+"F0.imprint","IMPRINT",FACE,{"disambiguationData":[TD([[makeQuery(id+"F0.imprint","IMPRINT",EDGE,{"disambiguationData":[TD([[subQ2,-1.0]])],"derivedFrom":subQ1}),1.0]])]});}
            var Q98;
            {var subQ0=sQuery(id+"F0.wireOp",EDGE,"E12.1.0.23");var subQ1=sQuery(id+"F0.wireOp",EDGE,"E12.1.0.10");var subQ2=makeQuery(id+"F0.imprint","INTERSECT",VERTEX,{"derivedFrom":[subQ1,subQ0]});Q98=makeQuery(id+"F0.imprint","IMPRINT",FACE,{"disambiguationData":[TD([[makeQuery(id+"F0.imprint","IMPRINT",EDGE,{"disambiguationData":[TD([[subQ2,-1.0]])],"derivedFrom":subQ1}),1.0]])]});}
            var Q99;
            {var subQ0=sQuery(id+"F0.wireOp",EDGE,"E12.2.0.23");var subQ1=sQuery(id+"F0.wireOp",EDGE,"E12.2.0.10");var subQ2=makeQuery(id+"F0.imprint","INTERSECT",VERTEX,{"derivedFrom":[subQ1,subQ0]});Q99=makeQuery(id+"F0.imprint","IMPRINT",FACE,{"disambiguationData":[TD([[makeQuery(id+"F0.imprint","IMPRINT",EDGE,{"disambiguationData":[TD([[subQ2,-1.0]])],"derivedFrom":subQ1}),1.0]])]});}
            var Q100;
            {var subQ0=sQuery(id+"F0.wireOp",EDGE,"E12.4.0.23");var subQ1=sQuery(id+"F0.wireOp",EDGE,"E12.4.0.10");var subQ2=makeQuery(id+"F0.imprint","INTERSECT",VERTEX,{"derivedFrom":[subQ1,subQ0]});Q100=makeQuery(id+"F0.imprint","IMPRINT",FACE,{"disambiguationData":[TD([[makeQuery(id+"F0.imprint","IMPRINT",EDGE,{"disambiguationData":[TD([[subQ2,-1.0]])],"derivedFrom":subQ1}),1.0]])]});}
            var Q101;
            {var subQ0=sQuery(id+"F0.wireOp",EDGE,"E12.3.0.23");var subQ1=sQuery(id+"F0.wireOp",EDGE,"E12.3.0.10");var subQ2=makeQuery(id+"F0.imprint","INTERSECT",VERTEX,{"derivedFrom":[subQ1,subQ0]});Q101=makeQuery(id+"F0.imprint","IMPRINT",FACE,{"disambiguationData":[TD([[makeQuery(id+"F0.imprint","IMPRINT",EDGE,{"disambiguationData":[TD([[subQ2,-1.0]])],"derivedFrom":subQ1}),1.0]])]});}
            var Q102;
            {var subQ5=sQuery(id+"F0.wireOp",EDGE,"E12.7.0.45");Q102=makeQuery(id+"F0.imprint","IMPRINT",FACE,{"disambiguationData":[TD([[makeQuery(id+"F0.imprint","IMPRINT",EDGE,{"derivedFrom":subQ5}),1.0]])]});}
            var Q103;
            {var subQ0=sQuery(id+"F0.wireOp",EDGE,"E6.left");Q103=makeQuery(id+"F0.imprint","IMPRINT",FACE,{"disambiguationData":[TD([[makeQuery(id+"F0.imprint","IMPRINT",EDGE,{"derivedFrom":subQ0}),1.0]])]});}
            var Q104;
            {var subQ5=sQuery(id+"F0.wireOp",EDGE,"E7.right");Q104=makeQuery(id+"F0.imprint","IMPRINT",FACE,{"disambiguationData":[TD([[makeQuery(id+"F0.imprint","IMPRINT",EDGE,{"derivedFrom":subQ5}),-1.0]])]});}
            var Q105;
            {var subQ5=sQuery(id+"F0.wireOp",EDGE,"E12.1.0.40");Q105=makeQuery(id+"F0.imprint","IMPRINT",FACE,{"disambiguationData":[TD([[makeQuery(id+"F0.imprint","IMPRINT",EDGE,{"derivedFrom":subQ5}),-1.0]])]});}
            var Q106;
            {var subQ5=sQuery(id+"F0.wireOp",EDGE,"E12.3.0.40");Q106=makeQuery(id+"F0.imprint","IMPRINT",FACE,{"disambiguationData":[TD([[makeQuery(id+"F0.imprint","IMPRINT",EDGE,{"derivedFrom":subQ5}),-1.0]])]});}
            var Q107;
            {var subQ5=sQuery(id+"F0.wireOp",EDGE,"E12.2.0.40");Q107=makeQuery(id+"F0.imprint","IMPRINT",FACE,{"disambiguationData":[TD([[makeQuery(id+"F0.imprint","IMPRINT",EDGE,{"derivedFrom":subQ5}),-1.0]])]});}
            var Q108;
            {var subQ5=sQuery(id+"F0.wireOp",EDGE,"E12.4.0.40");Q108=makeQuery(id+"F0.imprint","IMPRINT",FACE,{"disambiguationData":[TD([[makeQuery(id+"F0.imprint","IMPRINT",EDGE,{"derivedFrom":subQ5}),-1.0]])]});}
            var Q109;
            {var subQ5=sQuery(id+"F0.wireOp",EDGE,"E12.5.0.40");Q109=makeQuery(id+"F0.imprint","IMPRINT",FACE,{"disambiguationData":[TD([[makeQuery(id+"F0.imprint","IMPRINT",EDGE,{"derivedFrom":subQ5}),-1.0]])]});}
            var Q110;
            {var subQ5=sQuery(id+"F0.wireOp",EDGE,"E12.7.0.40");Q110=makeQuery(id+"F0.imprint","IMPRINT",FACE,{"disambiguationData":[TD([[makeQuery(id+"F0.imprint","IMPRINT",EDGE,{"derivedFrom":subQ5}),-1.0]])]});}
            var Q111;
            {var subQ5=sQuery(id+"F0.wireOp",EDGE,"E12.6.0.40");Q111=makeQuery(id+"F0.imprint","IMPRINT",FACE,{"disambiguationData":[TD([[makeQuery(id+"F0.imprint","IMPRINT",EDGE,{"derivedFrom":subQ5}),-1.0]])]});}
            var Q112;
            {var subQ5=sQuery(id+"F0.wireOp",EDGE,"E4.right");Q112=makeQuery(id+"F0.imprint","IMPRINT",FACE,{"disambiguationData":[TD([[makeQuery(id+"F0.imprint","IMPRINT",EDGE,{"derivedFrom":subQ5}),-1.0]])]});}
            var Q113;
            {var subQ5=sQuery(id+"F0.wireOp",EDGE,"E8.right");Q113=makeQuery(id+"F0.imprint","IMPRINT",FACE,{"disambiguationData":[TD([[makeQuery(id+"F0.imprint","IMPRINT",EDGE,{"derivedFrom":subQ5}),-1.0]])]});}
            var Q114;
            {var subQ5=sQuery(id+"F0.wireOp",EDGE,"E1.right");Q114=makeQuery(id+"F0.imprint","IMPRINT",FACE,{"disambiguationData":[TD([[makeQuery(id+"F0.imprint","IMPRINT",EDGE,{"derivedFrom":subQ5}),-1.0]])]});}
            var Q115;
            {var subQ5=sQuery(id+"F0.wireOp",EDGE,"E12.2.0.38");Q115=makeQuery(id+"F0.imprint","IMPRINT",FACE,{"disambiguationData":[TD([[makeQuery(id+"F0.imprint","IMPRINT",EDGE,{"derivedFrom":subQ5}),-1.0]])]});}
            var Q116;
            {var subQ5=sQuery(id+"F0.wireOp",EDGE,"E12.1.0.38");Q116=makeQuery(id+"F0.imprint","IMPRINT",FACE,{"disambiguationData":[TD([[makeQuery(id+"F0.imprint","IMPRINT",EDGE,{"derivedFrom":subQ5}),-1.0]])]});}
            var Q117;
            {var subQ5=sQuery(id+"F0.wireOp",EDGE,"E12.3.0.38");Q117=makeQuery(id+"F0.imprint","IMPRINT",FACE,{"disambiguationData":[TD([[makeQuery(id+"F0.imprint","IMPRINT",EDGE,{"derivedFrom":subQ5}),-1.0]])]});}
            var Q118;
            {var subQ5=sQuery(id+"F0.wireOp",EDGE,"E12.4.0.38");Q118=makeQuery(id+"F0.imprint","IMPRINT",FACE,{"disambiguationData":[TD([[makeQuery(id+"F0.imprint","IMPRINT",EDGE,{"derivedFrom":subQ5}),-1.0]])]});}
            var Q119;
            {var subQ5=sQuery(id+"F0.wireOp",EDGE,"E12.6.0.38");Q119=makeQuery(id+"F0.imprint","IMPRINT",FACE,{"disambiguationData":[TD([[makeQuery(id+"F0.imprint","IMPRINT",EDGE,{"derivedFrom":subQ5}),-1.0]])]});}
            var Q120;
            {var subQ5=sQuery(id+"F0.wireOp",EDGE,"E12.5.0.38");Q120=makeQuery(id+"F0.imprint","IMPRINT",FACE,{"disambiguationData":[TD([[makeQuery(id+"F0.imprint","IMPRINT",EDGE,{"derivedFrom":subQ5}),-1.0]])]});}
            var Q121;
            {var subQ5=sQuery(id+"F0.wireOp",EDGE,"E12.7.0.38");Q121=makeQuery(id+"F0.imprint","IMPRINT",FACE,{"disambiguationData":[TD([[makeQuery(id+"F0.imprint","IMPRINT",EDGE,{"derivedFrom":subQ5}),-1.0]])]});}
            var Q122;
            {var subQ0=sQuery(id+"F0.wireOp",EDGE,"E0.left");Q122=makeQuery(id+"F0.imprint","IMPRINT",FACE,{"disambiguationData":[TD([[makeQuery(id+"F0.imprint","IMPRINT",EDGE,{"derivedFrom":subQ0}),1.0]])]});}
            var Q123;
            {var subQ0=sQuery(id+"F0.wireOp",EDGE,"E12.1.0.43");Q123=makeQuery(id+"F0.imprint","IMPRINT",FACE,{"disambiguationData":[TD([[makeQuery(id+"F0.imprint","IMPRINT",EDGE,{"derivedFrom":subQ0}),-1.0]])]});}
            var Q124;
            {var subQ5=sQuery(id+"F0.wireOp",EDGE,"E9.right");Q124=makeQuery(id+"F0.imprint","IMPRINT",FACE,{"disambiguationData":[TD([[makeQuery(id+"F0.imprint","IMPRINT",EDGE,{"derivedFrom":subQ5}),-1.0]])]});}
            var Q125;
            {var subQ3=sQuery(id+"F0.wireOp",EDGE,"E12.1.0.48");Q125=makeQuery(id+"F0.imprint","IMPRINT",FACE,{"disambiguationData":[TD([[makeQuery(id+"F0.imprint","IMPRINT",EDGE,{"derivedFrom":subQ3}),1.0]])]});}
            var Q126;
            {var subQ3=sQuery(id+"F0.wireOp",EDGE,"E12.1.0.51");Q126=makeQuery(id+"F0.imprint","IMPRINT",FACE,{"disambiguationData":[TD([[makeQuery(id+"F0.imprint","IMPRINT",EDGE,{"derivedFrom":subQ3}),1.0]])]});}
            var Q127;
            {var subQ0=sQuery(id+"F0.wireOp",EDGE,"E8.left");Q127=makeQuery(id+"F0.imprint","IMPRINT",FACE,{"disambiguationData":[TD([[makeQuery(id+"F0.imprint","IMPRINT",EDGE,{"derivedFrom":subQ0}),1.0]])]});}
            var Q128;
            {var subQ5=sQuery(id+"F0.wireOp",EDGE,"E12.2.0.39");Q128=makeQuery(id+"F0.imprint","IMPRINT",FACE,{"disambiguationData":[TD([[makeQuery(id+"F0.imprint","IMPRINT",EDGE,{"derivedFrom":subQ5}),-1.0]])]});}
            var Q129;
            {var subQ4=sQuery(id+"F0.wireOp",EDGE,"E12.1.0.52");Q129=makeQuery(id+"F0.imprint","IMPRINT",FACE,{"disambiguationData":[TD([[makeQuery(id+"F0.imprint","IMPRINT",EDGE,{"derivedFrom":subQ4}),1.0]])]});}
            var Q130;
            {var subQ5=sQuery(id+"F0.wireOp",EDGE,"E12.1.0.39");Q130=makeQuery(id+"F0.imprint","IMPRINT",FACE,{"disambiguationData":[TD([[makeQuery(id+"F0.imprint","IMPRINT",EDGE,{"derivedFrom":subQ5}),-1.0]])]});}
            var Q131;
            {var subQ4=sQuery(id+"F0.wireOp",EDGE,"E12.3.0.52");Q131=makeQuery(id+"F0.imprint","IMPRINT",FACE,{"disambiguationData":[TD([[makeQuery(id+"F0.imprint","IMPRINT",EDGE,{"derivedFrom":subQ4}),1.0]])]});}
            var Q132;
            {var subQ5=sQuery(id+"F0.wireOp",EDGE,"E12.3.0.39");Q132=makeQuery(id+"F0.imprint","IMPRINT",FACE,{"disambiguationData":[TD([[makeQuery(id+"F0.imprint","IMPRINT",EDGE,{"derivedFrom":subQ5}),-1.0]])]});}
            var Q133;
            {var subQ4=sQuery(id+"F0.wireOp",EDGE,"E12.2.0.52");Q133=makeQuery(id+"F0.imprint","IMPRINT",FACE,{"disambiguationData":[TD([[makeQuery(id+"F0.imprint","IMPRINT",EDGE,{"derivedFrom":subQ4}),1.0]])]});}
            var Q134;
            {var subQ4=sQuery(id+"F0.wireOp",EDGE,"E12.4.0.52");Q134=makeQuery(id+"F0.imprint","IMPRINT",FACE,{"disambiguationData":[TD([[makeQuery(id+"F0.imprint","IMPRINT",EDGE,{"derivedFrom":subQ4}),1.0]])]});}
            var Q135;
            {var subQ5=sQuery(id+"F0.wireOp",EDGE,"E12.4.0.39");Q135=makeQuery(id+"F0.imprint","IMPRINT",FACE,{"disambiguationData":[TD([[makeQuery(id+"F0.imprint","IMPRINT",EDGE,{"derivedFrom":subQ5}),-1.0]])]});}
            var Q136;
            {var subQ5=sQuery(id+"F0.wireOp",EDGE,"E12.6.0.39");Q136=makeQuery(id+"F0.imprint","IMPRINT",FACE,{"disambiguationData":[TD([[makeQuery(id+"F0.imprint","IMPRINT",EDGE,{"derivedFrom":subQ5}),-1.0]])]});}
            var Q137;
            {var subQ4=sQuery(id+"F0.wireOp",EDGE,"E12.5.0.52");Q137=makeQuery(id+"F0.imprint","IMPRINT",FACE,{"disambiguationData":[TD([[makeQuery(id+"F0.imprint","IMPRINT",EDGE,{"derivedFrom":subQ4}),1.0]])]});}
            var Q138;
            {var subQ5=sQuery(id+"F0.wireOp",EDGE,"E12.5.0.39");Q138=makeQuery(id+"F0.imprint","IMPRINT",FACE,{"disambiguationData":[TD([[makeQuery(id+"F0.imprint","IMPRINT",EDGE,{"derivedFrom":subQ5}),-1.0]])]});}
            var Q139;
            {var subQ4=sQuery(id+"F0.wireOp",EDGE,"E12.7.0.52");Q139=makeQuery(id+"F0.imprint","IMPRINT",FACE,{"disambiguationData":[TD([[makeQuery(id+"F0.imprint","IMPRINT",EDGE,{"derivedFrom":subQ4}),1.0]])]});}
            var Q140;
            {var subQ5=sQuery(id+"F0.wireOp",EDGE,"E12.7.0.39");Q140=makeQuery(id+"F0.imprint","IMPRINT",FACE,{"disambiguationData":[TD([[makeQuery(id+"F0.imprint","IMPRINT",EDGE,{"derivedFrom":subQ5}),-1.0]])]});}
            var Q141;
            {var subQ4=sQuery(id+"F0.wireOp",EDGE,"E12.6.0.52");Q141=makeQuery(id+"F0.imprint","IMPRINT",FACE,{"disambiguationData":[TD([[makeQuery(id+"F0.imprint","IMPRINT",EDGE,{"derivedFrom":subQ4}),1.0]])]});}
            var Q142;
            {var subQ4=sQuery(id+"F0.wireOp",EDGE,"E12.4.0.50");Q142=makeQuery(id+"F0.imprint","IMPRINT",FACE,{"disambiguationData":[TD([[makeQuery(id+"F0.imprint","IMPRINT",EDGE,{"derivedFrom":subQ4}),1.0]])]});}
            var Q143;
            {var subQ4=sQuery(id+"F0.wireOp",EDGE,"E12.5.0.50");Q143=makeQuery(id+"F0.imprint","IMPRINT",FACE,{"disambiguationData":[TD([[makeQuery(id+"F0.imprint","IMPRINT",EDGE,{"derivedFrom":subQ4}),1.0]])]});}
            var Q144;
            {var subQ4=sQuery(id+"F0.wireOp",EDGE,"E12.7.0.50");Q144=makeQuery(id+"F0.imprint","IMPRINT",FACE,{"disambiguationData":[TD([[makeQuery(id+"F0.imprint","IMPRINT",EDGE,{"derivedFrom":subQ4}),1.0]])]});}
            var Q145;
            {var subQ4=sQuery(id+"F0.wireOp",EDGE,"E12.6.0.50");Q145=makeQuery(id+"F0.imprint","IMPRINT",FACE,{"disambiguationData":[TD([[makeQuery(id+"F0.imprint","IMPRINT",EDGE,{"derivedFrom":subQ4}),1.0]])]});}
            var Q146;
            {var subQ0=sQuery(id+"F0.wireOp",EDGE,"E12.1.0.49");Q146=makeQuery(id+"F0.imprint","IMPRINT",FACE,{"disambiguationData":[TD([[makeQuery(id+"F0.imprint","IMPRINT",EDGE,{"derivedFrom":subQ0}),1.0]])]});}
            var Q147;
            {var subQ0=sQuery(id+"F0.wireOp",EDGE,"E12.3.0.43");Q147=makeQuery(id+"F0.imprint","IMPRINT",FACE,{"disambiguationData":[TD([[makeQuery(id+"F0.imprint","IMPRINT",EDGE,{"derivedFrom":subQ0}),-1.0]])]});}
            var Q148;
            {var subQ5=sQuery(id+"F0.wireOp",EDGE,"E3.right");Q148=makeQuery(id+"F0.imprint","IMPRINT",FACE,{"disambiguationData":[TD([[makeQuery(id+"F0.imprint","IMPRINT",EDGE,{"derivedFrom":subQ5}),-1.0]])]});}
            var Q149;
            {var subQ5=sQuery(id+"F0.wireOp",EDGE,"E11.right");Q149=makeQuery(id+"F0.imprint","IMPRINT",FACE,{"disambiguationData":[TD([[makeQuery(id+"F0.imprint","IMPRINT",EDGE,{"derivedFrom":subQ5}),-1.0]])]});}
            var Q150;
            {var subQ5=sQuery(id+"F0.wireOp",EDGE,"E12.4.0.42");Q150=makeQuery(id+"F0.imprint","IMPRINT",FACE,{"disambiguationData":[TD([[makeQuery(id+"F0.imprint","IMPRINT",EDGE,{"derivedFrom":subQ5}),-1.0]])]});}
            var Q151;
            {var subQ5=sQuery(id+"F0.wireOp",EDGE,"E12.3.0.42");Q151=makeQuery(id+"F0.imprint","IMPRINT",FACE,{"disambiguationData":[TD([[makeQuery(id+"F0.imprint","IMPRINT",EDGE,{"derivedFrom":subQ5}),-1.0]])]});}
            var Q152;
            {var subQ5=sQuery(id+"F0.wireOp",EDGE,"E12.5.0.42");Q152=makeQuery(id+"F0.imprint","IMPRINT",FACE,{"disambiguationData":[TD([[makeQuery(id+"F0.imprint","IMPRINT",EDGE,{"derivedFrom":subQ5}),-1.0]])]});}
            var Q153;
            {var subQ5=sQuery(id+"F0.wireOp",EDGE,"E12.6.0.42");Q153=makeQuery(id+"F0.imprint","IMPRINT",FACE,{"disambiguationData":[TD([[makeQuery(id+"F0.imprint","IMPRINT",EDGE,{"derivedFrom":subQ5}),-1.0]])]});}
            var Q154;
            {var subQ5=sQuery(id+"F0.wireOp",EDGE,"E12.7.0.42");Q154=makeQuery(id+"F0.imprint","IMPRINT",FACE,{"disambiguationData":[TD([[makeQuery(id+"F0.imprint","IMPRINT",EDGE,{"derivedFrom":subQ5}),-1.0]])]});}
            var Q155;
            {var subQ0=sQuery(id+"F0.wireOp",EDGE,"E12.4.0.43");Q155=makeQuery(id+"F0.imprint","IMPRINT",FACE,{"disambiguationData":[TD([[makeQuery(id+"F0.imprint","IMPRINT",EDGE,{"derivedFrom":subQ0}),-1.0]])]});}
            var Q156;
            {var subQ5=sQuery(id+"F0.wireOp",EDGE,"E12.1.0.42");Q156=makeQuery(id+"F0.imprint","IMPRINT",FACE,{"disambiguationData":[TD([[makeQuery(id+"F0.imprint","IMPRINT",EDGE,{"derivedFrom":subQ5}),-1.0]])]});}
            var Q157;
            {var subQ5=sQuery(id+"F0.wireOp",EDGE,"E12.2.0.42");Q157=makeQuery(id+"F0.imprint","IMPRINT",FACE,{"disambiguationData":[TD([[makeQuery(id+"F0.imprint","IMPRINT",EDGE,{"derivedFrom":subQ5}),-1.0]])]});}
            var Q158;
            {var subQ5=sQuery(id+"F0.wireOp",EDGE,"E5.right");Q158=makeQuery(id+"F0.imprint","IMPRINT",FACE,{"disambiguationData":[TD([[makeQuery(id+"F0.imprint","IMPRINT",EDGE,{"derivedFrom":subQ5}),-1.0]])]});}
            var Q159;
            {var subQ5=sQuery(id+"F0.wireOp",EDGE,"E12.6.0.41");Q159=makeQuery(id+"F0.imprint","IMPRINT",FACE,{"disambiguationData":[TD([[makeQuery(id+"F0.imprint","IMPRINT",EDGE,{"derivedFrom":subQ5}),-1.0]])]});}
            var Q160;
            {var subQ5=sQuery(id+"F0.wireOp",EDGE,"E12.7.0.41");Q160=makeQuery(id+"F0.imprint","IMPRINT",FACE,{"disambiguationData":[TD([[makeQuery(id+"F0.imprint","IMPRINT",EDGE,{"derivedFrom":subQ5}),-1.0]])]});}
            var Q161;
            {var subQ0=sQuery(id+"F0.wireOp",EDGE,"E12.5.0.43");Q161=makeQuery(id+"F0.imprint","IMPRINT",FACE,{"disambiguationData":[TD([[makeQuery(id+"F0.imprint","IMPRINT",EDGE,{"derivedFrom":subQ0}),-1.0]])]});}
            var Q162;
            {var subQ0=sQuery(id+"F0.wireOp",EDGE,"E4.left");Q162=makeQuery(id+"F0.imprint","IMPRINT",FACE,{"disambiguationData":[TD([[makeQuery(id+"F0.imprint","IMPRINT",EDGE,{"derivedFrom":subQ0}),1.0]])]});}
            var Q163;
            {var subQ5=sQuery(id+"F0.wireOp",EDGE,"E12.1.0.41");Q163=makeQuery(id+"F0.imprint","IMPRINT",FACE,{"disambiguationData":[TD([[makeQuery(id+"F0.imprint","IMPRINT",EDGE,{"derivedFrom":subQ5}),-1.0]])]});}
            var Q164;
            {var subQ5=sQuery(id+"F0.wireOp",EDGE,"E12.2.0.41");Q164=makeQuery(id+"F0.imprint","IMPRINT",FACE,{"disambiguationData":[TD([[makeQuery(id+"F0.imprint","IMPRINT",EDGE,{"derivedFrom":subQ5}),-1.0]])]});}
            var Q165;
            {var subQ5=sQuery(id+"F0.wireOp",EDGE,"E12.4.0.41");Q165=makeQuery(id+"F0.imprint","IMPRINT",FACE,{"disambiguationData":[TD([[makeQuery(id+"F0.imprint","IMPRINT",EDGE,{"derivedFrom":subQ5}),-1.0]])]});}
            var Q166;
            {var subQ5=sQuery(id+"F0.wireOp",EDGE,"E12.3.0.41");Q166=makeQuery(id+"F0.imprint","IMPRINT",FACE,{"disambiguationData":[TD([[makeQuery(id+"F0.imprint","IMPRINT",EDGE,{"derivedFrom":subQ5}),-1.0]])]});}
            var Q167;
            {var subQ5=sQuery(id+"F0.wireOp",EDGE,"E12.5.0.41");Q167=makeQuery(id+"F0.imprint","IMPRINT",FACE,{"disambiguationData":[TD([[makeQuery(id+"F0.imprint","IMPRINT",EDGE,{"derivedFrom":subQ5}),-1.0]])]});}
            var Q168;
            {var subQ0=sQuery(id+"F0.wireOp",EDGE,"E12.6.0.43");Q168=makeQuery(id+"F0.imprint","IMPRINT",FACE,{"disambiguationData":[TD([[makeQuery(id+"F0.imprint","IMPRINT",EDGE,{"derivedFrom":subQ0}),-1.0]])]});}
            var Q169;
            {var subQ3=sQuery(id+"F0.wireOp",EDGE,"E12.1.0.58");Q169=makeQuery(id+"F0.imprint","IMPRINT",FACE,{"disambiguationData":[TD([[makeQuery(id+"F0.imprint","IMPRINT",EDGE,{"derivedFrom":subQ3}),1.0]])]});}
            var Q170;
            {var subQ0=sQuery(id+"F0.wireOp",EDGE,"E12.7.0.43");Q170=makeQuery(id+"F0.imprint","IMPRINT",FACE,{"disambiguationData":[TD([[makeQuery(id+"F0.imprint","IMPRINT",EDGE,{"derivedFrom":subQ0}),-1.0]])]});}
            var Q171;
            {var subQ5=sQuery(id+"F0.wireOp",EDGE,"E2.right");Q171=makeQuery(id+"F0.imprint","IMPRINT",FACE,{"disambiguationData":[TD([[makeQuery(id+"F0.imprint","IMPRINT",EDGE,{"derivedFrom":subQ5}),-1.0]])]});}
            var Q172;
            {var subQ4=sQuery(id+"F0.wireOp",EDGE,"E12.1.0.50");Q172=makeQuery(id+"F0.imprint","IMPRINT",FACE,{"disambiguationData":[TD([[makeQuery(id+"F0.imprint","IMPRINT",EDGE,{"derivedFrom":subQ4}),1.0]])]});}
            var Q173;
            {var subQ3=sQuery(id+"F0.wireOp",EDGE,"E12.1.0.59");Q173=makeQuery(id+"F0.imprint","IMPRINT",FACE,{"disambiguationData":[TD([[makeQuery(id+"F0.imprint","IMPRINT",EDGE,{"derivedFrom":subQ3}),1.0]])]});}
            var Q174;
            {var subQ5=sQuery(id+"F0.wireOp",EDGE,"E10.right");Q174=makeQuery(id+"F0.imprint","IMPRINT",FACE,{"disambiguationData":[TD([[makeQuery(id+"F0.imprint","IMPRINT",EDGE,{"derivedFrom":subQ5}),-1.0]])]});}
            var Q175;
            {var subQ0=sQuery(id+"F0.wireOp",EDGE,"E12.5.0.49");Q175=makeQuery(id+"F0.imprint","IMPRINT",FACE,{"disambiguationData":[TD([[makeQuery(id+"F0.imprint","IMPRINT",EDGE,{"derivedFrom":subQ0}),1.0]])]});}
            var Q176;
            {var subQ0=sQuery(id+"F0.wireOp",EDGE,"E12.4.0.49");Q176=makeQuery(id+"F0.imprint","IMPRINT",FACE,{"disambiguationData":[TD([[makeQuery(id+"F0.imprint","IMPRINT",EDGE,{"derivedFrom":subQ0}),1.0]])]});}
            var Q177;
            {var subQ0=sQuery(id+"F0.wireOp",EDGE,"E12.6.0.49");Q177=makeQuery(id+"F0.imprint","IMPRINT",FACE,{"disambiguationData":[TD([[makeQuery(id+"F0.imprint","IMPRINT",EDGE,{"derivedFrom":subQ0}),1.0]])]});}
            var Q178;
            {var subQ0=sQuery(id+"F0.wireOp",EDGE,"E12.7.0.49");Q178=makeQuery(id+"F0.imprint","IMPRINT",FACE,{"disambiguationData":[TD([[makeQuery(id+"F0.imprint","IMPRINT",EDGE,{"derivedFrom":subQ0}),1.0]])]});}
            var Q179;
            {var subQ4=sQuery(id+"F0.wireOp",EDGE,"E12.3.0.55");Q179=makeQuery(id+"F0.imprint","IMPRINT",FACE,{"disambiguationData":[TD([[makeQuery(id+"F0.imprint","IMPRINT",EDGE,{"derivedFrom":subQ4}),-1.0]])]});}
            var Q180;
            {var subQ4=sQuery(id+"F0.wireOp",EDGE,"E12.5.0.55");Q180=makeQuery(id+"F0.imprint","IMPRINT",FACE,{"disambiguationData":[TD([[makeQuery(id+"F0.imprint","IMPRINT",EDGE,{"derivedFrom":subQ4}),-1.0]])]});}
            var Q181;
            {var subQ4=sQuery(id+"F0.wireOp",EDGE,"E12.4.0.55");Q181=makeQuery(id+"F0.imprint","IMPRINT",FACE,{"disambiguationData":[TD([[makeQuery(id+"F0.imprint","IMPRINT",EDGE,{"derivedFrom":subQ4}),-1.0]])]});}
            var Q182;
            {var subQ4=sQuery(id+"F0.wireOp",EDGE,"E12.6.0.55");Q182=makeQuery(id+"F0.imprint","IMPRINT",FACE,{"disambiguationData":[TD([[makeQuery(id+"F0.imprint","IMPRINT",EDGE,{"derivedFrom":subQ4}),-1.0]])]});}
            var Q183;
            {var subQ4=sQuery(id+"F0.wireOp",EDGE,"E12.7.0.55");Q183=makeQuery(id+"F0.imprint","IMPRINT",FACE,{"disambiguationData":[TD([[makeQuery(id+"F0.imprint","IMPRINT",EDGE,{"derivedFrom":subQ4}),-1.0]])]});}
            var Q184;
            {var subQ4=sQuery(id+"F0.wireOp",EDGE,"E12.1.0.55");Q184=makeQuery(id+"F0.imprint","IMPRINT",FACE,{"disambiguationData":[TD([[makeQuery(id+"F0.imprint","IMPRINT",EDGE,{"derivedFrom":subQ4}),-1.0]])]});}
            var Q185;
            {var subQ5=sQuery(id+"F0.wireOp",EDGE,"E6.right");Q185=makeQuery(id+"F0.imprint","IMPRINT",FACE,{"disambiguationData":[TD([[makeQuery(id+"F0.imprint","IMPRINT",EDGE,{"derivedFrom":subQ5}),-1.0]])]});}
            var Q186;
            {var subQ3=sQuery(id+"F0.wireOp",EDGE,"E12.2.0.58");Q186=makeQuery(id+"F0.imprint","IMPRINT",FACE,{"disambiguationData":[TD([[makeQuery(id+"F0.imprint","IMPRINT",EDGE,{"derivedFrom":subQ3}),1.0]])]});}
            var Q187;
            {var subQ3=sQuery(id+"F0.wireOp",EDGE,"E12.4.0.58");Q187=makeQuery(id+"F0.imprint","IMPRINT",FACE,{"disambiguationData":[TD([[makeQuery(id+"F0.imprint","IMPRINT",EDGE,{"derivedFrom":subQ3}),1.0]])]});}
            var Q188;
            {var subQ3=sQuery(id+"F0.wireOp",EDGE,"E12.3.0.58");Q188=makeQuery(id+"F0.imprint","IMPRINT",FACE,{"disambiguationData":[TD([[makeQuery(id+"F0.imprint","IMPRINT",EDGE,{"derivedFrom":subQ3}),1.0]])]});}
            var Q189;
            {var subQ3=sQuery(id+"F0.wireOp",EDGE,"E12.5.0.58");Q189=makeQuery(id+"F0.imprint","IMPRINT",FACE,{"disambiguationData":[TD([[makeQuery(id+"F0.imprint","IMPRINT",EDGE,{"derivedFrom":subQ3}),1.0]])]});}
            var Q190;
            {var subQ3=sQuery(id+"F0.wireOp",EDGE,"E12.6.0.58");Q190=makeQuery(id+"F0.imprint","IMPRINT",FACE,{"disambiguationData":[TD([[makeQuery(id+"F0.imprint","IMPRINT",EDGE,{"derivedFrom":subQ3}),1.0]])]});}
            var Q191;
            {var subQ3=sQuery(id+"F0.wireOp",EDGE,"E12.7.0.58");Q191=makeQuery(id+"F0.imprint","IMPRINT",FACE,{"disambiguationData":[TD([[makeQuery(id+"F0.imprint","IMPRINT",EDGE,{"derivedFrom":subQ3}),1.0]])]});}
            var Q192;
            {var subQ0=sQuery(id+"F0.wireOp",EDGE,"E3.left");Q192=makeQuery(id+"F0.imprint","IMPRINT",FACE,{"disambiguationData":[TD([[makeQuery(id+"F0.imprint","IMPRINT",EDGE,{"derivedFrom":subQ0}),1.0]])]});}
            var Q193;
            {var subQ5=sQuery(id+"F0.wireOp",EDGE,"E12.1.0.44");Q193=makeQuery(id+"F0.imprint","IMPRINT",FACE,{"disambiguationData":[TD([[makeQuery(id+"F0.imprint","IMPRINT",EDGE,{"derivedFrom":subQ5}),1.0]])]});}
            var Q194;
            {var subQ3=sQuery(id+"F0.wireOp",EDGE,"E12.2.0.51");Q194=makeQuery(id+"F0.imprint","IMPRINT",FACE,{"disambiguationData":[TD([[makeQuery(id+"F0.imprint","IMPRINT",EDGE,{"derivedFrom":subQ3}),1.0]])]});}
            var Q195;
            {var subQ3=sQuery(id+"F0.wireOp",EDGE,"E12.3.0.48");Q195=makeQuery(id+"F0.imprint","IMPRINT",FACE,{"disambiguationData":[TD([[makeQuery(id+"F0.imprint","IMPRINT",EDGE,{"derivedFrom":subQ3}),1.0]])]});}
            var Q196;
            {var subQ3=sQuery(id+"F0.wireOp",EDGE,"E12.3.0.51");Q196=makeQuery(id+"F0.imprint","IMPRINT",FACE,{"disambiguationData":[TD([[makeQuery(id+"F0.imprint","IMPRINT",EDGE,{"derivedFrom":subQ3}),1.0]])]});}
            var Q197;
            {var subQ3=sQuery(id+"F0.wireOp",EDGE,"E12.2.0.48");Q197=makeQuery(id+"F0.imprint","IMPRINT",FACE,{"disambiguationData":[TD([[makeQuery(id+"F0.imprint","IMPRINT",EDGE,{"derivedFrom":subQ3}),1.0]])]});}
            var Q198;
            {var subQ3=sQuery(id+"F0.wireOp",EDGE,"E12.4.0.48");Q198=makeQuery(id+"F0.imprint","IMPRINT",FACE,{"disambiguationData":[TD([[makeQuery(id+"F0.imprint","IMPRINT",EDGE,{"derivedFrom":subQ3}),1.0]])]});}
            var Q199;
            {var subQ3=sQuery(id+"F0.wireOp",EDGE,"E12.4.0.51");Q199=makeQuery(id+"F0.imprint","IMPRINT",FACE,{"disambiguationData":[TD([[makeQuery(id+"F0.imprint","IMPRINT",EDGE,{"derivedFrom":subQ3}),1.0]])]});}
            var Q200;
            {var subQ3=sQuery(id+"F0.wireOp",EDGE,"E12.6.0.51");Q200=makeQuery(id+"F0.imprint","IMPRINT",FACE,{"disambiguationData":[TD([[makeQuery(id+"F0.imprint","IMPRINT",EDGE,{"derivedFrom":subQ3}),1.0]])]});}
            var Q201;
            {var subQ3=sQuery(id+"F0.wireOp",EDGE,"E12.5.0.48");Q201=makeQuery(id+"F0.imprint","IMPRINT",FACE,{"disambiguationData":[TD([[makeQuery(id+"F0.imprint","IMPRINT",EDGE,{"derivedFrom":subQ3}),1.0]])]});}
            var Q202;
            {var subQ3=sQuery(id+"F0.wireOp",EDGE,"E12.5.0.51");Q202=makeQuery(id+"F0.imprint","IMPRINT",FACE,{"disambiguationData":[TD([[makeQuery(id+"F0.imprint","IMPRINT",EDGE,{"derivedFrom":subQ3}),1.0]])]});}
            var Q203;
            {var subQ3=sQuery(id+"F0.wireOp",EDGE,"E12.7.0.48");Q203=makeQuery(id+"F0.imprint","IMPRINT",FACE,{"disambiguationData":[TD([[makeQuery(id+"F0.imprint","IMPRINT",EDGE,{"derivedFrom":subQ3}),1.0]])]});}
            var Q204;
            {var subQ3=sQuery(id+"F0.wireOp",EDGE,"E12.7.0.51");Q204=makeQuery(id+"F0.imprint","IMPRINT",FACE,{"disambiguationData":[TD([[makeQuery(id+"F0.imprint","IMPRINT",EDGE,{"derivedFrom":subQ3}),1.0]])]});}
            var Q205;
            {var subQ3=sQuery(id+"F0.wireOp",EDGE,"E12.6.0.48");Q205=makeQuery(id+"F0.imprint","IMPRINT",FACE,{"disambiguationData":[TD([[makeQuery(id+"F0.imprint","IMPRINT",EDGE,{"derivedFrom":subQ3}),1.0]])]});}
            var Q206;
            {var subQ5=sQuery(id+"F0.wireOp",EDGE,"E12.3.0.44");Q206=makeQuery(id+"F0.imprint","IMPRINT",FACE,{"disambiguationData":[TD([[makeQuery(id+"F0.imprint","IMPRINT",EDGE,{"derivedFrom":subQ5}),1.0]])]});}
            var Q207;
            {var subQ0=sQuery(id+"F0.wireOp",EDGE,"E12.2.0.43");Q207=makeQuery(id+"F0.imprint","IMPRINT",FACE,{"disambiguationData":[TD([[makeQuery(id+"F0.imprint","IMPRINT",EDGE,{"derivedFrom":subQ0}),-1.0]])]});}
            var Q208;
            {var subQ4=sQuery(id+"F0.wireOp",EDGE,"E12.3.0.50");Q208=makeQuery(id+"F0.imprint","IMPRINT",FACE,{"disambiguationData":[TD([[makeQuery(id+"F0.imprint","IMPRINT",EDGE,{"derivedFrom":subQ4}),1.0]])]});}
            var Q209;
            {var subQ4=sQuery(id+"F0.wireOp",EDGE,"E12.2.0.50");Q209=makeQuery(id+"F0.imprint","IMPRINT",FACE,{"disambiguationData":[TD([[makeQuery(id+"F0.imprint","IMPRINT",EDGE,{"derivedFrom":subQ4}),1.0]])]});}
            var Q210;
            {var subQ0=sQuery(id+"F0.wireOp",EDGE,"E12.2.0.49");Q210=makeQuery(id+"F0.imprint","IMPRINT",FACE,{"disambiguationData":[TD([[makeQuery(id+"F0.imprint","IMPRINT",EDGE,{"derivedFrom":subQ0}),1.0]])]});}
            var Q211;
            {var subQ3=sQuery(id+"F0.wireOp",EDGE,"E12.4.0.59");Q211=makeQuery(id+"F0.imprint","IMPRINT",FACE,{"disambiguationData":[TD([[makeQuery(id+"F0.imprint","IMPRINT",EDGE,{"derivedFrom":subQ3}),1.0]])]});}
            var Q212;
            {var subQ0=sQuery(id+"F0.wireOp",EDGE,"E12.3.0.49");Q212=makeQuery(id+"F0.imprint","IMPRINT",FACE,{"disambiguationData":[TD([[makeQuery(id+"F0.imprint","IMPRINT",EDGE,{"derivedFrom":subQ0}),1.0]])]});}
            var Q213;
            {var subQ3=sQuery(id+"F0.wireOp",EDGE,"E12.5.0.59");Q213=makeQuery(id+"F0.imprint","IMPRINT",FACE,{"disambiguationData":[TD([[makeQuery(id+"F0.imprint","IMPRINT",EDGE,{"derivedFrom":subQ3}),1.0]])]});}
            var Q214;
            {var subQ3=sQuery(id+"F0.wireOp",EDGE,"E12.6.0.59");Q214=makeQuery(id+"F0.imprint","IMPRINT",FACE,{"disambiguationData":[TD([[makeQuery(id+"F0.imprint","IMPRINT",EDGE,{"derivedFrom":subQ3}),1.0]])]});}
            var Q215;
            {var subQ3=sQuery(id+"F0.wireOp",EDGE,"E12.7.0.59");Q215=makeQuery(id+"F0.imprint","IMPRINT",FACE,{"disambiguationData":[TD([[makeQuery(id+"F0.imprint","IMPRINT",EDGE,{"derivedFrom":subQ3}),1.0]])]});}
            var Q216;
            {var subQ4=sQuery(id+"F0.wireOp",EDGE,"E12.2.0.55");Q216=makeQuery(id+"F0.imprint","IMPRINT",FACE,{"disambiguationData":[TD([[makeQuery(id+"F0.imprint","IMPRINT",EDGE,{"derivedFrom":subQ4}),-1.0]])]});}
            var Q217;
            {var subQ5=sQuery(id+"F0.wireOp",EDGE,"E12.2.0.44");Q217=makeQuery(id+"F0.imprint","IMPRINT",FACE,{"disambiguationData":[TD([[makeQuery(id+"F0.imprint","IMPRINT",EDGE,{"derivedFrom":subQ5}),1.0]])]});}
            var Q218;
            {var subQ5=sQuery(id+"F0.wireOp",EDGE,"E12.5.0.44");Q218=makeQuery(id+"F0.imprint","IMPRINT",FACE,{"disambiguationData":[TD([[makeQuery(id+"F0.imprint","IMPRINT",EDGE,{"derivedFrom":subQ5}),1.0]])]});}
            var Q219;
            {var subQ3=sQuery(id+"F0.wireOp",EDGE,"E12.2.0.59");Q219=makeQuery(id+"F0.imprint","IMPRINT",FACE,{"disambiguationData":[TD([[makeQuery(id+"F0.imprint","IMPRINT",EDGE,{"derivedFrom":subQ3}),1.0]])]});}
            var Q220;
            {var subQ3=sQuery(id+"F0.wireOp",EDGE,"E12.3.0.59");Q220=makeQuery(id+"F0.imprint","IMPRINT",FACE,{"disambiguationData":[TD([[makeQuery(id+"F0.imprint","IMPRINT",EDGE,{"derivedFrom":subQ3}),1.0]])]});}
            var Q221;
            {var subQ5=sQuery(id+"F0.wireOp",EDGE,"E12.6.0.44");Q221=makeQuery(id+"F0.imprint","IMPRINT",FACE,{"disambiguationData":[TD([[makeQuery(id+"F0.imprint","IMPRINT",EDGE,{"derivedFrom":subQ5}),1.0]])]});}
            var Q222;
            {var subQ5=sQuery(id+"F0.wireOp",EDGE,"E12.4.0.44");Q222=makeQuery(id+"F0.imprint","IMPRINT",FACE,{"disambiguationData":[TD([[makeQuery(id+"F0.imprint","IMPRINT",EDGE,{"derivedFrom":subQ5}),1.0]])]});}
            var Q223;
            {var subQ5=sQuery(id+"F0.wireOp",EDGE,"E12.7.0.44");Q223=makeQuery(id+"F0.imprint","IMPRINT",FACE,{"disambiguationData":[TD([[makeQuery(id+"F0.imprint","IMPRINT",EDGE,{"derivedFrom":subQ5}),1.0]])]});}
            extrude(context, id + "F1", {"entities" : qUnion([Q0, Q1, Q2, Q3, Q4, Q5, Q6, Q7, Q8, Q9, Q10, Q11, Q12, Q13, Q14, Q15, Q16, Q17, Q18, Q19, Q20, Q21, Q22, Q23, Q24, Q25, Q26, Q27, Q28, Q29, Q30, Q31, Q32, Q33, Q34, Q35, Q36, Q37, Q38, Q39, Q40, Q41, Q42, Q43, Q44, Q45, Q46, Q47, Q48, Q49, Q50, Q51, Q52, Q53, Q54, Q55, Q56, Q57, Q58, Q59, Q60, Q61, Q62, Q63, Q64, Q65, Q66, Q67, Q68, Q69, Q70, Q71, Q72, Q73, Q74, Q75, Q76, Q77, Q78, Q79, Q80, Q81, Q82, Q83, Q84, Q85, Q86, Q87, Q88, Q89, Q90, Q91, Q92, Q93, Q94, Q95, Q96, Q97, Q98, Q99, Q100, Q101, Q102, Q103, Q104, Q105, Q106, Q107, Q108, Q109, Q110, Q111, Q112, Q113, Q114, Q115, Q116, Q117, Q118, Q119, Q120, Q121, Q122, Q123, Q124, Q125, Q126, Q127, Q128, Q129, Q130, Q131, Q132, Q133, Q134, Q135, Q136, Q137, Q138, Q139, Q140, Q141, Q142, Q143, Q144, Q145, Q146, Q147, Q148, Q149, Q150, Q151, Q152, Q153, Q154, Q155, Q156, Q157, Q158, Q159, Q160, Q161, Q162, Q163, Q164, Q165, Q166, Q167, Q168, Q169, Q170, Q171, Q172, Q173, Q174, Q175, Q176, Q177, Q178, Q179, Q180, Q181, Q182, Q183, Q184, Q185, Q186, Q187, Q188, Q189, Q190, Q191, Q192, Q193, Q194, Q195, Q196, Q197, Q198, Q199, Q200, Q201, Q202, Q203, Q204, Q205, Q206, Q207, Q208, Q209, Q210, Q211, Q212, Q213, Q214, Q215, Q216, Q217, Q218, Q219, Q220, Q221, Q222, Q223]), "oppositeDirection" : true, "depth" : .15 * mm, "offsetDistance" : 25.4 * mm});
        }
    });
